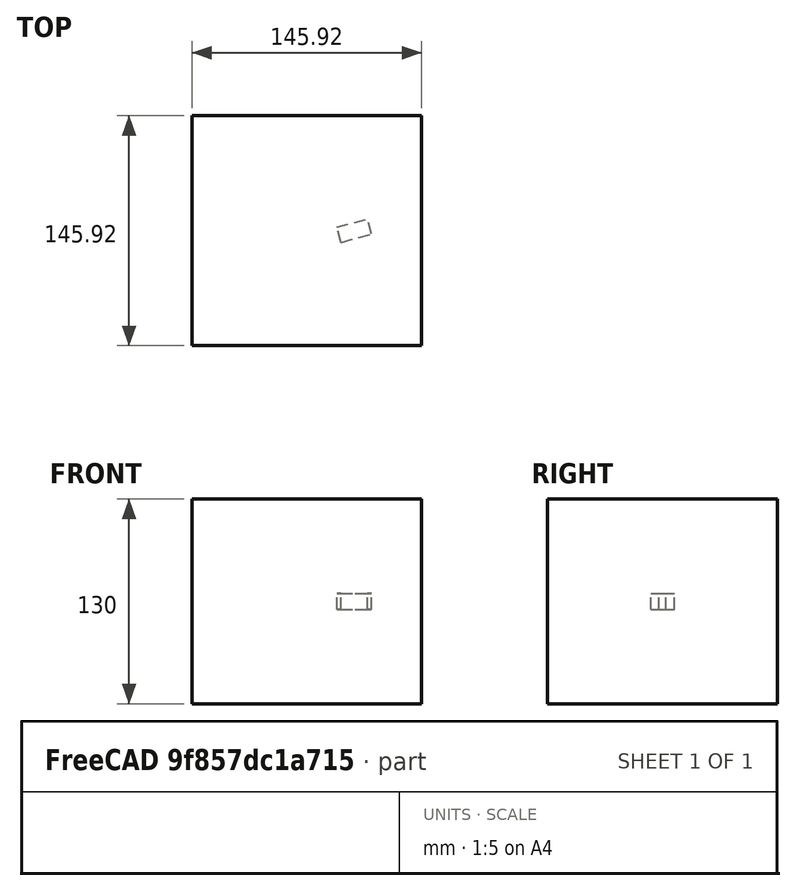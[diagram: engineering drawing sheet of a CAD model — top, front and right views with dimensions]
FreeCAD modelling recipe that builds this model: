
FCSTD DOCUMENT  (FreeCAD 0.20RUnknown)
Label: array-rotation-test-d
License: All rights reserved
objects: App::DocumentObjectGroupPython×1251, Part::FeaturePython×3, App::Part×2
note: 2 computed .brp shape members not serialized (recipe doc carries the construction recipe); baked Part::Feature solids carry a one-line shape summary decoded from their .brp

FEATURE [App::DocumentObjectGroupPython] HALFPI  # scripted group (container) (typed FeaturePython)
  name = HALFPI
  value = pi/2.
FEATURE [App::DocumentObjectGroupPython] PI  # scripted group (container) (typed FeaturePython)
  name = PI
  value = 1.*pi
FEATURE [App::DocumentObjectGroupPython] TWOPI  # scripted group (container) (typed FeaturePython)
  name = TWOPI
  value = 2.*pi
FEATURE [App::DocumentObjectGroupPython] Constants  # scripted group (container) (typed FeaturePython)
  Group = -> [HALFPI,PI,TWOPI]
FEATURE [App::DocumentObjectGroupPython] Variables  # scripted group (container) (typed FeaturePython)
FEATURE [App::DocumentObjectGroupPython] Quantities  # scripted group (container) (typed FeaturePython)
FEATURE [App::DocumentObjectGroupPython] Isotopes  # scripted group (container) (typed FeaturePython)
FEATURE [App::DocumentObjectGroupPython] Elements  # scripted group (container) (typed FeaturePython)
FEATURE [App::DocumentObjectGroupPython] Matrix  # scripted group (container) (typed FeaturePython)
FEATURE [App::DocumentObjectGroupPython] Surfaces  # scripted group (container) (typed FeaturePython)
FEATURE [App::DocumentObjectGroupPython] Opticals  # scripted group (container) (typed FeaturePython)
  Group = -> [Matrix,Surfaces]
FEATURE [App::DocumentObjectGroupPython] G4Isotopes  # scripted group (container) (typed FeaturePython)
FEATURE [App::DocumentObjectGroupPython] H_element  # scripted group (container) (typed FeaturePython)
  Z = 1
  atom_value = 1.008
  formula = H
  name = H_element
FEATURE [App::DocumentObjectGroupPython] He_element  # scripted group (container) (typed FeaturePython)
  Z = 2
  atom_value = 4.0026
  formula = He
  name = He_element
FEATURE [App::DocumentObjectGroupPython] Li_element  # scripted group (container) (typed FeaturePython)
  Z = 3
  atom_value = 6.94
  formula = Li
  name = Li_element
FEATURE [App::DocumentObjectGroupPython] Be_element  # scripted group (container) (typed FeaturePython)
  Z = 4
  atom_value = 9.01218
  formula = Be
  name = Be_element
FEATURE [App::DocumentObjectGroupPython] B_element  # scripted group (container) (typed FeaturePython)
  Z = 5
  atom_value = 10.81
  formula = B
  name = B_element
FEATURE [App::DocumentObjectGroupPython] C_element  # scripted group (container) (typed FeaturePython)
  Z = 6
  atom_value = 12.011
  formula = C
  name = C_element
FEATURE [App::DocumentObjectGroupPython] N_element  # scripted group (container) (typed FeaturePython)
  Z = 7
  atom_value = 14.007
  formula = N
  name = N_element
FEATURE [App::DocumentObjectGroupPython] O_element  # scripted group (container) (typed FeaturePython)
  Z = 8
  atom_value = 15.999
  formula = O
  name = O_element
FEATURE [App::DocumentObjectGroupPython] F_element  # scripted group (container) (typed FeaturePython)
  Z = 9
  atom_value = 18.9984
  formula = F
  name = F_element
FEATURE [App::DocumentObjectGroupPython] Ne_element  # scripted group (container) (typed FeaturePython)
  Z = 10
  atom_value = 20.1797
  formula = Ne
  name = Ne_element
FEATURE [App::DocumentObjectGroupPython] Na_element  # scripted group (container) (typed FeaturePython)
  Z = 11
  atom_value = 22.9898
  formula = Na
  name = Na_element
FEATURE [App::DocumentObjectGroupPython] Mg_element  # scripted group (container) (typed FeaturePython)
  Z = 12
  atom_value = 24.305
  formula = Mg
  name = Mg_element
FEATURE [App::DocumentObjectGroupPython] Al_element  # scripted group (container) (typed FeaturePython)
  Z = 13
  atom_value = 26.9815
  formula = Al
  name = Al_element
FEATURE [App::DocumentObjectGroupPython] Si_element  # scripted group (container) (typed FeaturePython)
  Z = 14
  atom_value = 28.085
  formula = Si
  name = Si_element
FEATURE [App::DocumentObjectGroupPython] P_element  # scripted group (container) (typed FeaturePython)
  Z = 15
  atom_value = 30.9738
  formula = P
  name = P_element
FEATURE [App::DocumentObjectGroupPython] S_element  # scripted group (container) (typed FeaturePython)
  Z = 16
  atom_value = 32.06
  formula = S
  name = S_element
FEATURE [App::DocumentObjectGroupPython] Cl_element  # scripted group (container) (typed FeaturePython)
  Z = 17
  atom_value = 35.45
  formula = Cl
  name = Cl_element
FEATURE [App::DocumentObjectGroupPython] Ar_element  # scripted group (container) (typed FeaturePython)
  Z = 18
  atom_value = 39.95
  formula = Ar
  name = Ar_element
FEATURE [App::DocumentObjectGroupPython] K_element  # scripted group (container) (typed FeaturePython)
  Z = 19
  atom_value = 39.0983
  formula = K
  name = K_element
FEATURE [App::DocumentObjectGroupPython] Ca_element  # scripted group (container) (typed FeaturePython)
  Z = 20
  atom_value = 40.078
  formula = Ca
  name = Ca_element
FEATURE [App::DocumentObjectGroupPython] Sc_element  # scripted group (container) (typed FeaturePython)
  Z = 21
  atom_value = 44.9559
  formula = Sc
  name = Sc_element
FEATURE [App::DocumentObjectGroupPython] Ti_element  # scripted group (container) (typed FeaturePython)
  Z = 22
  atom_value = 47.867
  formula = Ti
  name = Ti_element
FEATURE [App::DocumentObjectGroupPython] V_element  # scripted group (container) (typed FeaturePython)
  Z = 23
  atom_value = 50.9415
  formula = V
  name = V_element
FEATURE [App::DocumentObjectGroupPython] Cr_element  # scripted group (container) (typed FeaturePython)
  Z = 24
  atom_value = 51.9961
  formula = Cr
  name = Cr_element
FEATURE [App::DocumentObjectGroupPython] Mn_element  # scripted group (container) (typed FeaturePython)
  Z = 25
  atom_value = 54.938
  formula = Mn
  name = Mn_element
FEATURE [App::DocumentObjectGroupPython] Fe_element  # scripted group (container) (typed FeaturePython)
  Z = 26
  atom_value = 55.845
  formula = Fe
  name = Fe_element
FEATURE [App::DocumentObjectGroupPython] Co_element  # scripted group (container) (typed FeaturePython)
  Z = 27
  atom_value = 58.9332
  formula = Co
  name = Co_element
FEATURE [App::DocumentObjectGroupPython] Ni_element  # scripted group (container) (typed FeaturePython)
  Z = 28
  atom_value = 58.6934
  formula = Ni
  name = Ni_element
FEATURE [App::DocumentObjectGroupPython] Cu_element  # scripted group (container) (typed FeaturePython)
  Z = 29
  atom_value = 63.546
  formula = Cu
  name = Cu_element
FEATURE [App::DocumentObjectGroupPython] Zn_element  # scripted group (container) (typed FeaturePython)
  Z = 30
  atom_value = 65.38
  formula = Zn
  name = Zn_element
FEATURE [App::DocumentObjectGroupPython] Ga_element  # scripted group (container) (typed FeaturePython)
  Z = 31
  atom_value = 69.723
  formula = Ga
  name = Ga_element
FEATURE [App::DocumentObjectGroupPython] Ge_element  # scripted group (container) (typed FeaturePython)
  Z = 32
  atom_value = 72.63
  formula = Ge
  name = Ge_element
FEATURE [App::DocumentObjectGroupPython] As_element  # scripted group (container) (typed FeaturePython)
  Z = 33
  atom_value = 74.9216
  formula = As
  name = As_element
FEATURE [App::DocumentObjectGroupPython] Se_element  # scripted group (container) (typed FeaturePython)
  Z = 34
  atom_value = 78.971
  formula = Se
  name = Se_element
FEATURE [App::DocumentObjectGroupPython] Br_element  # scripted group (container) (typed FeaturePython)
  Z = 35
  atom_value = 79.904
  formula = Br
  name = Br_element
FEATURE [App::DocumentObjectGroupPython] Kr_element  # scripted group (container) (typed FeaturePython)
  Z = 36
  atom_value = 83.798
  formula = Kr
  name = Kr_element
FEATURE [App::DocumentObjectGroupPython] Rb_element  # scripted group (container) (typed FeaturePython)
  Z = 37
  atom_value = 85.4678
  formula = Rb
  name = Rb_element
FEATURE [App::DocumentObjectGroupPython] Sr_element  # scripted group (container) (typed FeaturePython)
  Z = 38
  atom_value = 87.62
  formula = Sr
  name = Sr_element
FEATURE [App::DocumentObjectGroupPython] Y_element  # scripted group (container) (typed FeaturePython)
  Z = 39
  atom_value = 88.9058
  formula = Y
  name = Y_element
FEATURE [App::DocumentObjectGroupPython] Zr_element  # scripted group (container) (typed FeaturePython)
  Z = 40
  atom_value = 91.224
  formula = Zr
  name = Zr_element
FEATURE [App::DocumentObjectGroupPython] Nb_element  # scripted group (container) (typed FeaturePython)
  Z = 41
  atom_value = 92.9064
  formula = Nb
  name = Nb_element
FEATURE [App::DocumentObjectGroupPython] Mo_element  # scripted group (container) (typed FeaturePython)
  Z = 42
  atom_value = 95.95
  formula = Mo
  name = Mo_element
FEATURE [App::DocumentObjectGroupPython] Tc_element  # scripted group (container) (typed FeaturePython)
  Z = 43
  atom_value = 97
  formula = Tc
  name = Tc_element
FEATURE [App::DocumentObjectGroupPython] Ru_element  # scripted group (container) (typed FeaturePython)
  Z = 44
  atom_value = 101.07
  formula = Ru
  name = Ru_element
FEATURE [App::DocumentObjectGroupPython] Rh_element  # scripted group (container) (typed FeaturePython)
  Z = 45
  atom_value = 102.905
  formula = Rh
  name = Rh_element
FEATURE [App::DocumentObjectGroupPython] Pd_element  # scripted group (container) (typed FeaturePython)
  Z = 46
  atom_value = 106.42
  formula = Pd
  name = Pd_element
FEATURE [App::DocumentObjectGroupPython] Ag_element  # scripted group (container) (typed FeaturePython)
  Z = 47
  atom_value = 107.868
  formula = Ag
  name = Ag_element
FEATURE [App::DocumentObjectGroupPython] Cd_element  # scripted group (container) (typed FeaturePython)
  Z = 48
  atom_value = 112.414
  formula = Cd
  name = Cd_element
FEATURE [App::DocumentObjectGroupPython] In_element  # scripted group (container) (typed FeaturePython)
  Z = 49
  atom_value = 114.818
  formula = In
  name = In_element
FEATURE [App::DocumentObjectGroupPython] Sn_element  # scripted group (container) (typed FeaturePython)
  Z = 50
  atom_value = 118.71
  formula = Sn
  name = Sn_element
FEATURE [App::DocumentObjectGroupPython] Sb_element  # scripted group (container) (typed FeaturePython)
  Z = 51
  atom_value = 121.76
  formula = Sb
  name = Sb_element
FEATURE [App::DocumentObjectGroupPython] Te_element  # scripted group (container) (typed FeaturePython)
  Z = 52
  atom_value = 127.6
  formula = Te
  name = Te_element
FEATURE [App::DocumentObjectGroupPython] I_element  # scripted group (container) (typed FeaturePython)
  Z = 53
  atom_value = 126.904
  formula = I
  name = I_element
FEATURE [App::DocumentObjectGroupPython] Xe_element  # scripted group (container) (typed FeaturePython)
  Z = 54
  atom_value = 131.293
  formula = Xe
  name = Xe_element
FEATURE [App::DocumentObjectGroupPython] Cs_element  # scripted group (container) (typed FeaturePython)
  Z = 55
  atom_value = 132.905
  formula = Cs
  name = Cs_element
FEATURE [App::DocumentObjectGroupPython] Ba_element  # scripted group (container) (typed FeaturePython)
  Z = 56
  atom_value = 137.327
  formula = Ba
  name = Ba_element
FEATURE [App::DocumentObjectGroupPython] La_element  # scripted group (container) (typed FeaturePython)
  Z = 57
  atom_value = 138.905
  formula = La
  name = La_element
FEATURE [App::DocumentObjectGroupPython] Ce_element  # scripted group (container) (typed FeaturePython)
  Z = 58
  atom_value = 140.116
  formula = Ce
  name = Ce_element
FEATURE [App::DocumentObjectGroupPython] Pr_element  # scripted group (container) (typed FeaturePython)
  Z = 59
  atom_value = 140.908
  formula = Pr
  name = Pr_element
FEATURE [App::DocumentObjectGroupPython] Nd_element  # scripted group (container) (typed FeaturePython)
  Z = 60
  atom_value = 144.242
  formula = Nd
  name = Nd_element
FEATURE [App::DocumentObjectGroupPython] Pm_element  # scripted group (container) (typed FeaturePython)
  Z = 61
  atom_value = 145
  formula = Pm
  name = Pm_element
FEATURE [App::DocumentObjectGroupPython] Sm_element  # scripted group (container) (typed FeaturePython)
  Z = 62
  atom_value = 150.36
  formula = Sm
  name = Sm_element
FEATURE [App::DocumentObjectGroupPython] Eu_element  # scripted group (container) (typed FeaturePython)
  Z = 63
  atom_value = 151.964
  formula = Eu
  name = Eu_element
FEATURE [App::DocumentObjectGroupPython] Gd_element  # scripted group (container) (typed FeaturePython)
  Z = 64
  atom_value = 157.25
  formula = Gd
  name = Gd_element
FEATURE [App::DocumentObjectGroupPython] Tb_element  # scripted group (container) (typed FeaturePython)
  Z = 65
  atom_value = 158.925
  formula = Tb
  name = Tb_element
FEATURE [App::DocumentObjectGroupPython] Dy_element  # scripted group (container) (typed FeaturePython)
  Z = 66
  atom_value = 162.5
  formula = Dy
  name = Dy_element
FEATURE [App::DocumentObjectGroupPython] Ho_element  # scripted group (container) (typed FeaturePython)
  Z = 67
  atom_value = 164.93
  formula = Ho
  name = Ho_element
FEATURE [App::DocumentObjectGroupPython] Er_element  # scripted group (container) (typed FeaturePython)
  Z = 68
  atom_value = 167.259
  formula = Er
  name = Er_element
FEATURE [App::DocumentObjectGroupPython] Tm_element  # scripted group (container) (typed FeaturePython)
  Z = 69
  atom_value = 168.934
  formula = Tm
  name = Tm_element
FEATURE [App::DocumentObjectGroupPython] Yb_element  # scripted group (container) (typed FeaturePython)
  Z = 70
  atom_value = 173.045
  formula = Yb
  name = Yb_element
FEATURE [App::DocumentObjectGroupPython] Lu_element  # scripted group (container) (typed FeaturePython)
  Z = 71
  atom_value = 174.967
  formula = Lu
  name = Lu_element
FEATURE [App::DocumentObjectGroupPython] Hf_element  # scripted group (container) (typed FeaturePython)
  Z = 72
  atom_value = 178.49
  formula = Hf
  name = Hf_element
FEATURE [App::DocumentObjectGroupPython] Ta_element  # scripted group (container) (typed FeaturePython)
  Z = 73
  atom_value = 180.948
  formula = Ta
  name = Ta_element
FEATURE [App::DocumentObjectGroupPython] W_element  # scripted group (container) (typed FeaturePython)
  Z = 74
  atom_value = 183.84
  formula = W
  name = W_element
FEATURE [App::DocumentObjectGroupPython] Re_element  # scripted group (container) (typed FeaturePython)
  Z = 75
  atom_value = 186.207
  formula = Re
  name = Re_element
FEATURE [App::DocumentObjectGroupPython] Os_element  # scripted group (container) (typed FeaturePython)
  Z = 76
  atom_value = 190.23
  formula = Os
  name = Os_element
FEATURE [App::DocumentObjectGroupPython] Ir_element  # scripted group (container) (typed FeaturePython)
  Z = 77
  atom_value = 192.217
  formula = Ir
  name = Ir_element
FEATURE [App::DocumentObjectGroupPython] Pt_element  # scripted group (container) (typed FeaturePython)
  Z = 78
  atom_value = 195.084
  formula = Pt
  name = Pt_element
FEATURE [App::DocumentObjectGroupPython] Au_element  # scripted group (container) (typed FeaturePython)
  Z = 79
  atom_value = 196.967
  formula = Au
  name = Au_element
FEATURE [App::DocumentObjectGroupPython] Hg_element  # scripted group (container) (typed FeaturePython)
  Z = 80
  atom_value = 200.592
  formula = Hg
  name = Hg_element
FEATURE [App::DocumentObjectGroupPython] Tl_element  # scripted group (container) (typed FeaturePython)
  Z = 81
  atom_value = 204.38
  formula = Tl
  name = Tl_element
FEATURE [App::DocumentObjectGroupPython] Pb_element  # scripted group (container) (typed FeaturePython)
  Z = 82
  atom_value = 207.2
  formula = Pb
  name = Pb_element
FEATURE [App::DocumentObjectGroupPython] Bi_element  # scripted group (container) (typed FeaturePython)
  Z = 83
  atom_value = 208.98
  formula = Bi
  name = Bi_element
FEATURE [App::DocumentObjectGroupPython] Po_element  # scripted group (container) (typed FeaturePython)
  Z = 84
  atom_value = 209
  formula = Po
  name = Po_element
FEATURE [App::DocumentObjectGroupPython] At_element  # scripted group (container) (typed FeaturePython)
  Z = 85
  atom_value = 210
  formula = At
  name = At_element
FEATURE [App::DocumentObjectGroupPython] Rn_element  # scripted group (container) (typed FeaturePython)
  Z = 86
  atom_value = 222
  formula = Rn
  name = Rn_element
FEATURE [App::DocumentObjectGroupPython] Fr_element  # scripted group (container) (typed FeaturePython)
  Z = 87
  atom_value = 223
  formula = Fr
  name = Fr_element
FEATURE [App::DocumentObjectGroupPython] Ra_element  # scripted group (container) (typed FeaturePython)
  Z = 88
  atom_value = 226
  formula = Ra
  name = Ra_element
FEATURE [App::DocumentObjectGroupPython] Ac_element  # scripted group (container) (typed FeaturePython)
  Z = 89
  atom_value = 227
  formula = Ac
  name = Ac_element
FEATURE [App::DocumentObjectGroupPython] Th_element  # scripted group (container) (typed FeaturePython)
  Z = 90
  atom_value = 232.038
  formula = Th
  name = Th_element
FEATURE [App::DocumentObjectGroupPython] Pa_element  # scripted group (container) (typed FeaturePython)
  Z = 91
  atom_value = 231.036
  formula = Pa
  name = Pa_element
FEATURE [App::DocumentObjectGroupPython] U_element  # scripted group (container) (typed FeaturePython)
  Z = 92
  atom_value = 238.029
  formula = U
  name = U_element
FEATURE [App::DocumentObjectGroupPython] Np_element  # scripted group (container) (typed FeaturePython)
  Z = 93
  atom_value = 237
  formula = Np
  name = Np_element
FEATURE [App::DocumentObjectGroupPython] Pu_element  # scripted group (container) (typed FeaturePython)
  Z = 94
  atom_value = 244
  formula = Pu
  name = Pu_element
FEATURE [App::DocumentObjectGroupPython] Am_element  # scripted group (container) (typed FeaturePython)
  Z = 95
  atom_value = 243
  formula = Am
  name = Am_element
FEATURE [App::DocumentObjectGroupPython] Cm_element  # scripted group (container) (typed FeaturePython)
  Z = 96
  atom_value = 247
  formula = Cm
  name = Cm_element
FEATURE [App::DocumentObjectGroupPython] Bk_element  # scripted group (container) (typed FeaturePython)
  Z = 97
  atom_value = 247
  formula = Bk
  name = Bk_element
FEATURE [App::DocumentObjectGroupPython] Cf_element  # scripted group (container) (typed FeaturePython)
  Z = 98
  atom_value = 251
  formula = Cf
  name = Cf_element
FEATURE [App::DocumentObjectGroupPython] G4Elements  # scripted group (container) (typed FeaturePython)
  Group = -> [H_element,He_element,Li_element,Be_element,B_element,C_element,N_element,O_element,F_element,Ne_element,Na_element,Mg_element,Al_element,Si_element,P_element,S_element,Cl_element,Ar_element,K_element,Ca_element,Sc_element,Ti_element,V_element,Cr_element,Mn_element,Fe_element,Co_element,Ni_element,Cu_element,Zn_element,Ga_element,Ge_element,As_element,Se_element,Br_element,Kr_element,Rb_element,+61 more]
FEATURE [App::DocumentObjectGroupPython] H_element001  label="H_element : 0.101"  # scripted group (container) (typed FeaturePython)
  n = 0.101327
FEATURE [App::DocumentObjectGroupPython] C_element001  label="C_element : 0.775"  # scripted group (container) (typed FeaturePython)
  n = 0.7755
FEATURE [App::DocumentObjectGroupPython] N_element001  label="N_element : 0.035"  # scripted group (container) (typed FeaturePython)
  n = 0.035057
FEATURE [App::DocumentObjectGroupPython] O_element001  label="O_element : 0.052"  # scripted group (container) (typed FeaturePython)
  n = 0.0523159
FEATURE [App::DocumentObjectGroupPython] F_element001  label="F_element : 0.017"  # scripted group (container) (typed FeaturePython)
  n = 0.017422
FEATURE [App::DocumentObjectGroupPython] Ca_element001  label="Ca_element : 0.018"  # scripted group (container) (typed FeaturePython)
  n = 0.018378
FEATURE [App::DocumentObjectGroupPython] G4_A_150_TISSUE  label="G4_A-150_TISSUE"  # scripted group (container) (typed FeaturePython)
  Dunit = g/cm3
  Dvalue = 1.127
  Group = -> [H_element001,C_element001,N_element001,O_element001,F_element001,Ca_element001]
  conduct = 2
  density = 1
  expand = 3
  formula = G4_A-150_TISSUE
  name = G4_A-150_TISSUE
  specific = 4
FEATURE [App::DocumentObjectGroupPython] C_element002  label="C_element : 3"  # scripted group (container) (typed FeaturePython)
  n = 3
  ref = C_element
FEATURE [App::DocumentObjectGroupPython] H_element002  label="H_element : 6"  # scripted group (container) (typed FeaturePython)
  n = 6
  ref = H_element
FEATURE [App::DocumentObjectGroupPython] O_element002  label="O_element : 1"  # scripted group (container) (typed FeaturePython)
  n = 1
  ref = O_element
FEATURE [App::DocumentObjectGroupPython] G4_ACETONE  # scripted group (container) (typed FeaturePython)
  Dunit = g/cm3
  Dvalue = 0.7899
  Group = -> [C_element002,H_element002,O_element002]
  conduct = 2
  density = 1
  expand = 3
  formula = G4_ACETONE
  name = G4_ACETONE
  specific = 4
FEATURE [App::DocumentObjectGroupPython] C_element003  label="C_element : 2"  # scripted group (container) (typed FeaturePython)
  n = 2
  ref = C_element
FEATURE [App::DocumentObjectGroupPython] H_element003  label="H_element : 2"  # scripted group (container) (typed FeaturePython)
  n = 2
  ref = H_element
FEATURE [App::DocumentObjectGroupPython] G4_ACETYLENE  # scripted group (container) (typed FeaturePython)
  Dunit = g/cm3
  Dvalue = 0.0010967
  Group = -> [C_element003,H_element003]
  conduct = 2
  density = 1
  expand = 3
  formula = G4_ACETYLENE
  name = G4_ACETYLENE
  specific = 4
FEATURE [App::DocumentObjectGroupPython] C_element004  label="C_element : 5"  # scripted group (container) (typed FeaturePython)
  n = 5
  ref = C_element
FEATURE [App::DocumentObjectGroupPython] H_element004  label="H_element : 5"  # scripted group (container) (typed FeaturePython)
  n = 5
  ref = H_element
FEATURE [App::DocumentObjectGroupPython] N_element002  label="N_element : 5"  # scripted group (container) (typed FeaturePython)
  n = 5
  ref = N_element
FEATURE [App::DocumentObjectGroupPython] G4_ADENINE  # scripted group (container) (typed FeaturePython)
  Dunit = g/cm3
  Dvalue = 1.6
  Group = -> [C_element004,H_element004,N_element002]
  conduct = 2
  density = 1
  expand = 3
  formula = G4_ADENINE
  name = G4_ADENINE
  specific = 4
FEATURE [App::DocumentObjectGroupPython] H_element005  label="H_element : 0.114"  # scripted group (container) (typed FeaturePython)
  n = 0.114
FEATURE [App::DocumentObjectGroupPython] C_element005  label="C_element : 0.598"  # scripted group (container) (typed FeaturePython)
  n = 0.598
FEATURE [App::DocumentObjectGroupPython] N_element003  label="N_element : 0.007"  # scripted group (container) (typed FeaturePython)
  n = 0.007
FEATURE [App::DocumentObjectGroupPython] O_element003  label="O_element : 0.278"  # scripted group (container) (typed FeaturePython)
  n = 0.278
FEATURE [App::DocumentObjectGroupPython] Na_element001  label="Na_element : 0.001"  # scripted group (container) (typed FeaturePython)
  n = 0.001
FEATURE [App::DocumentObjectGroupPython] S_element001  label="S_element : 0.001"  # scripted group (container) (typed FeaturePython)
  n = 0.001
FEATURE [App::DocumentObjectGroupPython] Cl_element001  label="Cl_element : 0.001"  # scripted group (container) (typed FeaturePython)
  n = 0.001
FEATURE [App::DocumentObjectGroupPython] G4_ADIPOSE_TISSUE_ICRP  # scripted group (container) (typed FeaturePython)
  Dunit = g/cm3
  Dvalue = 0.95
  Group = -> [H_element005,C_element005,N_element003,O_element003,Na_element001,S_element001,Cl_element001]
  conduct = 2
  density = 1
  expand = 3
  formula = G4_ADIPOSE_TISSUE_ICRP
  name = G4_ADIPOSE_TISSUE_ICRP
  specific = 4
FEATURE [App::DocumentObjectGroupPython] C_element006  label="C_element : 0.000"  # scripted group (container) (typed FeaturePython)
  n = 0.000124
FEATURE [App::DocumentObjectGroupPython] N_element004  label="N_element : 0.755"  # scripted group (container) (typed FeaturePython)
  n = 0.755268
FEATURE [App::DocumentObjectGroupPython] O_element004  label="O_element : 0.232"  # scripted group (container) (typed FeaturePython)
  n = 0.231781
FEATURE [App::DocumentObjectGroupPython] Ar_element001  label="Ar_element : 0.013"  # scripted group (container) (typed FeaturePython)
  n = 0.012827
FEATURE [App::DocumentObjectGroupPython] G4_AIR  # scripted group (container) (typed FeaturePython)
  Dunit = g/cm3
  Dvalue = 0.00120479
  Group = -> [C_element006,N_element004,O_element004,Ar_element001]
  conduct = 2
  density = 1
  expand = 3
  formula = G4_AIR
  name = G4_AIR
  specific = 4
FEATURE [App::DocumentObjectGroupPython] C_element007  label="C_element : 006"  # scripted group (container) (typed FeaturePython)
  n = 3
  ref = C_element
FEATURE [App::DocumentObjectGroupPython] H_element006  label="H_element : 7"  # scripted group (container) (typed FeaturePython)
  n = 7
  ref = H_element
FEATURE [App::DocumentObjectGroupPython] N_element005  label="N_element : 1"  # scripted group (container) (typed FeaturePython)
  n = 1
  ref = N_element
FEATURE [App::DocumentObjectGroupPython] O_element005  label="O_element : 2"  # scripted group (container) (typed FeaturePython)
  n = 2
  ref = O_element
FEATURE [App::DocumentObjectGroupPython] G4_ALANINE  # scripted group (container) (typed FeaturePython)
  Dunit = g/cm3
  Dvalue = 1.42
  Group = -> [C_element007,H_element006,N_element005,O_element005]
  conduct = 2
  density = 1
  expand = 3
  formula = G4_ALANINE
  name = G4_ALANINE
  specific = 4
FEATURE [App::DocumentObjectGroupPython] Al_element001  label="Al_element : 2"  # scripted group (container) (typed FeaturePython)
  n = 2
  ref = Al_element
FEATURE [App::DocumentObjectGroupPython] O_element006  label="O_element : 3"  # scripted group (container) (typed FeaturePython)
  n = 3
  ref = O_element
FEATURE [App::DocumentObjectGroupPython] G4_ALUMINUM_OXIDE  # scripted group (container) (typed FeaturePython)
  Dunit = g/cm3
  Dvalue = 3.97
  Group = -> [Al_element001,O_element006]
  conduct = 2
  density = 1
  expand = 3
  formula = G4_ALUMINUM_OXIDE
  name = G4_ALUMINUM_OXIDE
  specific = 4
FEATURE [App::DocumentObjectGroupPython] H_element007  label="H_element : 0.106"  # scripted group (container) (typed FeaturePython)
  n = 0.10593
FEATURE [App::DocumentObjectGroupPython] C_element008  label="C_element : 0.789"  # scripted group (container) (typed FeaturePython)
  n = 0.788974
FEATURE [App::DocumentObjectGroupPython] O_element007  label="O_element : 0.105"  # scripted group (container) (typed FeaturePython)
  n = 0.105096
FEATURE [App::DocumentObjectGroupPython] G4_AMBER  # scripted group (container) (typed FeaturePython)
  Dunit = g/cm3
  Dvalue = 1.1
  Group = -> [H_element007,C_element008,O_element007]
  conduct = 2
  density = 1
  expand = 3
  formula = G4_AMBER
  name = G4_AMBER
  specific = 4
FEATURE [App::DocumentObjectGroupPython] N_element006  label="N_element : 006"  # scripted group (container) (typed FeaturePython)
  n = 1
  ref = N_element
FEATURE [App::DocumentObjectGroupPython] H_element008  label="H_element : 3"  # scripted group (container) (typed FeaturePython)
  n = 3
  ref = H_element
FEATURE [App::DocumentObjectGroupPython] G4_AMMONIA  # scripted group (container) (typed FeaturePython)
  Dunit = g/cm3
  Dvalue = 0.000826019
  Group = -> [N_element006,H_element008]
  conduct = 2
  density = 1
  expand = 3
  formula = G4_AMMONIA
  name = G4_AMMONIA
  specific = 4
FEATURE [App::DocumentObjectGroupPython] C_element009  label="C_element : 6"  # scripted group (container) (typed FeaturePython)
  n = 6
  ref = C_element
FEATURE [App::DocumentObjectGroupPython] H_element009  label="H_element : 008"  # scripted group (container) (typed FeaturePython)
  n = 7
  ref = H_element
FEATURE [App::DocumentObjectGroupPython] N_element007  label="N_element : 007"  # scripted group (container) (typed FeaturePython)
  n = 1
  ref = N_element
FEATURE [App::DocumentObjectGroupPython] G4_ANILINE  # scripted group (container) (typed FeaturePython)
  Dunit = g/cm3
  Dvalue = 1.0235
  Group = -> [C_element009,H_element009,N_element007]
  conduct = 2
  density = 1
  expand = 3
  formula = G4_ANILINE
  name = G4_ANILINE
  specific = 4
FEATURE [App::DocumentObjectGroupPython] C_element010  label="C_element : 14"  # scripted group (container) (typed FeaturePython)
  n = 14
  ref = C_element
FEATURE [App::DocumentObjectGroupPython] H_element010  label="H_element : 10"  # scripted group (container) (typed FeaturePython)
  n = 10
  ref = H_element
FEATURE [App::DocumentObjectGroupPython] G4_ANTHRACENE  # scripted group (container) (typed FeaturePython)
  Dunit = g/cm3
  Dvalue = 1.283
  Group = -> [C_element010,H_element010]
  conduct = 2
  density = 1
  expand = 3
  formula = G4_ANTHRACENE
  name = G4_ANTHRACENE
  specific = 4
FEATURE [App::DocumentObjectGroupPython] H_element011  label="H_element : 0.065"  # scripted group (container) (typed FeaturePython)
  n = 0.0654709
FEATURE [App::DocumentObjectGroupPython] C_element011  label="C_element : 0.537"  # scripted group (container) (typed FeaturePython)
  n = 0.536944
FEATURE [App::DocumentObjectGroupPython] N_element008  label="N_element : 0.021"  # scripted group (container) (typed FeaturePython)
  n = 0.0215
FEATURE [App::DocumentObjectGroupPython] O_element008  label="O_element : 0.032"  # scripted group (container) (typed FeaturePython)
  n = 0.032085
FEATURE [App::DocumentObjectGroupPython] F_element002  label="F_element : 0.167"  # scripted group (container) (typed FeaturePython)
  n = 0.167411
FEATURE [App::DocumentObjectGroupPython] Ca_element002  label="Ca_element : 0.177"  # scripted group (container) (typed FeaturePython)
  n = 0.176589
FEATURE [App::DocumentObjectGroupPython] G4_B_100_BONE  label="G4_B-100_BONE"  # scripted group (container) (typed FeaturePython)
  Dunit = g/cm3
  Dvalue = 1.45
  Group = -> [H_element011,C_element011,N_element008,O_element008,F_element002,Ca_element002]
  conduct = 2
  density = 1
  expand = 3
  formula = G4_B-100_BONE
  name = G4_B-100_BONE
  specific = 4
FEATURE [App::DocumentObjectGroupPython] H_element012  label="H_element : 0.057"  # scripted group (container) (typed FeaturePython)
  n = 0.057441
FEATURE [App::DocumentObjectGroupPython] C_element012  label="C_element : 0.790"  # scripted group (container) (typed FeaturePython)
  n = 0.774591
FEATURE [App::DocumentObjectGroupPython] O_element009  label="O_element : 0.168"  # scripted group (container) (typed FeaturePython)
  n = 0.167968
FEATURE [App::DocumentObjectGroupPython] G4_BAKELITE  # scripted group (container) (typed FeaturePython)
  Dunit = g/cm3
  Dvalue = 1.25
  Group = -> [H_element012,C_element012,O_element009]
  conduct = 2
  density = 1
  expand = 3
  formula = G4_BAKELITE
  name = G4_BAKELITE
  specific = 4
FEATURE [App::DocumentObjectGroupPython] Ba_element001  label="Ba_element : 1"  # scripted group (container) (typed FeaturePython)
  n = 1
  ref = Ba_element
FEATURE [App::DocumentObjectGroupPython] F_element003  label="F_element : 2"  # scripted group (container) (typed FeaturePython)
  n = 2
  ref = F_element
FEATURE [App::DocumentObjectGroupPython] G4_BARIUM_FLUORIDE  # scripted group (container) (typed FeaturePython)
  Dunit = g/cm3
  Dvalue = 4.89
  Group = -> [Ba_element001,F_element003]
  conduct = 2
  density = 1
  expand = 3
  formula = G4_BARIUM_FLUORIDE
  name = G4_BARIUM_FLUORIDE
  specific = 4
FEATURE [App::DocumentObjectGroupPython] Ba_element002  label="Ba_element : 002"  # scripted group (container) (typed FeaturePython)
  n = 1
  ref = Ba_element
FEATURE [App::DocumentObjectGroupPython] S_element002  label="S_element : 1"  # scripted group (container) (typed FeaturePython)
  n = 1
  ref = S_element
FEATURE [App::DocumentObjectGroupPython] O_element010  label="O_element : 4"  # scripted group (container) (typed FeaturePython)
  n = 4
  ref = O_element
FEATURE [App::DocumentObjectGroupPython] G4_BARIUM_SULFATE  # scripted group (container) (typed FeaturePython)
  Dunit = g/cm3
  Dvalue = 4.5
  Group = -> [Ba_element002,S_element002,O_element010]
  conduct = 2
  density = 1
  expand = 3
  formula = G4_BARIUM_SULFATE
  name = G4_BARIUM_SULFATE
  specific = 4
FEATURE [App::DocumentObjectGroupPython] C_element013  label="C_element : 007"  # scripted group (container) (typed FeaturePython)
  n = 6
  ref = C_element
FEATURE [App::DocumentObjectGroupPython] H_element013  label="H_element : 009"  # scripted group (container) (typed FeaturePython)
  n = 6
  ref = H_element
FEATURE [App::DocumentObjectGroupPython] G4_BENZENE  # scripted group (container) (typed FeaturePython)
  Dunit = g/cm3
  Dvalue = 0.87865
  Group = -> [C_element013,H_element013]
  conduct = 2
  density = 1
  expand = 3
  formula = G4_BENZENE
  name = G4_BENZENE
  specific = 4
FEATURE [App::DocumentObjectGroupPython] Be_element001  label="Be_element : 1"  # scripted group (container) (typed FeaturePython)
  n = 1
  ref = Be_element
FEATURE [App::DocumentObjectGroupPython] O_element011  label="O_element : 005"  # scripted group (container) (typed FeaturePython)
  n = 1
  ref = O_element
FEATURE [App::DocumentObjectGroupPython] G4_BERYLLIUM_OXIDE  # scripted group (container) (typed FeaturePython)
  Dunit = g/cm3
  Dvalue = 3.01
  Group = -> [Be_element001,O_element011]
  conduct = 2
  density = 1
  expand = 3
  formula = G4_BERYLLIUM_OXIDE
  name = G4_BERYLLIUM_OXIDE
  specific = 4
FEATURE [App::DocumentObjectGroupPython] Bi_element001  label="Bi_element : 4"  # scripted group (container) (typed FeaturePython)
  n = 4
  ref = Bi_element
FEATURE [App::DocumentObjectGroupPython] Ge_element001  label="Ge_element : 3"  # scripted group (container) (typed FeaturePython)
  n = 3
  ref = Ge_element
FEATURE [App::DocumentObjectGroupPython] O_element012  label="O_element : 12"  # scripted group (container) (typed FeaturePython)
  n = 12
  ref = O_element
FEATURE [App::DocumentObjectGroupPython] G4_BGO  # scripted group (container) (typed FeaturePython)
  Dunit = g/cm3
  Dvalue = 7.13
  Group = -> [Bi_element001,Ge_element001,O_element012]
  conduct = 2
  density = 1
  expand = 3
  formula = G4_BGO
  name = G4_BGO
  specific = 4
FEATURE [App::DocumentObjectGroupPython] H_element014  label="H_element : 0.102"  # scripted group (container) (typed FeaturePython)
  n = 0.102
FEATURE [App::DocumentObjectGroupPython] C_element014  label="C_element : 0.110"  # scripted group (container) (typed FeaturePython)
  n = 0.11
FEATURE [App::DocumentObjectGroupPython] N_element009  label="N_element : 0.033"  # scripted group (container) (typed FeaturePython)
  n = 0.033
FEATURE [App::DocumentObjectGroupPython] O_element013  label="O_element : 0.745"  # scripted group (container) (typed FeaturePython)
  n = 0.745
FEATURE [App::DocumentObjectGroupPython] Na_element002  label="Na_element : 0.002"  # scripted group (container) (typed FeaturePython)
  n = 0.001
FEATURE [App::DocumentObjectGroupPython] P_element001  label="P_element : 0.001"  # scripted group (container) (typed FeaturePython)
  n = 0.001
FEATURE [App::DocumentObjectGroupPython] S_element003  label="S_element : 0.002"  # scripted group (container) (typed FeaturePython)
  n = 0.002
FEATURE [App::DocumentObjectGroupPython] Cl_element002  label="Cl_element : 0.003"  # scripted group (container) (typed FeaturePython)
  n = 0.003
FEATURE [App::DocumentObjectGroupPython] K_element001  label="K_element : 0.002"  # scripted group (container) (typed FeaturePython)
  n = 0.002
FEATURE [App::DocumentObjectGroupPython] Fe_element001  label="Fe_element : 0.001"  # scripted group (container) (typed FeaturePython)
  n = 0.001
FEATURE [App::DocumentObjectGroupPython] G4_BLOOD_ICRP  # scripted group (container) (typed FeaturePython)
  Dunit = g/cm3
  Dvalue = 1.06
  Group = -> [H_element014,C_element014,N_element009,O_element013,Na_element002,P_element001,S_element003,Cl_element002,K_element001,Fe_element001]
  conduct = 2
  density = 1
  expand = 3
  formula = G4_BLOOD_ICRP
  name = G4_BLOOD_ICRP
  specific = 4
FEATURE [App::DocumentObjectGroupPython] H_element015  label="H_element : 0.064"  # scripted group (container) (typed FeaturePython)
  n = 0.064
FEATURE [App::DocumentObjectGroupPython] C_element015  label="C_element : 0.278"  # scripted group (container) (typed FeaturePython)
  n = 0.278
FEATURE [App::DocumentObjectGroupPython] N_element010  label="N_element : 0.027"  # scripted group (container) (typed FeaturePython)
  n = 0.027
FEATURE [App::DocumentObjectGroupPython] O_element014  label="O_element : 0.410"  # scripted group (container) (typed FeaturePython)
  n = 0.41
FEATURE [App::DocumentObjectGroupPython] Mg_element001  label="Mg_element : 0.002"  # scripted group (container) (typed FeaturePython)
  n = 0.002
FEATURE [App::DocumentObjectGroupPython] P_element002  label="P_element : 0.070"  # scripted group (container) (typed FeaturePython)
  n = 0.07
FEATURE [App::DocumentObjectGroupPython] S_element004  label="S_element : 0.003"  # scripted group (container) (typed FeaturePython)
  n = 0.002
FEATURE [App::DocumentObjectGroupPython] Ca_element003  label="Ca_element : 0.147"  # scripted group (container) (typed FeaturePython)
  n = 0.147
FEATURE [App::DocumentObjectGroupPython] G4_BONE_COMPACT_ICRU  # scripted group (container) (typed FeaturePython)
  Dunit = g/cm3
  Dvalue = 1.85
  Group = -> [H_element015,C_element015,N_element010,O_element014,Mg_element001,P_element002,S_element004,Ca_element003]
  conduct = 2
  density = 1
  expand = 3
  formula = G4_BONE_COMPACT_ICRU
  name = G4_BONE_COMPACT_ICRU
  specific = 4
FEATURE [App::DocumentObjectGroupPython] H_element016  label="H_element : 0.034"  # scripted group (container) (typed FeaturePython)
  n = 0.034
FEATURE [App::DocumentObjectGroupPython] C_element016  label="C_element : 0.155"  # scripted group (container) (typed FeaturePython)
  n = 0.155
FEATURE [App::DocumentObjectGroupPython] N_element011  label="N_element : 0.042"  # scripted group (container) (typed FeaturePython)
  n = 0.042
FEATURE [App::DocumentObjectGroupPython] O_element015  label="O_element : 0.435"  # scripted group (container) (typed FeaturePython)
  n = 0.435
FEATURE [App::DocumentObjectGroupPython] Na_element003  label="Na_element : 0.003"  # scripted group (container) (typed FeaturePython)
  n = 0.001
FEATURE [App::DocumentObjectGroupPython] Mg_element002  label="Mg_element : 0.003"  # scripted group (container) (typed FeaturePython)
  n = 0.002
FEATURE [App::DocumentObjectGroupPython] P_element003  label="P_element : 0.103"  # scripted group (container) (typed FeaturePython)
  n = 0.103
FEATURE [App::DocumentObjectGroupPython] S_element005  label="S_element : 0.004"  # scripted group (container) (typed FeaturePython)
  n = 0.003
FEATURE [App::DocumentObjectGroupPython] Ca_element004  label="Ca_element : 0.225"  # scripted group (container) (typed FeaturePython)
  n = 0.225
FEATURE [App::DocumentObjectGroupPython] G4_BONE_CORTICAL_ICRP  # scripted group (container) (typed FeaturePython)
  Dunit = g/cm3
  Dvalue = 1.92
  Group = -> [H_element016,C_element016,N_element011,O_element015,Na_element003,Mg_element002,P_element003,S_element005,Ca_element004]
  conduct = 2
  density = 1
  expand = 3
  formula = G4_BONE_CORTICAL_ICRP
  name = G4_BONE_CORTICAL_ICRP
  specific = 4
FEATURE [App::DocumentObjectGroupPython] B_element001  label="B_element : 4"  # scripted group (container) (typed FeaturePython)
  n = 4
  ref = B_element
FEATURE [App::DocumentObjectGroupPython] C_element017  label="C_element : 1"  # scripted group (container) (typed FeaturePython)
  n = 1
  ref = C_element
FEATURE [App::DocumentObjectGroupPython] G4_BORON_CARBIDE  # scripted group (container) (typed FeaturePython)
  Dunit = g/cm3
  Dvalue = 2.52
  Group = -> [B_element001,C_element017]
  conduct = 2
  density = 1
  expand = 3
  formula = G4_BORON_CARBIDE
  name = G4_BORON_CARBIDE
  specific = 4
FEATURE [App::DocumentObjectGroupPython] B_element002  label="B_element : 2"  # scripted group (container) (typed FeaturePython)
  n = 2
  ref = B_element
FEATURE [App::DocumentObjectGroupPython] O_element016  label="O_element : 006"  # scripted group (container) (typed FeaturePython)
  n = 3
  ref = O_element
FEATURE [App::DocumentObjectGroupPython] G4_BORON_OXIDE  # scripted group (container) (typed FeaturePython)
  Dunit = g/cm3
  Dvalue = 1.812
  Group = -> [B_element002,O_element016]
  conduct = 2
  density = 1
  expand = 3
  formula = G4_BORON_OXIDE
  name = G4_BORON_OXIDE
  specific = 4
FEATURE [App::DocumentObjectGroupPython] H_element017  label="H_element : 0.107"  # scripted group (container) (typed FeaturePython)
  n = 0.107
FEATURE [App::DocumentObjectGroupPython] C_element018  label="C_element : 0.145"  # scripted group (container) (typed FeaturePython)
  n = 0.145
FEATURE [App::DocumentObjectGroupPython] N_element012  label="N_element : 0.022"  # scripted group (container) (typed FeaturePython)
  n = 0.022
FEATURE [App::DocumentObjectGroupPython] O_element017  label="O_element : 0.712"  # scripted group (container) (typed FeaturePython)
  n = 0.712
FEATURE [App::DocumentObjectGroupPython] Na_element004  label="Na_element : 0.004"  # scripted group (container) (typed FeaturePython)
  n = 0.002
FEATURE [App::DocumentObjectGroupPython] P_element004  label="P_element : 0.004"  # scripted group (container) (typed FeaturePython)
  n = 0.004
FEATURE [App::DocumentObjectGroupPython] S_element006  label="S_element : 0.005"  # scripted group (container) (typed FeaturePython)
  n = 0.002
FEATURE [App::DocumentObjectGroupPython] Cl_element003  label="Cl_element : 0.004"  # scripted group (container) (typed FeaturePython)
  n = 0.003
FEATURE [App::DocumentObjectGroupPython] K_element002  label="K_element : 0.003"  # scripted group (container) (typed FeaturePython)
  n = 0.003
FEATURE [App::DocumentObjectGroupPython] G4_BRAIN_ICRP  # scripted group (container) (typed FeaturePython)
  Dunit = g/cm3
  Dvalue = 1.04
  Group = -> [H_element017,C_element018,N_element012,O_element017,Na_element004,P_element004,S_element006,Cl_element003,K_element002]
  conduct = 2
  density = 1
  expand = 3
  formula = G4_BRAIN_ICRP
  name = G4_BRAIN_ICRP
  specific = 4
FEATURE [App::DocumentObjectGroupPython] C_element019  label="C_element : 4"  # scripted group (container) (typed FeaturePython)
  n = 4
  ref = C_element
FEATURE [App::DocumentObjectGroupPython] H_element018  label="H_element : 010"  # scripted group (container) (typed FeaturePython)
  n = 10
  ref = H_element
FEATURE [App::DocumentObjectGroupPython] G4_BUTANE  # scripted group (container) (typed FeaturePython)
  Dunit = g/cm3
  Dvalue = 0.00249343
  Group = -> [C_element019,H_element018]
  conduct = 2
  density = 1
  expand = 3
  formula = G4_BUTANE
  name = G4_BUTANE
  specific = 4
FEATURE [App::DocumentObjectGroupPython] C_element020  label="C_element : 008"  # scripted group (container) (typed FeaturePython)
  n = 4
  ref = C_element
FEATURE [App::DocumentObjectGroupPython] H_element019  label="H_element : 011"  # scripted group (container) (typed FeaturePython)
  n = 10
  ref = H_element
FEATURE [App::DocumentObjectGroupPython] O_element018  label="O_element : 007"  # scripted group (container) (typed FeaturePython)
  n = 1
  ref = O_element
FEATURE [App::DocumentObjectGroupPython] G4_N_BUTYL_ALCOHOL  label="G4_N-BUTYL_ALCOHOL"  # scripted group (container) (typed FeaturePython)
  Dunit = g/cm3
  Dvalue = 0.8098
  Group = -> [C_element020,H_element019,O_element018]
  conduct = 2
  density = 1
  expand = 3
  formula = G4_N-BUTYL_ALCOHOL
  name = G4_N-BUTYL_ALCOHOL
  specific = 4
FEATURE [App::DocumentObjectGroupPython] H_element020  label="H_element : 0.025"  # scripted group (container) (typed FeaturePython)
  n = 0.02468
FEATURE [App::DocumentObjectGroupPython] C_element021  label="C_element : 0.502"  # scripted group (container) (typed FeaturePython)
  n = 0.501611
FEATURE [App::DocumentObjectGroupPython] O_element019  label="O_element : 0.005"  # scripted group (container) (typed FeaturePython)
  n = 0.004527
FEATURE [App::DocumentObjectGroupPython] F_element004  label="F_element : 0.465"  # scripted group (container) (typed FeaturePython)
  n = 0.465209
FEATURE [App::DocumentObjectGroupPython] Si_element001  label="Si_element : 0.004"  # scripted group (container) (typed FeaturePython)
  n = 0.003973
FEATURE [App::DocumentObjectGroupPython] G4_C_552  label="G4_C-552"  # scripted group (container) (typed FeaturePython)
  Dunit = g/cm3
  Dvalue = 1.76
  Group = -> [H_element020,C_element021,O_element019,F_element004,Si_element001]
  conduct = 2
  density = 1
  expand = 3
  formula = G4_C-552
  name = G4_C-552
  specific = 4
FEATURE [App::DocumentObjectGroupPython] Cd_element001  label="Cd_element : 1"  # scripted group (container) (typed FeaturePython)
  n = 1
  ref = Cd_element
FEATURE [App::DocumentObjectGroupPython] Te_element001  label="Te_element : 1"  # scripted group (container) (typed FeaturePython)
  n = 1
  ref = Te_element
FEATURE [App::DocumentObjectGroupPython] G4_CADMIUM_TELLURIDE  # scripted group (container) (typed FeaturePython)
  Dunit = g/cm3
  Dvalue = 6.2
  Group = -> [Cd_element001,Te_element001]
  conduct = 2
  density = 1
  expand = 3
  formula = G4_CADMIUM_TELLURIDE
  name = G4_CADMIUM_TELLURIDE
  specific = 4
FEATURE [App::DocumentObjectGroupPython] Cd_element002  label="Cd_element : 002"  # scripted group (container) (typed FeaturePython)
  n = 1
  ref = Cd_element
FEATURE [App::DocumentObjectGroupPython] W_element001  label="W_element : 1"  # scripted group (container) (typed FeaturePython)
  n = 1
  ref = W_element
FEATURE [App::DocumentObjectGroupPython] O_element020  label="O_element : 008"  # scripted group (container) (typed FeaturePython)
  n = 4
  ref = O_element
FEATURE [App::DocumentObjectGroupPython] G4_CADMIUM_TUNGSTATE  # scripted group (container) (typed FeaturePython)
  Dunit = g/cm3
  Dvalue = 7.9
  Group = -> [Cd_element002,W_element001,O_element020]
  conduct = 2
  density = 1
  expand = 3
  formula = G4_CADMIUM_TUNGSTATE
  name = G4_CADMIUM_TUNGSTATE
  specific = 4
FEATURE [App::DocumentObjectGroupPython] Ca_element005  label="Ca_element : 1"  # scripted group (container) (typed FeaturePython)
  n = 1
  ref = Ca_element
FEATURE [App::DocumentObjectGroupPython] C_element022  label="C_element : 009"  # scripted group (container) (typed FeaturePython)
  n = 1
  ref = C_element
FEATURE [App::DocumentObjectGroupPython] O_element021  label="O_element : 009"  # scripted group (container) (typed FeaturePython)
  n = 3
  ref = O_element
FEATURE [App::DocumentObjectGroupPython] G4_CALCIUM_CARBONATE  # scripted group (container) (typed FeaturePython)
  Dunit = g/cm3
  Dvalue = 2.8
  Group = -> [Ca_element005,C_element022,O_element021]
  conduct = 2
  density = 1
  expand = 3
  formula = G4_CALCIUM_CARBONATE
  name = G4_CALCIUM_CARBONATE
  specific = 4
FEATURE [App::DocumentObjectGroupPython] Ca_element006  label="Ca_element : 002"  # scripted group (container) (typed FeaturePython)
  n = 1
  ref = Ca_element
FEATURE [App::DocumentObjectGroupPython] F_element005  label="F_element : 003"  # scripted group (container) (typed FeaturePython)
  n = 2
  ref = F_element
FEATURE [App::DocumentObjectGroupPython] G4_CALCIUM_FLUORIDE  # scripted group (container) (typed FeaturePython)
  Dunit = g/cm3
  Dvalue = 3.18
  Group = -> [Ca_element006,F_element005]
  conduct = 2
  density = 1
  expand = 3
  formula = G4_CALCIUM_FLUORIDE
  name = G4_CALCIUM_FLUORIDE
  specific = 4
FEATURE [App::DocumentObjectGroupPython] Ca_element007  label="Ca_element : 003"  # scripted group (container) (typed FeaturePython)
  n = 1
  ref = Ca_element
FEATURE [App::DocumentObjectGroupPython] O_element022  label="O_element : 010"  # scripted group (container) (typed FeaturePython)
  n = 1
  ref = O_element
FEATURE [App::DocumentObjectGroupPython] G4_CALCIUM_OXIDE  # scripted group (container) (typed FeaturePython)
  Dunit = g/cm3
  Dvalue = 3.3
  Group = -> [Ca_element007,O_element022]
  conduct = 2
  density = 1
  expand = 3
  formula = G4_CALCIUM_OXIDE
  name = G4_CALCIUM_OXIDE
  specific = 4
FEATURE [App::DocumentObjectGroupPython] Ca_element008  label="Ca_element : 004"  # scripted group (container) (typed FeaturePython)
  n = 1
  ref = Ca_element
FEATURE [App::DocumentObjectGroupPython] S_element007  label="S_element : 002"  # scripted group (container) (typed FeaturePython)
  n = 1
  ref = S_element
FEATURE [App::DocumentObjectGroupPython] O_element023  label="O_element : 011"  # scripted group (container) (typed FeaturePython)
  n = 4
  ref = O_element
FEATURE [App::DocumentObjectGroupPython] G4_CALCIUM_SULFATE  # scripted group (container) (typed FeaturePython)
  Dunit = g/cm3
  Dvalue = 2.96
  Group = -> [Ca_element008,S_element007,O_element023]
  conduct = 2
  density = 1
  expand = 3
  formula = G4_CALCIUM_SULFATE
  name = G4_CALCIUM_SULFATE
  specific = 4
FEATURE [App::DocumentObjectGroupPython] Ca_element009  label="Ca_element : 005"  # scripted group (container) (typed FeaturePython)
  n = 1
  ref = Ca_element
FEATURE [App::DocumentObjectGroupPython] W_element002  label="W_element : 002"  # scripted group (container) (typed FeaturePython)
  n = 1
  ref = W_element
FEATURE [App::DocumentObjectGroupPython] O_element024  label="O_element : 012"  # scripted group (container) (typed FeaturePython)
  n = 4
  ref = O_element
FEATURE [App::DocumentObjectGroupPython] G4_CALCIUM_TUNGSTATE  # scripted group (container) (typed FeaturePython)
  Dunit = g/cm3
  Dvalue = 6.062
  Group = -> [Ca_element009,W_element002,O_element024]
  conduct = 2
  density = 1
  expand = 3
  formula = G4_CALCIUM_TUNGSTATE
  name = G4_CALCIUM_TUNGSTATE
  specific = 4
FEATURE [App::DocumentObjectGroupPython] C_element023  label="C_element : 010"  # scripted group (container) (typed FeaturePython)
  n = 1
  ref = C_element
FEATURE [App::DocumentObjectGroupPython] O_element025  label="O_element : 013"  # scripted group (container) (typed FeaturePython)
  n = 2
  ref = O_element
FEATURE [App::DocumentObjectGroupPython] G4_CARBON_DIOXIDE  # scripted group (container) (typed FeaturePython)
  Dunit = g/cm3
  Dvalue = 0.00184212
  Group = -> [C_element023,O_element025]
  conduct = 2
  density = 1
  expand = 3
  formula = G4_CARBON_DIOXIDE
  name = G4_CARBON_DIOXIDE
  specific = 4
FEATURE [App::DocumentObjectGroupPython] C_element024  label="C_element : 011"  # scripted group (container) (typed FeaturePython)
  n = 1
  ref = C_element
FEATURE [App::DocumentObjectGroupPython] Cl_element004  label="Cl_element : 4"  # scripted group (container) (typed FeaturePython)
  n = 4
  ref = Cl_element
FEATURE [App::DocumentObjectGroupPython] G4_CARBON_TETRACHLORIDE  # scripted group (container) (typed FeaturePython)
  Dunit = g/cm3
  Dvalue = 1.594
  Group = -> [C_element024,Cl_element004]
  conduct = 2
  density = 1
  expand = 3
  formula = G4_CARBON_TETRACHLORIDE
  name = G4_CARBON_TETRACHLORIDE
  specific = 4
FEATURE [App::DocumentObjectGroupPython] C_element025  label="C_element : 012"  # scripted group (container) (typed FeaturePython)
  n = 6
  ref = C_element
FEATURE [App::DocumentObjectGroupPython] H_element021  label="H_element : 012"  # scripted group (container) (typed FeaturePython)
  n = 10
  ref = H_element
FEATURE [App::DocumentObjectGroupPython] O_element026  label="O_element : 5"  # scripted group (container) (typed FeaturePython)
  n = 5
  ref = O_element
FEATURE [App::DocumentObjectGroupPython] G4_CELLULOSE_CELLOPHANE  # scripted group (container) (typed FeaturePython)
  Dunit = g/cm3
  Dvalue = 1.42
  Group = -> [C_element025,H_element021,O_element026]
  conduct = 2
  density = 1
  expand = 3
  formula = G4_CELLULOSE_CELLOPHANE
  name = G4_CELLULOSE_CELLOPHANE
  specific = 4
FEATURE [App::DocumentObjectGroupPython] H_element022  label="H_element : 0.067"  # scripted group (container) (typed FeaturePython)
  n = 0.067125
FEATURE [App::DocumentObjectGroupPython] C_element026  label="C_element : 0.545"  # scripted group (container) (typed FeaturePython)
  n = 0.545403
FEATURE [App::DocumentObjectGroupPython] O_element027  label="O_element : 0.387"  # scripted group (container) (typed FeaturePython)
  n = 0.387472
FEATURE [App::DocumentObjectGroupPython] G4_CELLULOSE_BUTYRATE  # scripted group (container) (typed FeaturePython)
  Dunit = g/cm3
  Dvalue = 1.2
  Group = -> [H_element022,C_element026,O_element027]
  conduct = 2
  density = 1
  expand = 3
  formula = G4_CELLULOSE_BUTYRATE
  name = G4_CELLULOSE_BUTYRATE
  specific = 4
FEATURE [App::DocumentObjectGroupPython] H_element023  label="H_element : 0.029"  # scripted group (container) (typed FeaturePython)
  n = 0.029216
FEATURE [App::DocumentObjectGroupPython] C_element027  label="C_element : 0.271"  # scripted group (container) (typed FeaturePython)
  n = 0.271296
FEATURE [App::DocumentObjectGroupPython] N_element013  label="N_element : 0.121"  # scripted group (container) (typed FeaturePython)
  n = 0.121276
FEATURE [App::DocumentObjectGroupPython] O_element028  label="O_element : 0.578"  # scripted group (container) (typed FeaturePython)
  n = 0.578212
FEATURE [App::DocumentObjectGroupPython] G4_CELLULOSE_NITRATE  # scripted group (container) (typed FeaturePython)
  Dunit = g/cm3
  Dvalue = 1.49
  Group = -> [H_element023,C_element027,N_element013,O_element028]
  conduct = 2
  density = 1
  expand = 3
  formula = G4_CELLULOSE_NITRATE
  name = G4_CELLULOSE_NITRATE
  specific = 4
FEATURE [App::DocumentObjectGroupPython] H_element024  label="H_element : 0.108"  # scripted group (container) (typed FeaturePython)
  n = 0.107596
FEATURE [App::DocumentObjectGroupPython] N_element014  label="N_element : 0.001"  # scripted group (container) (typed FeaturePython)
  n = 0.0008
FEATURE [App::DocumentObjectGroupPython] O_element029  label="O_element : 0.875"  # scripted group (container) (typed FeaturePython)
  n = 0.874976
FEATURE [App::DocumentObjectGroupPython] S_element008  label="S_element : 0.015"  # scripted group (container) (typed FeaturePython)
  n = 0.014627
FEATURE [App::DocumentObjectGroupPython] Ce_element001  label="Ce_element : 0.002"  # scripted group (container) (typed FeaturePython)
  n = 0.002001
FEATURE [App::DocumentObjectGroupPython] G4_CERIC_SULFATE  # scripted group (container) (typed FeaturePython)
  Dunit = g/cm3
  Dvalue = 1.03
  Group = -> [H_element024,N_element014,O_element029,S_element008,Ce_element001]
  conduct = 2
  density = 1
  expand = 3
  formula = G4_CERIC_SULFATE
  name = G4_CERIC_SULFATE
  specific = 4
FEATURE [App::DocumentObjectGroupPython] Cs_element001  label="Cs_element : 1"  # scripted group (container) (typed FeaturePython)
  n = 1
  ref = Cs_element
FEATURE [App::DocumentObjectGroupPython] F_element006  label="F_element : 1"  # scripted group (container) (typed FeaturePython)
  n = 1
  ref = F_element
FEATURE [App::DocumentObjectGroupPython] G4_CESIUM_FLUORIDE  # scripted group (container) (typed FeaturePython)
  Dunit = g/cm3
  Dvalue = 4.115
  Group = -> [Cs_element001,F_element006]
  conduct = 2
  density = 1
  expand = 3
  formula = G4_CESIUM_FLUORIDE
  name = G4_CESIUM_FLUORIDE
  specific = 4
FEATURE [App::DocumentObjectGroupPython] Cs_element002  label="Cs_element : 002"  # scripted group (container) (typed FeaturePython)
  n = 1
  ref = Cs_element
FEATURE [App::DocumentObjectGroupPython] I_element001  label="I_element : 1"  # scripted group (container) (typed FeaturePython)
  n = 1
  ref = I_element
FEATURE [App::DocumentObjectGroupPython] G4_CESIUM_IODIDE  # scripted group (container) (typed FeaturePython)
  Dunit = g/cm3
  Dvalue = 4.51
  Group = -> [Cs_element002,I_element001]
  conduct = 2
  density = 1
  expand = 3
  formula = G4_CESIUM_IODIDE
  name = G4_CESIUM_IODIDE
  specific = 4
FEATURE [App::DocumentObjectGroupPython] C_element028  label="C_element : 013"  # scripted group (container) (typed FeaturePython)
  n = 6
  ref = C_element
FEATURE [App::DocumentObjectGroupPython] H_element025  label="H_element : 013"  # scripted group (container) (typed FeaturePython)
  n = 5
  ref = H_element
FEATURE [App::DocumentObjectGroupPython] Cl_element005  label="Cl_element : 1"  # scripted group (container) (typed FeaturePython)
  n = 1
  ref = Cl_element
FEATURE [App::DocumentObjectGroupPython] G4_CHLOROBENZENE  # scripted group (container) (typed FeaturePython)
  Dunit = g/cm3
  Dvalue = 1.1058
  Group = -> [C_element028,H_element025,Cl_element005]
  conduct = 2
  density = 1
  expand = 3
  formula = G4_CHLOROBENZENE
  name = G4_CHLOROBENZENE
  specific = 4
FEATURE [App::DocumentObjectGroupPython] C_element029  label="C_element : 014"  # scripted group (container) (typed FeaturePython)
  n = 1
  ref = C_element
FEATURE [App::DocumentObjectGroupPython] H_element026  label="H_element : 1"  # scripted group (container) (typed FeaturePython)
  n = 1
  ref = H_element
FEATURE [App::DocumentObjectGroupPython] Cl_element006  label="Cl_element : 3"  # scripted group (container) (typed FeaturePython)
  n = 3
  ref = Cl_element
FEATURE [App::DocumentObjectGroupPython] G4_CHLOROFORM  # scripted group (container) (typed FeaturePython)
  Dunit = g/cm3
  Dvalue = 1.4832
  Group = -> [C_element029,H_element026,Cl_element006]
  conduct = 2
  density = 1
  expand = 3
  formula = G4_CHLOROFORM
  name = G4_CHLOROFORM
  specific = 4
FEATURE [App::DocumentObjectGroupPython] H_element027  label="H_element : 0.010"  # scripted group (container) (typed FeaturePython)
  n = 0.01
FEATURE [App::DocumentObjectGroupPython] C_element030  label="C_element : 0.001"  # scripted group (container) (typed FeaturePython)
  n = 0.001
FEATURE [App::DocumentObjectGroupPython] O_element030  label="O_element : 0.529"  # scripted group (container) (typed FeaturePython)
  n = 0.529107
FEATURE [App::DocumentObjectGroupPython] Na_element005  label="Na_element : 0.016"  # scripted group (container) (typed FeaturePython)
  n = 0.016
FEATURE [App::DocumentObjectGroupPython] Mg_element003  label="Mg_element : 0.004"  # scripted group (container) (typed FeaturePython)
  n = 0.002
FEATURE [App::DocumentObjectGroupPython] Al_element002  label="Al_element : 0.034"  # scripted group (container) (typed FeaturePython)
  n = 0.033872
FEATURE [App::DocumentObjectGroupPython] Si_element002  label="Si_element : 0.337"  # scripted group (container) (typed FeaturePython)
  n = 0.337021
FEATURE [App::DocumentObjectGroupPython] K_element003  label="K_element : 0.013"  # scripted group (container) (typed FeaturePython)
  n = 0.013
FEATURE [App::DocumentObjectGroupPython] Ca_element010  label="Ca_element : 0.044"  # scripted group (container) (typed FeaturePython)
  n = 0.044
FEATURE [App::DocumentObjectGroupPython] Fe_element002  label="Fe_element : 0.014"  # scripted group (container) (typed FeaturePython)
  n = 0.014
FEATURE [App::DocumentObjectGroupPython] G4_CONCRETE  # scripted group (container) (typed FeaturePython)
  Dunit = g/cm3
  Dvalue = 2.3
  Group = -> [H_element027,C_element030,O_element030,Na_element005,Mg_element003,Al_element002,Si_element002,K_element003,Ca_element010,Fe_element002]
  conduct = 2
  density = 1
  expand = 3
  formula = G4_CONCRETE
  name = G4_CONCRETE
  specific = 4
FEATURE [App::DocumentObjectGroupPython] C_element031  label="C_element : 015"  # scripted group (container) (typed FeaturePython)
  n = 6
  ref = C_element
FEATURE [App::DocumentObjectGroupPython] H_element028  label="H_element : 12"  # scripted group (container) (typed FeaturePython)
  n = 12
  ref = H_element
FEATURE [App::DocumentObjectGroupPython] G4_CYCLOHEXANE  # scripted group (container) (typed FeaturePython)
  Dunit = g/cm3
  Dvalue = 0.779
  Group = -> [C_element031,H_element028]
  conduct = 2
  density = 1
  expand = 3
  formula = G4_CYCLOHEXANE
  name = G4_CYCLOHEXANE
  specific = 4
FEATURE [App::DocumentObjectGroupPython] C_element032  label="C_element : 016"  # scripted group (container) (typed FeaturePython)
  n = 6
  ref = C_element
FEATURE [App::DocumentObjectGroupPython] H_element029  label="H_element : 4"  # scripted group (container) (typed FeaturePython)
  n = 4
  ref = H_element
FEATURE [App::DocumentObjectGroupPython] Cl_element007  label="Cl_element : 2"  # scripted group (container) (typed FeaturePython)
  n = 2
  ref = Cl_element
FEATURE [App::DocumentObjectGroupPython] G4_1_2_DICHLOROBENZENE  label="G4_1.2-DICHLOROBENZENE"  # scripted group (container) (typed FeaturePython)
  Dunit = g/cm3
  Dvalue = 1.3048
  Group = -> [C_element032,H_element029,Cl_element007]
  conduct = 2
  density = 1
  expand = 3
  formula = G4_1.2-DICHLOROBENZENE
  name = G4_1.2-DICHLOROBENZENE
  specific = 4
FEATURE [App::DocumentObjectGroupPython] C_element033  label="C_element : 017"  # scripted group (container) (typed FeaturePython)
  n = 4
  ref = C_element
FEATURE [App::DocumentObjectGroupPython] H_element030  label="H_element : 8"  # scripted group (container) (typed FeaturePython)
  n = 8
  ref = H_element
FEATURE [App::DocumentObjectGroupPython] O_element031  label="O_element : 014"  # scripted group (container) (typed FeaturePython)
  n = 1
  ref = O_element
FEATURE [App::DocumentObjectGroupPython] Cl_element008  label="Cl_element : 005"  # scripted group (container) (typed FeaturePython)
  n = 2
  ref = Cl_element
FEATURE [App::DocumentObjectGroupPython] G4_DICHLORODIETHYL_ETHER  # scripted group (container) (typed FeaturePython)
  Dunit = g/cm3
  Dvalue = 1.2199
  Group = -> [C_element033,H_element030,O_element031,Cl_element008]
  conduct = 2
  density = 1
  expand = 3
  formula = G4_DICHLORODIETHYL_ETHER
  name = G4_DICHLORODIETHYL_ETHER
  specific = 4
FEATURE [App::DocumentObjectGroupPython] C_element034  label="C_element : 018"  # scripted group (container) (typed FeaturePython)
  n = 2
  ref = C_element
FEATURE [App::DocumentObjectGroupPython] H_element031  label="H_element : 014"  # scripted group (container) (typed FeaturePython)
  n = 4
  ref = H_element
FEATURE [App::DocumentObjectGroupPython] Cl_element009  label="Cl_element : 006"  # scripted group (container) (typed FeaturePython)
  n = 2
  ref = Cl_element
FEATURE [App::DocumentObjectGroupPython] G4_1_2_DICHLOROETHANE  label="G4_1.2-DICHLOROETHANE"  # scripted group (container) (typed FeaturePython)
  Dunit = g/cm3
  Dvalue = 1.2351
  Group = -> [C_element034,H_element031,Cl_element009]
  conduct = 2
  density = 1
  expand = 3
  formula = G4_1.2-DICHLOROETHANE
  name = G4_1.2-DICHLOROETHANE
  specific = 4
FEATURE [App::DocumentObjectGroupPython] C_element035  label="C_element : 019"  # scripted group (container) (typed FeaturePython)
  n = 4
  ref = C_element
FEATURE [App::DocumentObjectGroupPython] H_element032  label="H_element : 015"  # scripted group (container) (typed FeaturePython)
  n = 10
  ref = H_element
FEATURE [App::DocumentObjectGroupPython] O_element032  label="O_element : 015"  # scripted group (container) (typed FeaturePython)
  n = 1
  ref = O_element
FEATURE [App::DocumentObjectGroupPython] G4_DIETHYL_ETHER  # scripted group (container) (typed FeaturePython)
  Dunit = g/cm3
  Dvalue = 0.71378
  Group = -> [C_element035,H_element032,O_element032]
  conduct = 2
  density = 1
  expand = 3
  formula = G4_DIETHYL_ETHER
  name = G4_DIETHYL_ETHER
  specific = 4
FEATURE [App::DocumentObjectGroupPython] C_element036  label="C_element : 020"  # scripted group (container) (typed FeaturePython)
  n = 3
  ref = C_element
FEATURE [App::DocumentObjectGroupPython] H_element033  label="H_element : 016"  # scripted group (container) (typed FeaturePython)
  n = 7
  ref = H_element
FEATURE [App::DocumentObjectGroupPython] N_element015  label="N_element : 008"  # scripted group (container) (typed FeaturePython)
  n = 1
  ref = N_element
FEATURE [App::DocumentObjectGroupPython] O_element033  label="O_element : 016"  # scripted group (container) (typed FeaturePython)
  n = 1
  ref = O_element
FEATURE [App::DocumentObjectGroupPython] G4_N_N_DIMETHYL_FORMAMIDE  label="G4_N.N-DIMETHYL_FORMAMIDE"  # scripted group (container) (typed FeaturePython)
  Dunit = g/cm3
  Dvalue = 0.9487
  Group = -> [C_element036,H_element033,N_element015,O_element033]
  conduct = 2
  density = 1
  expand = 3
  formula = G4_N.N-DIMETHYL_FORMAMIDE
  name = G4_N.N-DIMETHYL_FORMAMIDE
  specific = 4
FEATURE [App::DocumentObjectGroupPython] C_element037  label="C_element : 021"  # scripted group (container) (typed FeaturePython)
  n = 2
  ref = C_element
FEATURE [App::DocumentObjectGroupPython] H_element034  label="H_element : 017"  # scripted group (container) (typed FeaturePython)
  n = 6
  ref = H_element
FEATURE [App::DocumentObjectGroupPython] O_element034  label="O_element : 017"  # scripted group (container) (typed FeaturePython)
  n = 1
  ref = O_element
FEATURE [App::DocumentObjectGroupPython] S_element009  label="S_element : 003"  # scripted group (container) (typed FeaturePython)
  n = 1
  ref = S_element
FEATURE [App::DocumentObjectGroupPython] G4_DIMETHYL_SULFOXIDE  # scripted group (container) (typed FeaturePython)
  Dunit = g/cm3
  Dvalue = 1.1014
  Group = -> [C_element037,H_element034,O_element034,S_element009]
  conduct = 2
  density = 1
  expand = 3
  formula = G4_DIMETHYL_SULFOXIDE
  name = G4_DIMETHYL_SULFOXIDE
  specific = 4
FEATURE [App::DocumentObjectGroupPython] C_element038  label="C_element : 022"  # scripted group (container) (typed FeaturePython)
  n = 2
  ref = C_element
FEATURE [App::DocumentObjectGroupPython] H_element035  label="H_element : 018"  # scripted group (container) (typed FeaturePython)
  n = 6
  ref = H_element
FEATURE [App::DocumentObjectGroupPython] G4_ETHANE  # scripted group (container) (typed FeaturePython)
  Dunit = g/cm3
  Dvalue = 0.00125324
  Group = -> [C_element038,H_element035]
  conduct = 2
  density = 1
  expand = 3
  formula = G4_ETHANE
  name = G4_ETHANE
  specific = 4
FEATURE [App::DocumentObjectGroupPython] C_element039  label="C_element : 023"  # scripted group (container) (typed FeaturePython)
  n = 2
  ref = C_element
FEATURE [App::DocumentObjectGroupPython] H_element036  label="H_element : 019"  # scripted group (container) (typed FeaturePython)
  n = 6
  ref = H_element
FEATURE [App::DocumentObjectGroupPython] O_element035  label="O_element : 018"  # scripted group (container) (typed FeaturePython)
  n = 1
  ref = O_element
FEATURE [App::DocumentObjectGroupPython] G4_ETHYL_ALCOHOL  # scripted group (container) (typed FeaturePython)
  Dunit = g/cm3
  Dvalue = 0.7893
  Group = -> [C_element039,H_element036,O_element035]
  conduct = 2
  density = 1
  expand = 3
  formula = G4_ETHYL_ALCOHOL
  name = G4_ETHYL_ALCOHOL
  specific = 4
FEATURE [App::DocumentObjectGroupPython] H_element037  label="H_element : 0.090"  # scripted group (container) (typed FeaturePython)
  n = 0.090027
FEATURE [App::DocumentObjectGroupPython] C_element040  label="C_element : 0.585"  # scripted group (container) (typed FeaturePython)
  n = 0.585182
FEATURE [App::DocumentObjectGroupPython] O_element036  label="O_element : 0.325"  # scripted group (container) (typed FeaturePython)
  n = 0.324791
FEATURE [App::DocumentObjectGroupPython] G4_ETHYL_CELLULOSE  # scripted group (container) (typed FeaturePython)
  Dunit = g/cm3
  Dvalue = 1.13
  Group = -> [H_element037,C_element040,O_element036]
  conduct = 2
  density = 1
  expand = 3
  formula = G4_ETHYL_CELLULOSE
  name = G4_ETHYL_CELLULOSE
  specific = 4
FEATURE [App::DocumentObjectGroupPython] C_element041  label="C_element : 024"  # scripted group (container) (typed FeaturePython)
  n = 2
  ref = C_element
FEATURE [App::DocumentObjectGroupPython] H_element038  label="H_element : 020"  # scripted group (container) (typed FeaturePython)
  n = 4
  ref = H_element
FEATURE [App::DocumentObjectGroupPython] G4_ETHYLENE  # scripted group (container) (typed FeaturePython)
  Dunit = g/cm3
  Dvalue = 0.00117497
  Group = -> [C_element041,H_element038]
  conduct = 2
  density = 1
  expand = 3
  formula = G4_ETHYLENE
  name = G4_ETHYLENE
  specific = 4
FEATURE [App::DocumentObjectGroupPython] H_element039  label="H_element : 0.096"  # scripted group (container) (typed FeaturePython)
  n = 0.096
FEATURE [App::DocumentObjectGroupPython] C_element042  label="C_element : 0.195"  # scripted group (container) (typed FeaturePython)
  n = 0.195
FEATURE [App::DocumentObjectGroupPython] N_element016  label="N_element : 0.057"  # scripted group (container) (typed FeaturePython)
  n = 0.057
FEATURE [App::DocumentObjectGroupPython] O_element037  label="O_element : 0.646"  # scripted group (container) (typed FeaturePython)
  n = 0.646
FEATURE [App::DocumentObjectGroupPython] Na_element006  label="Na_element : 0.017"  # scripted group (container) (typed FeaturePython)
  n = 0.001
FEATURE [App::DocumentObjectGroupPython] P_element005  label="P_element : 0.104"  # scripted group (container) (typed FeaturePython)
  n = 0.001
FEATURE [App::DocumentObjectGroupPython] S_element010  label="S_element : 0.016"  # scripted group (container) (typed FeaturePython)
  n = 0.003
FEATURE [App::DocumentObjectGroupPython] Cl_element010  label="Cl_element : 0.005"  # scripted group (container) (typed FeaturePython)
  n = 0.001
FEATURE [App::DocumentObjectGroupPython] G4_EYE_LENS_ICRP  # scripted group (container) (typed FeaturePython)
  Dunit = g/cm3
  Dvalue = 1.07
  Group = -> [H_element039,C_element042,N_element016,O_element037,Na_element006,P_element005,S_element010,Cl_element010]
  conduct = 2
  density = 1
  expand = 3
  formula = G4_EYE_LENS_ICRP
  name = G4_EYE_LENS_ICRP
  specific = 4
FEATURE [App::DocumentObjectGroupPython] Fe_element003  label="Fe_element : 2"  # scripted group (container) (typed FeaturePython)
  n = 2
  ref = Fe_element
FEATURE [App::DocumentObjectGroupPython] O_element038  label="O_element : 019"  # scripted group (container) (typed FeaturePython)
  n = 3
  ref = O_element
FEATURE [App::DocumentObjectGroupPython] G4_FERRIC_OXIDE  # scripted group (container) (typed FeaturePython)
  Dunit = g/cm3
  Dvalue = 5.2
  Group = -> [Fe_element003,O_element038]
  conduct = 2
  density = 1
  expand = 3
  formula = G4_FERRIC_OXIDE
  name = G4_FERRIC_OXIDE
  specific = 4
FEATURE [App::DocumentObjectGroupPython] Fe_element004  label="Fe_element : 1"  # scripted group (container) (typed FeaturePython)
  n = 1
  ref = Fe_element
FEATURE [App::DocumentObjectGroupPython] B_element003  label="B_element : 1"  # scripted group (container) (typed FeaturePython)
  n = 1
  ref = B_element
FEATURE [App::DocumentObjectGroupPython] G4_FERROBORIDE  # scripted group (container) (typed FeaturePython)
  Dunit = g/cm3
  Dvalue = 7.15
  Group = -> [Fe_element004,B_element003]
  conduct = 2
  density = 1
  expand = 3
  formula = G4_FERROBORIDE
  name = G4_FERROBORIDE
  specific = 4
FEATURE [App::DocumentObjectGroupPython] Fe_element005  label="Fe_element : 003"  # scripted group (container) (typed FeaturePython)
  n = 1
  ref = Fe_element
FEATURE [App::DocumentObjectGroupPython] O_element039  label="O_element : 020"  # scripted group (container) (typed FeaturePython)
  n = 1
  ref = O_element
FEATURE [App::DocumentObjectGroupPython] G4_FERROUS_OXIDE  # scripted group (container) (typed FeaturePython)
  Dunit = g/cm3
  Dvalue = 5.7
  Group = -> [Fe_element005,O_element039]
  conduct = 2
  density = 1
  expand = 3
  formula = G4_FERROUS_OXIDE
  name = G4_FERROUS_OXIDE
  specific = 4
FEATURE [App::DocumentObjectGroupPython] H_element040  label="H_element : 0.115"  # scripted group (container) (typed FeaturePython)
  n = 0.108259
FEATURE [App::DocumentObjectGroupPython] N_element017  label="N_element : 0.000"  # scripted group (container) (typed FeaturePython)
  n = 2.7e-05
FEATURE [App::DocumentObjectGroupPython] O_element040  label="O_element : 0.879"  # scripted group (container) (typed FeaturePython)
  n = 0.878636
FEATURE [App::DocumentObjectGroupPython] Na_element007  label="Na_element : 0.000"  # scripted group (container) (typed FeaturePython)
  n = 2.2e-05
FEATURE [App::DocumentObjectGroupPython] S_element011  label="S_element : 0.013"  # scripted group (container) (typed FeaturePython)
  n = 0.012968
FEATURE [App::DocumentObjectGroupPython] Cl_element011  label="Cl_element : 0.000"  # scripted group (container) (typed FeaturePython)
  n = 3.4e-05
FEATURE [App::DocumentObjectGroupPython] Fe_element006  label="Fe_element : 0.000"  # scripted group (container) (typed FeaturePython)
  n = 5.4e-05
FEATURE [App::DocumentObjectGroupPython] G4_FERROUS_SULFATE  # scripted group (container) (typed FeaturePython)
  Dunit = g/cm3
  Dvalue = 1.024
  Group = -> [H_element040,N_element017,O_element040,Na_element007,S_element011,Cl_element011,Fe_element006]
  conduct = 2
  density = 1
  expand = 3
  formula = G4_FERROUS_SULFATE
  name = G4_FERROUS_SULFATE
  specific = 4
FEATURE [App::DocumentObjectGroupPython] C_element043  label="C_element : 0.099"  # scripted group (container) (typed FeaturePython)
  n = 0.099335
FEATURE [App::DocumentObjectGroupPython] F_element007  label="F_element : 0.314"  # scripted group (container) (typed FeaturePython)
  n = 0.314247
FEATURE [App::DocumentObjectGroupPython] Cl_element012  label="Cl_element : 0.586"  # scripted group (container) (typed FeaturePython)
  n = 0.586418
FEATURE [App::DocumentObjectGroupPython] G4_FREON_12  label="G4_FREON-12"  # scripted group (container) (typed FeaturePython)
  Dunit = g/cm3
  Dvalue = 1.12
  Group = -> [C_element043,F_element007,Cl_element012]
  conduct = 2
  density = 1
  expand = 3
  formula = G4_FREON-12
  name = G4_FREON-12
  specific = 4
FEATURE [App::DocumentObjectGroupPython] C_element044  label="C_element : 0.057"  # scripted group (container) (typed FeaturePython)
  n = 0.057245
FEATURE [App::DocumentObjectGroupPython] F_element008  label="F_element : 0.181"  # scripted group (container) (typed FeaturePython)
  n = 0.181096
FEATURE [App::DocumentObjectGroupPython] Br_element001  label="Br_element : 0.762"  # scripted group (container) (typed FeaturePython)
  n = 0.761659
FEATURE [App::DocumentObjectGroupPython] G4_FREON_12B2  label="G4_FREON-12B2"  # scripted group (container) (typed FeaturePython)
  Dunit = g/cm3
  Dvalue = 1.8
  Group = -> [C_element044,F_element008,Br_element001]
  conduct = 2
  density = 1
  expand = 3
  formula = G4_FREON-12B2
  name = G4_FREON-12B2
  specific = 4
FEATURE [App::DocumentObjectGroupPython] C_element045  label="C_element : 0.115"  # scripted group (container) (typed FeaturePython)
  n = 0.114983
FEATURE [App::DocumentObjectGroupPython] F_element009  label="F_element : 0.546"  # scripted group (container) (typed FeaturePython)
  n = 0.545621
FEATURE [App::DocumentObjectGroupPython] Cl_element013  label="Cl_element : 0.339"  # scripted group (container) (typed FeaturePython)
  n = 0.339396
FEATURE [App::DocumentObjectGroupPython] G4_FREON_13  label="G4_FREON-13"  # scripted group (container) (typed FeaturePython)
  Dunit = g/cm3
  Dvalue = 0.95
  Group = -> [C_element045,F_element009,Cl_element013]
  conduct = 2
  density = 1
  expand = 3
  formula = G4_FREON-13
  name = G4_FREON-13
  specific = 4
FEATURE [App::DocumentObjectGroupPython] C_element046  label="C_element : 025"  # scripted group (container) (typed FeaturePython)
  n = 1
  ref = C_element
FEATURE [App::DocumentObjectGroupPython] F_element010  label="F_element : 3"  # scripted group (container) (typed FeaturePython)
  n = 3
  ref = F_element
FEATURE [App::DocumentObjectGroupPython] Br_element002  label="Br_element : 1"  # scripted group (container) (typed FeaturePython)
  n = 1
  ref = Br_element
FEATURE [App::DocumentObjectGroupPython] G4_FREON_13B1  label="G4_FREON-13B1"  # scripted group (container) (typed FeaturePython)
  Dunit = g/cm3
  Dvalue = 1.5
  Group = -> [C_element046,F_element010,Br_element002]
  conduct = 2
  density = 1
  expand = 3
  formula = G4_FREON-13B1
  name = G4_FREON-13B1
  specific = 4
FEATURE [App::DocumentObjectGroupPython] C_element047  label="C_element : 0.061"  # scripted group (container) (typed FeaturePython)
  n = 0.061309
FEATURE [App::DocumentObjectGroupPython] F_element011  label="F_element : 0.291"  # scripted group (container) (typed FeaturePython)
  n = 0.290924
FEATURE [App::DocumentObjectGroupPython] I_element002  label="I_element : 0.648"  # scripted group (container) (typed FeaturePython)
  n = 0.647767
FEATURE [App::DocumentObjectGroupPython] G4_FREON_13I1  label="G4_FREON-13I1"  # scripted group (container) (typed FeaturePython)
  Dunit = g/cm3
  Dvalue = 1.8
  Group = -> [C_element047,F_element011,I_element002]
  conduct = 2
  density = 1
  expand = 3
  formula = G4_FREON-13I1
  name = G4_FREON-13I1
  specific = 4
FEATURE [App::DocumentObjectGroupPython] Gd_element001  label="Gd_element : 2"  # scripted group (container) (typed FeaturePython)
  n = 2
  ref = Gd_element
FEATURE [App::DocumentObjectGroupPython] O_element041  label="O_element : 021"  # scripted group (container) (typed FeaturePython)
  n = 2
  ref = O_element
FEATURE [App::DocumentObjectGroupPython] S_element012  label="S_element : 004"  # scripted group (container) (typed FeaturePython)
  n = 1
  ref = S_element
FEATURE [App::DocumentObjectGroupPython] G4_GADOLINIUM_OXYSULFIDE  # scripted group (container) (typed FeaturePython)
  Dunit = g/cm3
  Dvalue = 7.44
  Group = -> [Gd_element001,O_element041,S_element012]
  conduct = 2
  density = 1
  expand = 3
  formula = G4_GADOLINIUM_OXYSULFIDE
  name = G4_GADOLINIUM_OXYSULFIDE
  specific = 4
FEATURE [App::DocumentObjectGroupPython] Ga_element001  label="Ga_element : 1"  # scripted group (container) (typed FeaturePython)
  n = 1
  ref = Ga_element
FEATURE [App::DocumentObjectGroupPython] As_element001  label="As_element : 1"  # scripted group (container) (typed FeaturePython)
  n = 1
  ref = As_element
FEATURE [App::DocumentObjectGroupPython] G4_GALLIUM_ARSENIDE  # scripted group (container) (typed FeaturePython)
  Dunit = g/cm3
  Dvalue = 5.31
  Group = -> [Ga_element001,As_element001]
  conduct = 2
  density = 1
  expand = 3
  formula = G4_GALLIUM_ARSENIDE
  name = G4_GALLIUM_ARSENIDE
  specific = 4
FEATURE [App::DocumentObjectGroupPython] H_element041  label="H_element : 0.081"  # scripted group (container) (typed FeaturePython)
  n = 0.08118
FEATURE [App::DocumentObjectGroupPython] C_element048  label="C_element : 0.416"  # scripted group (container) (typed FeaturePython)
  n = 0.41606
FEATURE [App::DocumentObjectGroupPython] N_element018  label="N_element : 0.111"  # scripted group (container) (typed FeaturePython)
  n = 0.11124
FEATURE [App::DocumentObjectGroupPython] O_element042  label="O_element : 0.381"  # scripted group (container) (typed FeaturePython)
  n = 0.38064
FEATURE [App::DocumentObjectGroupPython] S_element013  label="S_element : 0.011"  # scripted group (container) (typed FeaturePython)
  n = 0.01088
FEATURE [App::DocumentObjectGroupPython] G4_GEL_PHOTO_EMULSION  # scripted group (container) (typed FeaturePython)
  Dunit = g/cm3
  Dvalue = 1.2914
  Group = -> [H_element041,C_element048,N_element018,O_element042,S_element013]
  conduct = 2
  density = 1
  expand = 3
  formula = G4_GEL_PHOTO_EMULSION
  name = G4_GEL_PHOTO_EMULSION
  specific = 4
FEATURE [App::DocumentObjectGroupPython] B_element004  label="B_element : 0.040"  # scripted group (container) (typed FeaturePython)
  n = 0.0400639
FEATURE [App::DocumentObjectGroupPython] O_element043  label="O_element : 0.540"  # scripted group (container) (typed FeaturePython)
  n = 0.539561
FEATURE [App::DocumentObjectGroupPython] Na_element008  label="Na_element : 0.028"  # scripted group (container) (typed FeaturePython)
  n = 0.0281909
FEATURE [App::DocumentObjectGroupPython] Al_element003  label="Al_element : 0.012"  # scripted group (container) (typed FeaturePython)
  n = 0.011644
FEATURE [App::DocumentObjectGroupPython] Si_element003  label="Si_element : 0.377"  # scripted group (container) (typed FeaturePython)
  n = 0.377219
FEATURE [App::DocumentObjectGroupPython] K_element004  label="K_element : 0.014"  # scripted group (container) (typed FeaturePython)
  n = 0.00332099
FEATURE [App::DocumentObjectGroupPython] G4_Pyrex_Glass  # scripted group (container) (typed FeaturePython)
  Dunit = g/cm3
  Dvalue = 2.23
  Group = -> [B_element004,O_element043,Na_element008,Al_element003,Si_element003,K_element004]
  conduct = 2
  density = 1
  expand = 3
  formula = G4_Pyrex_Glass
  name = G4_Pyrex_Glass
  specific = 4
FEATURE [App::DocumentObjectGroupPython] O_element044  label="O_element : 0.156"  # scripted group (container) (typed FeaturePython)
  n = 0.156453
FEATURE [App::DocumentObjectGroupPython] Si_element004  label="Si_element : 0.081"  # scripted group (container) (typed FeaturePython)
  n = 0.080866
FEATURE [App::DocumentObjectGroupPython] Ti_element001  label="Ti_element : 0.008"  # scripted group (container) (typed FeaturePython)
  n = 0.008092
FEATURE [App::DocumentObjectGroupPython] As_element002  label="As_element : 0.003"  # scripted group (container) (typed FeaturePython)
  n = 0.002651
FEATURE [App::DocumentObjectGroupPython] Pb_element001  label="Pb_element : 0.752"  # scripted group (container) (typed FeaturePython)
  n = 0.751938
FEATURE [App::DocumentObjectGroupPython] G4_GLASS_LEAD  # scripted group (container) (typed FeaturePython)
  Dunit = g/cm3
  Dvalue = 6.22
  Group = -> [O_element044,Si_element004,Ti_element001,As_element002,Pb_element001]
  conduct = 2
  density = 1
  expand = 3
  formula = G4_GLASS_LEAD
  name = G4_GLASS_LEAD
  specific = 4
FEATURE [App::DocumentObjectGroupPython] O_element045  label="O_element : 0.460"  # scripted group (container) (typed FeaturePython)
  n = 0.4598
FEATURE [App::DocumentObjectGroupPython] Na_element009  label="Na_element : 0.096"  # scripted group (container) (typed FeaturePython)
  n = 0.0964411
FEATURE [App::DocumentObjectGroupPython] Si_element005  label="Si_element : 0.378"  # scripted group (container) (typed FeaturePython)
  n = 0.336553
FEATURE [App::DocumentObjectGroupPython] Ca_element011  label="Ca_element : 0.107"  # scripted group (container) (typed FeaturePython)
  n = 0.107205
FEATURE [App::DocumentObjectGroupPython] G4_GLASS_PLATE  # scripted group (container) (typed FeaturePython)
  Dunit = g/cm3
  Dvalue = 2.4
  Group = -> [O_element045,Na_element009,Si_element005,Ca_element011]
  conduct = 2
  density = 1
  expand = 3
  formula = G4_GLASS_PLATE
  name = G4_GLASS_PLATE
  specific = 4
FEATURE [App::DocumentObjectGroupPython] C_element049  label="C_element : 026"  # scripted group (container) (typed FeaturePython)
  n = 5
  ref = C_element
FEATURE [App::DocumentObjectGroupPython] H_element042  label="H_element : 021"  # scripted group (container) (typed FeaturePython)
  n = 10
  ref = H_element
FEATURE [App::DocumentObjectGroupPython] N_element019  label="N_element : 2"  # scripted group (container) (typed FeaturePython)
  n = 2
  ref = N_element
FEATURE [App::DocumentObjectGroupPython] O_element046  label="O_element : 022"  # scripted group (container) (typed FeaturePython)
  n = 3
  ref = O_element
FEATURE [App::DocumentObjectGroupPython] G4_GLUTAMINE  # scripted group (container) (typed FeaturePython)
  Dunit = g/cm3
  Dvalue = 1.46
  Group = -> [C_element049,H_element042,N_element019,O_element046]
  conduct = 2
  density = 1
  expand = 3
  formula = G4_GLUTAMINE
  name = G4_GLUTAMINE
  specific = 4
FEATURE [App::DocumentObjectGroupPython] C_element050  label="C_element : 027"  # scripted group (container) (typed FeaturePython)
  n = 3
  ref = C_element
FEATURE [App::DocumentObjectGroupPython] H_element043  label="H_element : 022"  # scripted group (container) (typed FeaturePython)
  n = 8
  ref = H_element
FEATURE [App::DocumentObjectGroupPython] O_element047  label="O_element : 023"  # scripted group (container) (typed FeaturePython)
  n = 3
  ref = O_element
FEATURE [App::DocumentObjectGroupPython] G4_GLYCEROL  # scripted group (container) (typed FeaturePython)
  Dunit = g/cm3
  Dvalue = 1.2613
  Group = -> [C_element050,H_element043,O_element047]
  conduct = 2
  density = 1
  expand = 3
  formula = G4_GLYCEROL
  name = G4_GLYCEROL
  specific = 4
FEATURE [App::DocumentObjectGroupPython] C_element051  label="C_element : 028"  # scripted group (container) (typed FeaturePython)
  n = 5
  ref = C_element
FEATURE [App::DocumentObjectGroupPython] H_element044  label="H_element : 023"  # scripted group (container) (typed FeaturePython)
  n = 5
  ref = H_element
FEATURE [App::DocumentObjectGroupPython] N_element020  label="N_element : 009"  # scripted group (container) (typed FeaturePython)
  n = 5
  ref = N_element
FEATURE [App::DocumentObjectGroupPython] O_element048  label="O_element : 024"  # scripted group (container) (typed FeaturePython)
  n = 1
  ref = O_element
FEATURE [App::DocumentObjectGroupPython] G4_GUANINE  # scripted group (container) (typed FeaturePython)
  Dunit = g/cm3
  Dvalue = 2.2
  Group = -> [C_element051,H_element044,N_element020,O_element048]
  conduct = 2
  density = 1
  expand = 3
  formula = G4_GUANINE
  name = G4_GUANINE
  specific = 4
FEATURE [App::DocumentObjectGroupPython] Ca_element012  label="Ca_element : 006"  # scripted group (container) (typed FeaturePython)
  n = 1
  ref = Ca_element
FEATURE [App::DocumentObjectGroupPython] S_element014  label="S_element : 005"  # scripted group (container) (typed FeaturePython)
  n = 1
  ref = S_element
FEATURE [App::DocumentObjectGroupPython] O_element049  label="O_element : 6"  # scripted group (container) (typed FeaturePython)
  n = 6
  ref = O_element
FEATURE [App::DocumentObjectGroupPython] H_element045  label="H_element : 024"  # scripted group (container) (typed FeaturePython)
  n = 4
  ref = H_element
FEATURE [App::DocumentObjectGroupPython] G4_GYPSUM  # scripted group (container) (typed FeaturePython)
  Dunit = g/cm3
  Dvalue = 2.32
  Group = -> [Ca_element012,S_element014,O_element049,H_element045]
  conduct = 2
  density = 1
  expand = 3
  formula = G4_GYPSUM
  name = G4_GYPSUM
  specific = 4
FEATURE [App::DocumentObjectGroupPython] C_element052  label="C_element : 7"  # scripted group (container) (typed FeaturePython)
  n = 7
  ref = C_element
FEATURE [App::DocumentObjectGroupPython] H_element046  label="H_element : 16"  # scripted group (container) (typed FeaturePython)
  n = 16
  ref = H_element
FEATURE [App::DocumentObjectGroupPython] G4_N_HEPTANE  label="G4_N-HEPTANE"  # scripted group (container) (typed FeaturePython)
  Dunit = g/cm3
  Dvalue = 0.68376
  Group = -> [C_element052,H_element046]
  conduct = 2
  density = 1
  expand = 3
  formula = G4_N-HEPTANE
  name = G4_N-HEPTANE
  specific = 4
FEATURE [App::DocumentObjectGroupPython] C_element053  label="C_element : 029"  # scripted group (container) (typed FeaturePython)
  n = 6
  ref = C_element
FEATURE [App::DocumentObjectGroupPython] H_element047  label="H_element : 14"  # scripted group (container) (typed FeaturePython)
  n = 14
  ref = H_element
FEATURE [App::DocumentObjectGroupPython] G4_N_HEXANE  label="G4_N-HEXANE"  # scripted group (container) (typed FeaturePython)
  Dunit = g/cm3
  Dvalue = 0.6603
  Group = -> [C_element053,H_element047]
  conduct = 2
  density = 1
  expand = 3
  formula = G4_N-HEXANE
  name = G4_N-HEXANE
  specific = 4
FEATURE [App::DocumentObjectGroupPython] C_element054  label="C_element : 22"  # scripted group (container) (typed FeaturePython)
  n = 22
  ref = C_element
FEATURE [App::DocumentObjectGroupPython] H_element048  label="H_element : 025"  # scripted group (container) (typed FeaturePython)
  n = 10
  ref = H_element
FEATURE [App::DocumentObjectGroupPython] N_element021  label="N_element : 010"  # scripted group (container) (typed FeaturePython)
  n = 2
  ref = N_element
FEATURE [App::DocumentObjectGroupPython] O_element050  label="O_element : 025"  # scripted group (container) (typed FeaturePython)
  n = 5
  ref = O_element
FEATURE [App::DocumentObjectGroupPython] G4_KAPTON  # scripted group (container) (typed FeaturePython)
  Dunit = g/cm3
  Dvalue = 1.42
  Group = -> [C_element054,H_element048,N_element021,O_element050]
  conduct = 2
  density = 1
  expand = 3
  formula = G4_KAPTON
  name = G4_KAPTON
  specific = 4
FEATURE [App::DocumentObjectGroupPython] La_element001  label="La_element : 1"  # scripted group (container) (typed FeaturePython)
  n = 1
  ref = La_element
FEATURE [App::DocumentObjectGroupPython] Br_element003  label="Br_element : 002"  # scripted group (container) (typed FeaturePython)
  n = 1
  ref = Br_element
FEATURE [App::DocumentObjectGroupPython] O_element051  label="O_element : 026"  # scripted group (container) (typed FeaturePython)
  n = 1
  ref = O_element
FEATURE [App::DocumentObjectGroupPython] G4_LANTHANUM_OXYBROMIDE  # scripted group (container) (typed FeaturePython)
  Dunit = g/cm3
  Dvalue = 6.28
  Group = -> [La_element001,Br_element003,O_element051]
  conduct = 2
  density = 1
  expand = 3
  formula = G4_LANTHANUM_OXYBROMIDE
  name = G4_LANTHANUM_OXYBROMIDE
  specific = 4
FEATURE [App::DocumentObjectGroupPython] La_element002  label="La_element : 2"  # scripted group (container) (typed FeaturePython)
  n = 2
  ref = La_element
FEATURE [App::DocumentObjectGroupPython] O_element052  label="O_element : 027"  # scripted group (container) (typed FeaturePython)
  n = 2
  ref = O_element
FEATURE [App::DocumentObjectGroupPython] S_element015  label="S_element : 006"  # scripted group (container) (typed FeaturePython)
  n = 1
  ref = S_element
FEATURE [App::DocumentObjectGroupPython] G4_LANTHANUM_OXYSULFIDE  # scripted group (container) (typed FeaturePython)
  Dunit = g/cm3
  Dvalue = 5.86
  Group = -> [La_element002,O_element052,S_element015]
  conduct = 2
  density = 1
  expand = 3
  formula = G4_LANTHANUM_OXYSULFIDE
  name = G4_LANTHANUM_OXYSULFIDE
  specific = 4
FEATURE [App::DocumentObjectGroupPython] O_element053  label="O_element : 0.072"  # scripted group (container) (typed FeaturePython)
  n = 0.071682
FEATURE [App::DocumentObjectGroupPython] Pb_element002  label="Pb_element : 0.928"  # scripted group (container) (typed FeaturePython)
  n = 0.928318
FEATURE [App::DocumentObjectGroupPython] G4_LEAD_OXIDE  # scripted group (container) (typed FeaturePython)
  Dunit = g/cm3
  Dvalue = 9.53
  Group = -> [O_element053,Pb_element002]
  conduct = 2
  density = 1
  expand = 3
  formula = G4_LEAD_OXIDE
  name = G4_LEAD_OXIDE
  specific = 4
FEATURE [App::DocumentObjectGroupPython] Li_element001  label="Li_element : 1"  # scripted group (container) (typed FeaturePython)
  n = 1
  ref = Li_element
FEATURE [App::DocumentObjectGroupPython] N_element022  label="N_element : 011"  # scripted group (container) (typed FeaturePython)
  n = 1
  ref = N_element
FEATURE [App::DocumentObjectGroupPython] H_element049  label="H_element : 026"  # scripted group (container) (typed FeaturePython)
  n = 2
  ref = H_element
FEATURE [App::DocumentObjectGroupPython] G4_LITHIUM_AMIDE  # scripted group (container) (typed FeaturePython)
  Dunit = g/cm3
  Dvalue = 1.178
  Group = -> [Li_element001,N_element022,H_element049]
  conduct = 2
  density = 1
  expand = 3
  formula = G4_LITHIUM_AMIDE
  name = G4_LITHIUM_AMIDE
  specific = 4
FEATURE [App::DocumentObjectGroupPython] Li_element002  label="Li_element : 2"  # scripted group (container) (typed FeaturePython)
  n = 2
  ref = Li_element
FEATURE [App::DocumentObjectGroupPython] C_element055  label="C_element : 030"  # scripted group (container) (typed FeaturePython)
  n = 1
  ref = C_element
FEATURE [App::DocumentObjectGroupPython] O_element054  label="O_element : 028"  # scripted group (container) (typed FeaturePython)
  n = 3
  ref = O_element
FEATURE [App::DocumentObjectGroupPython] G4_LITHIUM_CARBONATE  # scripted group (container) (typed FeaturePython)
  Dunit = g/cm3
  Dvalue = 2.11
  Group = -> [Li_element002,C_element055,O_element054]
  conduct = 2
  density = 1
  expand = 3
  formula = G4_LITHIUM_CARBONATE
  name = G4_LITHIUM_CARBONATE
  specific = 4
FEATURE [App::DocumentObjectGroupPython] Li_element003  label="Li_element : 003"  # scripted group (container) (typed FeaturePython)
  n = 1
  ref = Li_element
FEATURE [App::DocumentObjectGroupPython] F_element012  label="F_element : 004"  # scripted group (container) (typed FeaturePython)
  n = 1
  ref = F_element
FEATURE [App::DocumentObjectGroupPython] G4_LITHIUM_FLUORIDE  # scripted group (container) (typed FeaturePython)
  Dunit = g/cm3
  Dvalue = 2.635
  Group = -> [Li_element003,F_element012]
  conduct = 2
  density = 1
  expand = 3
  formula = G4_LITHIUM_FLUORIDE
  name = G4_LITHIUM_FLUORIDE
  specific = 4
FEATURE [App::DocumentObjectGroupPython] Li_element004  label="Li_element : 004"  # scripted group (container) (typed FeaturePython)
  n = 1
  ref = Li_element
FEATURE [App::DocumentObjectGroupPython] H_element050  label="H_element : 027"  # scripted group (container) (typed FeaturePython)
  n = 1
  ref = H_element
FEATURE [App::DocumentObjectGroupPython] G4_LITHIUM_HYDRIDE  # scripted group (container) (typed FeaturePython)
  Dunit = g/cm3
  Dvalue = 0.82
  Group = -> [Li_element004,H_element050]
  conduct = 2
  density = 1
  expand = 3
  formula = G4_LITHIUM_HYDRIDE
  name = G4_LITHIUM_HYDRIDE
  specific = 4
FEATURE [App::DocumentObjectGroupPython] Li_element005  label="Li_element : 005"  # scripted group (container) (typed FeaturePython)
  n = 1
  ref = Li_element
FEATURE [App::DocumentObjectGroupPython] I_element003  label="I_element : 002"  # scripted group (container) (typed FeaturePython)
  n = 1
  ref = I_element
FEATURE [App::DocumentObjectGroupPython] G4_LITHIUM_IODIDE  # scripted group (container) (typed FeaturePython)
  Dunit = g/cm3
  Dvalue = 3.494
  Group = -> [Li_element005,I_element003]
  conduct = 2
  density = 1
  expand = 3
  formula = G4_LITHIUM_IODIDE
  name = G4_LITHIUM_IODIDE
  specific = 4
FEATURE [App::DocumentObjectGroupPython] Li_element006  label="Li_element : 006"  # scripted group (container) (typed FeaturePython)
  n = 2
  ref = Li_element
FEATURE [App::DocumentObjectGroupPython] O_element055  label="O_element : 029"  # scripted group (container) (typed FeaturePython)
  n = 1
  ref = O_element
FEATURE [App::DocumentObjectGroupPython] G4_LITHIUM_OXIDE  # scripted group (container) (typed FeaturePython)
  Dunit = g/cm3
  Dvalue = 2.013
  Group = -> [Li_element006,O_element055]
  conduct = 2
  density = 1
  expand = 3
  formula = G4_LITHIUM_OXIDE
  name = G4_LITHIUM_OXIDE
  specific = 4
FEATURE [App::DocumentObjectGroupPython] Li_element007  label="Li_element : 007"  # scripted group (container) (typed FeaturePython)
  n = 2
  ref = Li_element
FEATURE [App::DocumentObjectGroupPython] B_element005  label="B_element : 005"  # scripted group (container) (typed FeaturePython)
  n = 4
  ref = B_element
FEATURE [App::DocumentObjectGroupPython] O_element056  label="O_element : 7"  # scripted group (container) (typed FeaturePython)
  n = 7
  ref = O_element
FEATURE [App::DocumentObjectGroupPython] G4_LITHIUM_TETRABORATE  # scripted group (container) (typed FeaturePython)
  Dunit = g/cm3
  Dvalue = 2.44
  Group = -> [Li_element007,B_element005,O_element056]
  conduct = 2
  density = 1
  expand = 3
  formula = G4_LITHIUM_TETRABORATE
  name = G4_LITHIUM_TETRABORATE
  specific = 4
FEATURE [App::DocumentObjectGroupPython] H_element051  label="H_element : 0.105"  # scripted group (container) (typed FeaturePython)
  n = 0.105
FEATURE [App::DocumentObjectGroupPython] C_element056  label="C_element : 0.083"  # scripted group (container) (typed FeaturePython)
  n = 0.083
FEATURE [App::DocumentObjectGroupPython] N_element023  label="N_element : 0.023"  # scripted group (container) (typed FeaturePython)
  n = 0.023
FEATURE [App::DocumentObjectGroupPython] O_element057  label="O_element : 0.779"  # scripted group (container) (typed FeaturePython)
  n = 0.779
FEATURE [App::DocumentObjectGroupPython] Na_element010  label="Na_element : 0.097"  # scripted group (container) (typed FeaturePython)
  n = 0.002
FEATURE [App::DocumentObjectGroupPython] P_element006  label="P_element : 0.105"  # scripted group (container) (typed FeaturePython)
  n = 0.001
FEATURE [App::DocumentObjectGroupPython] S_element016  label="S_element : 0.017"  # scripted group (container) (typed FeaturePython)
  n = 0.002
FEATURE [App::DocumentObjectGroupPython] Cl_element014  label="Cl_element : 0.587"  # scripted group (container) (typed FeaturePython)
  n = 0.003
FEATURE [App::DocumentObjectGroupPython] K_element005  label="K_element : 0.015"  # scripted group (container) (typed FeaturePython)
  n = 0.002
FEATURE [App::DocumentObjectGroupPython] G4_LUNG_ICRP  # scripted group (container) (typed FeaturePython)
  Dunit = g/cm3
  Dvalue = 1.04
  Group = -> [H_element051,C_element056,N_element023,O_element057,Na_element010,P_element006,S_element016,Cl_element014,K_element005]
  conduct = 2
  density = 1
  expand = 3
  formula = G4_LUNG_ICRP
  name = G4_LUNG_ICRP
  specific = 4
FEATURE [App::DocumentObjectGroupPython] H_element052  label="H_element : 0.116"  # scripted group (container) (typed FeaturePython)
  n = 0.114318
FEATURE [App::DocumentObjectGroupPython] C_element057  label="C_element : 0.656"  # scripted group (container) (typed FeaturePython)
  n = 0.655824
FEATURE [App::DocumentObjectGroupPython] O_element058  label="O_element : 0.092"  # scripted group (container) (typed FeaturePython)
  n = 0.0921831
FEATURE [App::DocumentObjectGroupPython] Mg_element004  label="Mg_element : 0.135"  # scripted group (container) (typed FeaturePython)
  n = 0.134792
FEATURE [App::DocumentObjectGroupPython] Ca_element013  label="Ca_element : 0.003"  # scripted group (container) (typed FeaturePython)
  n = 0.002883
FEATURE [App::DocumentObjectGroupPython] G4_M3_WAX  # scripted group (container) (typed FeaturePython)
  Dunit = g/cm3
  Dvalue = 1.05
  Group = -> [H_element052,C_element057,O_element058,Mg_element004,Ca_element013]
  conduct = 2
  density = 1
  expand = 3
  formula = G4_M3_WAX
  name = G4_M3_WAX
  specific = 4
FEATURE [App::DocumentObjectGroupPython] Mg_element005  label="Mg_element : 1"  # scripted group (container) (typed FeaturePython)
  n = 1
  ref = Mg_element
FEATURE [App::DocumentObjectGroupPython] C_element058  label="C_element : 031"  # scripted group (container) (typed FeaturePython)
  n = 1
  ref = C_element
FEATURE [App::DocumentObjectGroupPython] O_element059  label="O_element : 030"  # scripted group (container) (typed FeaturePython)
  n = 3
  ref = O_element
FEATURE [App::DocumentObjectGroupPython] G4_MAGNESIUM_CARBONATE  # scripted group (container) (typed FeaturePython)
  Dunit = g/cm3
  Dvalue = 2.958
  Group = -> [Mg_element005,C_element058,O_element059]
  conduct = 2
  density = 1
  expand = 3
  formula = G4_MAGNESIUM_CARBONATE
  name = G4_MAGNESIUM_CARBONATE
  specific = 4
FEATURE [App::DocumentObjectGroupPython] Mg_element006  label="Mg_element : 002"  # scripted group (container) (typed FeaturePython)
  n = 1
  ref = Mg_element
FEATURE [App::DocumentObjectGroupPython] F_element013  label="F_element : 005"  # scripted group (container) (typed FeaturePython)
  n = 2
  ref = F_element
FEATURE [App::DocumentObjectGroupPython] G4_MAGNESIUM_FLUORIDE  # scripted group (container) (typed FeaturePython)
  Dunit = g/cm3
  Dvalue = 3
  Group = -> [Mg_element006,F_element013]
  conduct = 2
  density = 1
  expand = 3
  formula = G4_MAGNESIUM_FLUORIDE
  name = G4_MAGNESIUM_FLUORIDE
  specific = 4
FEATURE [App::DocumentObjectGroupPython] Mg_element007  label="Mg_element : 003"  # scripted group (container) (typed FeaturePython)
  n = 1
  ref = Mg_element
FEATURE [App::DocumentObjectGroupPython] O_element060  label="O_element : 031"  # scripted group (container) (typed FeaturePython)
  n = 1
  ref = O_element
FEATURE [App::DocumentObjectGroupPython] G4_MAGNESIUM_OXIDE  # scripted group (container) (typed FeaturePython)
  Dunit = g/cm3
  Dvalue = 3.58
  Group = -> [Mg_element007,O_element060]
  conduct = 2
  density = 1
  expand = 3
  formula = G4_MAGNESIUM_OXIDE
  name = G4_MAGNESIUM_OXIDE
  specific = 4
FEATURE [App::DocumentObjectGroupPython] Mg_element008  label="Mg_element : 004"  # scripted group (container) (typed FeaturePython)
  n = 1
  ref = Mg_element
FEATURE [App::DocumentObjectGroupPython] B_element006  label="B_element : 006"  # scripted group (container) (typed FeaturePython)
  n = 4
  ref = B_element
FEATURE [App::DocumentObjectGroupPython] O_element061  label="O_element : 032"  # scripted group (container) (typed FeaturePython)
  n = 7
  ref = O_element
FEATURE [App::DocumentObjectGroupPython] G4_MAGNESIUM_TETRABORATE  # scripted group (container) (typed FeaturePython)
  Dunit = g/cm3
  Dvalue = 2.53
  Group = -> [Mg_element008,B_element006,O_element061]
  conduct = 2
  density = 1
  expand = 3
  formula = G4_MAGNESIUM_TETRABORATE
  name = G4_MAGNESIUM_TETRABORATE
  specific = 4
FEATURE [App::DocumentObjectGroupPython] Hg_element001  label="Hg_element : 1"  # scripted group (container) (typed FeaturePython)
  n = 1
  ref = Hg_element
FEATURE [App::DocumentObjectGroupPython] I_element004  label="I_element : 2"  # scripted group (container) (typed FeaturePython)
  n = 2
  ref = I_element
FEATURE [App::DocumentObjectGroupPython] G4_MERCURIC_IODIDE  # scripted group (container) (typed FeaturePython)
  Dunit = g/cm3
  Dvalue = 6.36
  Group = -> [Hg_element001,I_element004]
  conduct = 2
  density = 1
  expand = 3
  formula = G4_MERCURIC_IODIDE
  name = G4_MERCURIC_IODIDE
  specific = 4
FEATURE [App::DocumentObjectGroupPython] C_element059  label="C_element : 032"  # scripted group (container) (typed FeaturePython)
  n = 1
  ref = C_element
FEATURE [App::DocumentObjectGroupPython] H_element053  label="H_element : 028"  # scripted group (container) (typed FeaturePython)
  n = 4
  ref = H_element
FEATURE [App::DocumentObjectGroupPython] G4_METHANE  # scripted group (container) (typed FeaturePython)
  Dunit = g/cm3
  Dvalue = 0.000667151
  Group = -> [C_element059,H_element053]
  conduct = 2
  density = 1
  expand = 3
  formula = G4_METHANE
  name = G4_METHANE
  specific = 4
FEATURE [App::DocumentObjectGroupPython] C_element060  label="C_element : 033"  # scripted group (container) (typed FeaturePython)
  n = 1
  ref = C_element
FEATURE [App::DocumentObjectGroupPython] H_element054  label="H_element : 029"  # scripted group (container) (typed FeaturePython)
  n = 4
  ref = H_element
FEATURE [App::DocumentObjectGroupPython] O_element062  label="O_element : 033"  # scripted group (container) (typed FeaturePython)
  n = 1
  ref = O_element
FEATURE [App::DocumentObjectGroupPython] G4_METHANOL  # scripted group (container) (typed FeaturePython)
  Dunit = g/cm3
  Dvalue = 0.7914
  Group = -> [C_element060,H_element054,O_element062]
  conduct = 2
  density = 1
  expand = 3
  formula = G4_METHANOL
  name = G4_METHANOL
  specific = 4
FEATURE [App::DocumentObjectGroupPython] H_element055  label="H_element : 0.134"  # scripted group (container) (typed FeaturePython)
  n = 0.13404
FEATURE [App::DocumentObjectGroupPython] C_element061  label="C_element : 0.778"  # scripted group (container) (typed FeaturePython)
  n = 0.77796
FEATURE [App::DocumentObjectGroupPython] O_element063  label="O_element : 0.035"  # scripted group (container) (typed FeaturePython)
  n = 0.03502
FEATURE [App::DocumentObjectGroupPython] Mg_element009  label="Mg_element : 0.039"  # scripted group (container) (typed FeaturePython)
  n = 0.038594
FEATURE [App::DocumentObjectGroupPython] Ti_element002  label="Ti_element : 0.014"  # scripted group (container) (typed FeaturePython)
  n = 0.014386
FEATURE [App::DocumentObjectGroupPython] G4_MIX_D_WAX  # scripted group (container) (typed FeaturePython)
  Dunit = g/cm3
  Dvalue = 0.99
  Group = -> [H_element055,C_element061,O_element063,Mg_element009,Ti_element002]
  conduct = 2
  density = 1
  expand = 3
  formula = G4_MIX_D_WAX
  name = G4_MIX_D_WAX
  specific = 4
FEATURE [App::DocumentObjectGroupPython] H_element056  label="H_element : 0.135"  # scripted group (container) (typed FeaturePython)
  n = 0.081192
FEATURE [App::DocumentObjectGroupPython] C_element062  label="C_element : 0.583"  # scripted group (container) (typed FeaturePython)
  n = 0.583442
FEATURE [App::DocumentObjectGroupPython] N_element024  label="N_element : 0.018"  # scripted group (container) (typed FeaturePython)
  n = 0.017798
FEATURE [App::DocumentObjectGroupPython] O_element064  label="O_element : 0.186"  # scripted group (container) (typed FeaturePython)
  n = 0.186381
FEATURE [App::DocumentObjectGroupPython] Mg_element010  label="Mg_element : 0.130"  # scripted group (container) (typed FeaturePython)
  n = 0.130287
FEATURE [App::DocumentObjectGroupPython] Cl_element015  label="Cl_element : 0.588"  # scripted group (container) (typed FeaturePython)
  n = 0.0009
FEATURE [App::DocumentObjectGroupPython] G4_MS20_TISSUE  # scripted group (container) (typed FeaturePython)
  Dunit = g/cm3
  Dvalue = 1
  Group = -> [H_element056,C_element062,N_element024,O_element064,Mg_element010,Cl_element015]
  conduct = 2
  density = 1
  expand = 3
  formula = G4_MS20_TISSUE
  name = G4_MS20_TISSUE
  specific = 4
FEATURE [App::DocumentObjectGroupPython] H_element057  label="H_element : 0.136"  # scripted group (container) (typed FeaturePython)
  n = 0.102
FEATURE [App::DocumentObjectGroupPython] C_element063  label="C_element : 0.143"  # scripted group (container) (typed FeaturePython)
  n = 0.143
FEATURE [App::DocumentObjectGroupPython] N_element025  label="N_element : 0.034"  # scripted group (container) (typed FeaturePython)
  n = 0.034
FEATURE [App::DocumentObjectGroupPython] O_element065  label="O_element : 0.710"  # scripted group (container) (typed FeaturePython)
  n = 0.71
FEATURE [App::DocumentObjectGroupPython] Na_element011  label="Na_element : 0.098"  # scripted group (container) (typed FeaturePython)
  n = 0.001
FEATURE [App::DocumentObjectGroupPython] P_element007  label="P_element : 0.002"  # scripted group (container) (typed FeaturePython)
  n = 0.002
FEATURE [App::DocumentObjectGroupPython] S_element017  label="S_element : 0.018"  # scripted group (container) (typed FeaturePython)
  n = 0.003
FEATURE [App::DocumentObjectGroupPython] Cl_element016  label="Cl_element : 0.589"  # scripted group (container) (typed FeaturePython)
  n = 0.001
FEATURE [App::DocumentObjectGroupPython] K_element006  label="K_element : 0.004"  # scripted group (container) (typed FeaturePython)
  n = 0.004
FEATURE [App::DocumentObjectGroupPython] G4_MUSCLE_SKELETAL_ICRP  # scripted group (container) (typed FeaturePython)
  Dunit = g/cm3
  Dvalue = 1.05
  Group = -> [H_element057,C_element063,N_element025,O_element065,Na_element011,P_element007,S_element017,Cl_element016,K_element006]
  conduct = 2
  density = 1
  expand = 3
  formula = G4_MUSCLE_SKELETAL_ICRP
  name = G4_MUSCLE_SKELETAL_ICRP
  specific = 4
FEATURE [App::DocumentObjectGroupPython] H_element058  label="H_element : 0.137"  # scripted group (container) (typed FeaturePython)
  n = 0.102102
FEATURE [App::DocumentObjectGroupPython] C_element064  label="C_element : 0.123"  # scripted group (container) (typed FeaturePython)
  n = 0.123123
FEATURE [App::DocumentObjectGroupPython] N_element026  label="N_element : 0.756"  # scripted group (container) (typed FeaturePython)
  n = 0.035035
FEATURE [App::DocumentObjectGroupPython] O_element066  label="O_element : 0.730"  # scripted group (container) (typed FeaturePython)
  n = 0.72973
FEATURE [App::DocumentObjectGroupPython] Na_element012  label="Na_element : 0.099"  # scripted group (container) (typed FeaturePython)
  n = 0.001001
FEATURE [App::DocumentObjectGroupPython] P_element008  label="P_element : 0.106"  # scripted group (container) (typed FeaturePython)
  n = 0.002002
FEATURE [App::DocumentObjectGroupPython] S_element018  label="S_element : 0.019"  # scripted group (container) (typed FeaturePython)
  n = 0.004004
FEATURE [App::DocumentObjectGroupPython] K_element007  label="K_element : 0.016"  # scripted group (container) (typed FeaturePython)
  n = 0.003003
FEATURE [App::DocumentObjectGroupPython] G4_MUSCLE_STRIATED_ICRU  # scripted group (container) (typed FeaturePython)
  Dunit = g/cm3
  Dvalue = 1.04
  Group = -> [H_element058,C_element064,N_element026,O_element066,Na_element012,P_element008,S_element018,K_element007]
  conduct = 2
  density = 1
  expand = 3
  formula = G4_MUSCLE_STRIATED_ICRU
  name = G4_MUSCLE_STRIATED_ICRU
  specific = 4
FEATURE [App::DocumentObjectGroupPython] H_element059  label="H_element : 0.098"  # scripted group (container) (typed FeaturePython)
  n = 0.0982341
FEATURE [App::DocumentObjectGroupPython] C_element065  label="C_element : 0.156"  # scripted group (container) (typed FeaturePython)
  n = 0.156214
FEATURE [App::DocumentObjectGroupPython] N_element027  label="N_element : 0.757"  # scripted group (container) (typed FeaturePython)
  n = 0.035451
FEATURE [App::DocumentObjectGroupPython] O_element067  label="O_element : 0.880"  # scripted group (container) (typed FeaturePython)
  n = 0.710101
FEATURE [App::DocumentObjectGroupPython] G4_MUSCLE_WITH_SUCROSE  # scripted group (container) (typed FeaturePython)
  Dunit = g/cm3
  Dvalue = 1.11
  Group = -> [H_element059,C_element065,N_element027,O_element067]
  conduct = 2
  density = 1
  expand = 3
  formula = G4_MUSCLE_WITH_SUCROSE
  name = G4_MUSCLE_WITH_SUCROSE
  specific = 4
FEATURE [App::DocumentObjectGroupPython] H_element060  label="H_element : 0.138"  # scripted group (container) (typed FeaturePython)
  n = 0.101969
FEATURE [App::DocumentObjectGroupPython] C_element066  label="C_element : 0.120"  # scripted group (container) (typed FeaturePython)
  n = 0.120058
FEATURE [App::DocumentObjectGroupPython] N_element028  label="N_element : 0.758"  # scripted group (container) (typed FeaturePython)
  n = 0.035451
FEATURE [App::DocumentObjectGroupPython] O_element068  label="O_element : 0.743"  # scripted group (container) (typed FeaturePython)
  n = 0.742522
FEATURE [App::DocumentObjectGroupPython] G4_MUSCLE_WITHOUT_SUCROSE  # scripted group (container) (typed FeaturePython)
  Dunit = g/cm3
  Dvalue = 1.07
  Group = -> [H_element060,C_element066,N_element028,O_element068]
  conduct = 2
  density = 1
  expand = 3
  formula = G4_MUSCLE_WITHOUT_SUCROSE
  name = G4_MUSCLE_WITHOUT_SUCROSE
  specific = 4
FEATURE [App::DocumentObjectGroupPython] C_element067  label="C_element : 10"  # scripted group (container) (typed FeaturePython)
  n = 10
  ref = C_element
FEATURE [App::DocumentObjectGroupPython] H_element061  label="H_element : 030"  # scripted group (container) (typed FeaturePython)
  n = 8
  ref = H_element
FEATURE [App::DocumentObjectGroupPython] G4_NAPHTHALENE  # scripted group (container) (typed FeaturePython)
  Dunit = g/cm3
  Dvalue = 1.145
  Group = -> [C_element067,H_element061]
  conduct = 2
  density = 1
  expand = 3
  formula = G4_NAPHTHALENE
  name = G4_NAPHTHALENE
  specific = 4
FEATURE [App::DocumentObjectGroupPython] C_element068  label="C_element : 034"  # scripted group (container) (typed FeaturePython)
  n = 6
  ref = C_element
FEATURE [App::DocumentObjectGroupPython] H_element062  label="H_element : 031"  # scripted group (container) (typed FeaturePython)
  n = 5
  ref = H_element
FEATURE [App::DocumentObjectGroupPython] N_element029  label="N_element : 012"  # scripted group (container) (typed FeaturePython)
  n = 1
  ref = N_element
FEATURE [App::DocumentObjectGroupPython] O_element069  label="O_element : 034"  # scripted group (container) (typed FeaturePython)
  n = 2
  ref = O_element
FEATURE [App::DocumentObjectGroupPython] G4_NITROBENZENE  # scripted group (container) (typed FeaturePython)
  Dunit = g/cm3
  Dvalue = 1.19867
  Group = -> [C_element068,H_element062,N_element029,O_element069]
  conduct = 2
  density = 1
  expand = 3
  formula = G4_NITROBENZENE
  name = G4_NITROBENZENE
  specific = 4
FEATURE [App::DocumentObjectGroupPython] N_element030  label="N_element : 013"  # scripted group (container) (typed FeaturePython)
  n = 2
  ref = N_element
FEATURE [App::DocumentObjectGroupPython] O_element070  label="O_element : 035"  # scripted group (container) (typed FeaturePython)
  n = 1
  ref = O_element
FEATURE [App::DocumentObjectGroupPython] G4_NITROUS_OXIDE  # scripted group (container) (typed FeaturePython)
  Dunit = g/cm3
  Dvalue = 0.00183094
  Group = -> [N_element030,O_element070]
  conduct = 2
  density = 1
  expand = 3
  formula = G4_NITROUS_OXIDE
  name = G4_NITROUS_OXIDE
  specific = 4
FEATURE [App::DocumentObjectGroupPython] H_element063  label="H_element : 0.104"  # scripted group (container) (typed FeaturePython)
  n = 0.103509
FEATURE [App::DocumentObjectGroupPython] C_element069  label="C_element : 0.648"  # scripted group (container) (typed FeaturePython)
  n = 0.648416
FEATURE [App::DocumentObjectGroupPython] N_element031  label="N_element : 0.100"  # scripted group (container) (typed FeaturePython)
  n = 0.0995361
FEATURE [App::DocumentObjectGroupPython] O_element071  label="O_element : 0.149"  # scripted group (container) (typed FeaturePython)
  n = 0.148539
FEATURE [App::DocumentObjectGroupPython] G4_NYLON_8062  label="G4_NYLON-8062"  # scripted group (container) (typed FeaturePython)
  Dunit = g/cm3
  Dvalue = 1.08
  Group = -> [H_element063,C_element069,N_element031,O_element071]
  conduct = 2
  density = 1
  expand = 3
  formula = G4_NYLON-8062
  name = G4_NYLON-8062
  specific = 4
FEATURE [App::DocumentObjectGroupPython] C_element070  label="C_element : 035"  # scripted group (container) (typed FeaturePython)
  n = 6
  ref = C_element
FEATURE [App::DocumentObjectGroupPython] H_element064  label="H_element : 11"  # scripted group (container) (typed FeaturePython)
  n = 11
  ref = H_element
FEATURE [App::DocumentObjectGroupPython] N_element032  label="N_element : 014"  # scripted group (container) (typed FeaturePython)
  n = 1
  ref = N_element
FEATURE [App::DocumentObjectGroupPython] O_element072  label="O_element : 036"  # scripted group (container) (typed FeaturePython)
  n = 1
  ref = O_element
FEATURE [App::DocumentObjectGroupPython] G4_NYLON_6_6  label="G4_NYLON-6-6"  # scripted group (container) (typed FeaturePython)
  Dunit = g/cm3
  Dvalue = 1.14
  Group = -> [C_element070,H_element064,N_element032,O_element072]
  conduct = 2
  density = 1
  expand = 3
  formula = G4_NYLON-6-6
  name = G4_NYLON-6-6
  specific = 4
FEATURE [App::DocumentObjectGroupPython] H_element065  label="H_element : 0.139"  # scripted group (container) (typed FeaturePython)
  n = 0.107062
FEATURE [App::DocumentObjectGroupPython] C_element071  label="C_element : 0.680"  # scripted group (container) (typed FeaturePython)
  n = 0.680449
FEATURE [App::DocumentObjectGroupPython] N_element033  label="N_element : 0.099"  # scripted group (container) (typed FeaturePython)
  n = 0.099189
FEATURE [App::DocumentObjectGroupPython] O_element073  label="O_element : 0.113"  # scripted group (container) (typed FeaturePython)
  n = 0.1133
FEATURE [App::DocumentObjectGroupPython] G4_NYLON_6_10  label="G4_NYLON-6-10"  # scripted group (container) (typed FeaturePython)
  Dunit = g/cm3
  Dvalue = 1.14
  Group = -> [H_element065,C_element071,N_element033,O_element073]
  conduct = 2
  density = 1
  expand = 3
  formula = G4_NYLON-6-10
  name = G4_NYLON-6-10
  specific = 4
FEATURE [App::DocumentObjectGroupPython] H_element066  label="H_element : 0.140"  # scripted group (container) (typed FeaturePython)
  n = 0.115476
FEATURE [App::DocumentObjectGroupPython] C_element072  label="C_element : 0.721"  # scripted group (container) (typed FeaturePython)
  n = 0.720818
FEATURE [App::DocumentObjectGroupPython] N_element034  label="N_element : 0.076"  # scripted group (container) (typed FeaturePython)
  n = 0.0764169
FEATURE [App::DocumentObjectGroupPython] O_element074  label="O_element : 0.087"  # scripted group (container) (typed FeaturePython)
  n = 0.0872889
FEATURE [App::DocumentObjectGroupPython] G4_NYLON_11_RILSAN  label="G4_NYLON-11_RILSAN"  # scripted group (container) (typed FeaturePython)
  Dunit = g/cm3
  Dvalue = 1.425
  Group = -> [H_element066,C_element072,N_element034,O_element074]
  conduct = 2
  density = 1
  expand = 3
  formula = G4_NYLON-11_RILSAN
  name = G4_NYLON-11_RILSAN
  specific = 4
FEATURE [App::DocumentObjectGroupPython] C_element073  label="C_element : 8"  # scripted group (container) (typed FeaturePython)
  n = 8
  ref = C_element
FEATURE [App::DocumentObjectGroupPython] H_element067  label="H_element : 18"  # scripted group (container) (typed FeaturePython)
  n = 18
  ref = H_element
FEATURE [App::DocumentObjectGroupPython] G4_OCTANE  # scripted group (container) (typed FeaturePython)
  Dunit = g/cm3
  Dvalue = 0.7026
  Group = -> [C_element073,H_element067]
  conduct = 2
  density = 1
  expand = 3
  formula = G4_OCTANE
  name = G4_OCTANE
  specific = 4
FEATURE [App::DocumentObjectGroupPython] C_element074  label="C_element : 25"  # scripted group (container) (typed FeaturePython)
  n = 25
  ref = C_element
FEATURE [App::DocumentObjectGroupPython] H_element068  label="H_element : 52"  # scripted group (container) (typed FeaturePython)
  n = 52
  ref = H_element
FEATURE [App::DocumentObjectGroupPython] G4_PARAFFIN  # scripted group (container) (typed FeaturePython)
  Dunit = g/cm3
  Dvalue = 0.93
  Group = -> [C_element074,H_element068]
  conduct = 2
  density = 1
  expand = 3
  formula = G4_PARAFFIN
  name = G4_PARAFFIN
  specific = 4
FEATURE [App::DocumentObjectGroupPython] C_element075  label="C_element : 036"  # scripted group (container) (typed FeaturePython)
  n = 5
  ref = C_element
FEATURE [App::DocumentObjectGroupPython] H_element069  label="H_element : 032"  # scripted group (container) (typed FeaturePython)
  n = 12
  ref = H_element
FEATURE [App::DocumentObjectGroupPython] G4_N_PENTANE  label="G4_N-PENTANE"  # scripted group (container) (typed FeaturePython)
  Dunit = g/cm3
  Dvalue = 0.6262
  Group = -> [C_element075,H_element069]
  conduct = 2
  density = 1
  expand = 3
  formula = G4_N-PENTANE
  name = G4_N-PENTANE
  specific = 4
FEATURE [App::DocumentObjectGroupPython] H_element070  label="H_element : 0.014"  # scripted group (container) (typed FeaturePython)
  n = 0.0141
FEATURE [App::DocumentObjectGroupPython] C_element076  label="C_element : 0.072"  # scripted group (container) (typed FeaturePython)
  n = 0.072261
FEATURE [App::DocumentObjectGroupPython] N_element035  label="N_element : 0.019"  # scripted group (container) (typed FeaturePython)
  n = 0.01932
FEATURE [App::DocumentObjectGroupPython] O_element075  label="O_element : 0.066"  # scripted group (container) (typed FeaturePython)
  n = 0.066101
FEATURE [App::DocumentObjectGroupPython] S_element019  label="S_element : 0.020"  # scripted group (container) (typed FeaturePython)
  n = 0.00189
FEATURE [App::DocumentObjectGroupPython] Br_element004  label="Br_element : 0.349"  # scripted group (container) (typed FeaturePython)
  n = 0.349103
FEATURE [App::DocumentObjectGroupPython] Ag_element001  label="Ag_element : 0.474"  # scripted group (container) (typed FeaturePython)
  n = 0.474105
FEATURE [App::DocumentObjectGroupPython] I_element005  label="I_element : 0.003"  # scripted group (container) (typed FeaturePython)
  n = 0.00312
FEATURE [App::DocumentObjectGroupPython] G4_PHOTO_EMULSION  # scripted group (container) (typed FeaturePython)
  Dunit = g/cm3
  Dvalue = 3.815
  Group = -> [H_element070,C_element076,N_element035,O_element075,S_element019,Br_element004,Ag_element001,I_element005]
  conduct = 2
  density = 1
  expand = 3
  formula = G4_PHOTO_EMULSION
  name = G4_PHOTO_EMULSION
  specific = 4
FEATURE [App::DocumentObjectGroupPython] C_element077  label="C_element : 9"  # scripted group (container) (typed FeaturePython)
  n = 9
  ref = C_element
FEATURE [App::DocumentObjectGroupPython] H_element071  label="H_element : 033"  # scripted group (container) (typed FeaturePython)
  n = 10
  ref = H_element
FEATURE [App::DocumentObjectGroupPython] G4_PLASTIC_SC_VINYLTOLUENE  # scripted group (container) (typed FeaturePython)
  Dunit = g/cm3
  Dvalue = 1.032
  Group = -> [C_element077,H_element071]
  conduct = 2
  density = 1
  expand = 3
  formula = G4_PLASTIC_SC_VINYLTOLUENE
  name = G4_PLASTIC_SC_VINYLTOLUENE
  specific = 4
FEATURE [App::DocumentObjectGroupPython] Pu_element001  label="Pu_element : 1"  # scripted group (container) (typed FeaturePython)
  n = 1
  ref = Pu_element
FEATURE [App::DocumentObjectGroupPython] O_element076  label="O_element : 037"  # scripted group (container) (typed FeaturePython)
  n = 2
  ref = O_element
FEATURE [App::DocumentObjectGroupPython] G4_PLUTONIUM_DIOXIDE  # scripted group (container) (typed FeaturePython)
  Dunit = g/cm3
  Dvalue = 11.46
  Group = -> [Pu_element001,O_element076]
  conduct = 2
  density = 1
  expand = 3
  formula = G4_PLUTONIUM_DIOXIDE
  name = G4_PLUTONIUM_DIOXIDE
  specific = 4
FEATURE [App::DocumentObjectGroupPython] C_element078  label="C_element : 037"  # scripted group (container) (typed FeaturePython)
  n = 3
  ref = C_element
FEATURE [App::DocumentObjectGroupPython] H_element072  label="H_element : 034"  # scripted group (container) (typed FeaturePython)
  n = 3
  ref = H_element
FEATURE [App::DocumentObjectGroupPython] N_element036  label="N_element : 015"  # scripted group (container) (typed FeaturePython)
  n = 1
  ref = N_element
FEATURE [App::DocumentObjectGroupPython] G4_POLYACRYLONITRILE  # scripted group (container) (typed FeaturePython)
  Dunit = g/cm3
  Dvalue = 1.17
  Group = -> [C_element078,H_element072,N_element036]
  conduct = 2
  density = 1
  expand = 3
  formula = G4_POLYACRYLONITRILE
  name = G4_POLYACRYLONITRILE
  specific = 4
FEATURE [App::DocumentObjectGroupPython] C_element079  label="C_element : 16"  # scripted group (container) (typed FeaturePython)
  n = 16
  ref = C_element
FEATURE [App::DocumentObjectGroupPython] H_element073  label="H_element : 035"  # scripted group (container) (typed FeaturePython)
  n = 14
  ref = H_element
FEATURE [App::DocumentObjectGroupPython] O_element077  label="O_element : 038"  # scripted group (container) (typed FeaturePython)
  n = 3
  ref = O_element
FEATURE [App::DocumentObjectGroupPython] G4_POLYCARBONATE  # scripted group (container) (typed FeaturePython)
  Dunit = g/cm3
  Dvalue = 1.2
  Group = -> [C_element079,H_element073,O_element077]
  conduct = 2
  density = 1
  expand = 3
  formula = G4_POLYCARBONATE
  name = G4_POLYCARBONATE
  specific = 4
FEATURE [App::DocumentObjectGroupPython] C_element080  label="C_element : 038"  # scripted group (container) (typed FeaturePython)
  n = 8
  ref = C_element
FEATURE [App::DocumentObjectGroupPython] H_element074  label="H_element : 036"  # scripted group (container) (typed FeaturePython)
  n = 7
  ref = H_element
FEATURE [App::DocumentObjectGroupPython] Cl_element017  label="Cl_element : 007"  # scripted group (container) (typed FeaturePython)
  n = 1
  ref = Cl_element
FEATURE [App::DocumentObjectGroupPython] G4_POLYCHLOROSTYRENE  # scripted group (container) (typed FeaturePython)
  Dunit = g/cm3
  Dvalue = 1.3
  Group = -> [C_element080,H_element074,Cl_element017]
  conduct = 2
  density = 1
  expand = 3
  formula = G4_POLYCHLOROSTYRENE
  name = G4_POLYCHLOROSTYRENE
  specific = 4
FEATURE [App::DocumentObjectGroupPython] C_element081  label="C_element : 039"  # scripted group (container) (typed FeaturePython)
  n = 1
  ref = C_element
FEATURE [App::DocumentObjectGroupPython] H_element075  label="H_element : 037"  # scripted group (container) (typed FeaturePython)
  n = 2
  ref = H_element
FEATURE [App::DocumentObjectGroupPython] G4_POLYETHYLENE  # scripted group (container) (typed FeaturePython)
  Dunit = g/cm3
  Dvalue = 0.94
  Group = -> [C_element081,H_element075]
  conduct = 2
  density = 1
  expand = 3
  formula = G4_POLYETHYLENE
  name = G4_POLYETHYLENE
  specific = 4
FEATURE [App::DocumentObjectGroupPython] C_element082  label="C_element : 040"  # scripted group (container) (typed FeaturePython)
  n = 10
  ref = C_element
FEATURE [App::DocumentObjectGroupPython] H_element076  label="H_element : 038"  # scripted group (container) (typed FeaturePython)
  n = 8
  ref = H_element
FEATURE [App::DocumentObjectGroupPython] O_element078  label="O_element : 039"  # scripted group (container) (typed FeaturePython)
  n = 4
  ref = O_element
FEATURE [App::DocumentObjectGroupPython] G4_MYLAR  # scripted group (container) (typed FeaturePython)
  Dunit = g/cm3
  Dvalue = 1.4
  Group = -> [C_element082,H_element076,O_element078]
  conduct = 2
  density = 1
  expand = 3
  formula = G4_MYLAR
  name = G4_MYLAR
  specific = 4
FEATURE [App::DocumentObjectGroupPython] C_element083  label="C_element : 041"  # scripted group (container) (typed FeaturePython)
  n = 5
  ref = C_element
FEATURE [App::DocumentObjectGroupPython] H_element077  label="H_element : 039"  # scripted group (container) (typed FeaturePython)
  n = 8
  ref = H_element
FEATURE [App::DocumentObjectGroupPython] O_element079  label="O_element : 040"  # scripted group (container) (typed FeaturePython)
  n = 2
  ref = O_element
FEATURE [App::DocumentObjectGroupPython] G4_PLEXIGLASS  # scripted group (container) (typed FeaturePython)
  Dunit = g/cm3
  Dvalue = 1.19
  Group = -> [C_element083,H_element077,O_element079]
  conduct = 2
  density = 1
  expand = 3
  formula = G4_PLEXIGLASS
  name = G4_PLEXIGLASS
  specific = 4
FEATURE [App::DocumentObjectGroupPython] C_element084  label="C_element : 042"  # scripted group (container) (typed FeaturePython)
  n = 1
  ref = C_element
FEATURE [App::DocumentObjectGroupPython] H_element078  label="H_element : 040"  # scripted group (container) (typed FeaturePython)
  n = 2
  ref = H_element
FEATURE [App::DocumentObjectGroupPython] O_element080  label="O_element : 041"  # scripted group (container) (typed FeaturePython)
  n = 1
  ref = O_element
FEATURE [App::DocumentObjectGroupPython] G4_POLYOXYMETHYLENE  # scripted group (container) (typed FeaturePython)
  Dunit = g/cm3
  Dvalue = 1.425
  Group = -> [C_element084,H_element078,O_element080]
  conduct = 2
  density = 1
  expand = 3
  formula = G4_POLYOXYMETHYLENE
  name = G4_POLYOXYMETHYLENE
  specific = 4
FEATURE [App::DocumentObjectGroupPython] C_element085  label="C_element : 043"  # scripted group (container) (typed FeaturePython)
  n = 2
  ref = C_element
FEATURE [App::DocumentObjectGroupPython] H_element079  label="H_element : 041"  # scripted group (container) (typed FeaturePython)
  n = 4
  ref = H_element
FEATURE [App::DocumentObjectGroupPython] G4_POLYPROPYLENE  # scripted group (container) (typed FeaturePython)
  Dunit = g/cm3
  Dvalue = 0.9
  Group = -> [C_element085,H_element079]
  conduct = 2
  density = 1
  expand = 3
  formula = G4_POLYPROPYLENE
  name = G4_POLYPROPYLENE
  specific = 4
FEATURE [App::DocumentObjectGroupPython] C_element086  label="C_element : 044"  # scripted group (container) (typed FeaturePython)
  n = 8
  ref = C_element
FEATURE [App::DocumentObjectGroupPython] H_element080  label="H_element : 042"  # scripted group (container) (typed FeaturePython)
  n = 8
  ref = H_element
FEATURE [App::DocumentObjectGroupPython] G4_POLYSTYRENE  # scripted group (container) (typed FeaturePython)
  Dunit = g/cm3
  Dvalue = 1.06
  Group = -> [C_element086,H_element080]
  conduct = 2
  density = 1
  expand = 3
  formula = G4_POLYSTYRENE
  name = G4_POLYSTYRENE
  specific = 4
FEATURE [App::DocumentObjectGroupPython] C_element087  label="C_element : 045"  # scripted group (container) (typed FeaturePython)
  n = 2
  ref = C_element
FEATURE [App::DocumentObjectGroupPython] F_element014  label="F_element : 4"  # scripted group (container) (typed FeaturePython)
  n = 4
  ref = F_element
FEATURE [App::DocumentObjectGroupPython] G4_TEFLON  # scripted group (container) (typed FeaturePython)
  Dunit = g/cm3
  Dvalue = 2.2
  Group = -> [C_element087,F_element014]
  conduct = 2
  density = 1
  expand = 3
  formula = G4_TEFLON
  name = G4_TEFLON
  specific = 4
FEATURE [App::DocumentObjectGroupPython] C_element088  label="C_element : 046"  # scripted group (container) (typed FeaturePython)
  n = 2
  ref = C_element
FEATURE [App::DocumentObjectGroupPython] F_element015  label="F_element : 006"  # scripted group (container) (typed FeaturePython)
  n = 3
  ref = F_element
FEATURE [App::DocumentObjectGroupPython] Cl_element018  label="Cl_element : 008"  # scripted group (container) (typed FeaturePython)
  n = 1
  ref = Cl_element
FEATURE [App::DocumentObjectGroupPython] G4_POLYTRIFLUOROCHLOROETHYLENE  # scripted group (container) (typed FeaturePython)
  Dunit = g/cm3
  Dvalue = 2.1
  Group = -> [C_element088,F_element015,Cl_element018]
  conduct = 2
  density = 1
  expand = 3
  formula = G4_POLYTRIFLUOROCHLOROETHYLENE
  name = G4_POLYTRIFLUOROCHLOROETHYLENE
  specific = 4
FEATURE [App::DocumentObjectGroupPython] C_element089  label="C_element : 047"  # scripted group (container) (typed FeaturePython)
  n = 4
  ref = C_element
FEATURE [App::DocumentObjectGroupPython] H_element081  label="H_element : 043"  # scripted group (container) (typed FeaturePython)
  n = 6
  ref = H_element
FEATURE [App::DocumentObjectGroupPython] O_element081  label="O_element : 042"  # scripted group (container) (typed FeaturePython)
  n = 2
  ref = O_element
FEATURE [App::DocumentObjectGroupPython] G4_POLYVINYL_ACETATE  # scripted group (container) (typed FeaturePython)
  Dunit = g/cm3
  Dvalue = 1.19
  Group = -> [C_element089,H_element081,O_element081]
  conduct = 2
  density = 1
  expand = 3
  formula = G4_POLYVINYL_ACETATE
  name = G4_POLYVINYL_ACETATE
  specific = 4
FEATURE [App::DocumentObjectGroupPython] C_element090  label="C_element : 048"  # scripted group (container) (typed FeaturePython)
  n = 2
  ref = C_element
FEATURE [App::DocumentObjectGroupPython] H_element082  label="H_element : 044"  # scripted group (container) (typed FeaturePython)
  n = 4
  ref = H_element
FEATURE [App::DocumentObjectGroupPython] O_element082  label="O_element : 043"  # scripted group (container) (typed FeaturePython)
  n = 1
  ref = O_element
FEATURE [App::DocumentObjectGroupPython] G4_POLYVINYL_ALCOHOL  # scripted group (container) (typed FeaturePython)
  Dunit = g/cm3
  Dvalue = 1.3
  Group = -> [C_element090,H_element082,O_element082]
  conduct = 2
  density = 1
  expand = 3
  formula = G4_POLYVINYL_ALCOHOL
  name = G4_POLYVINYL_ALCOHOL
  specific = 4
FEATURE [App::DocumentObjectGroupPython] C_element091  label="C_element : 049"  # scripted group (container) (typed FeaturePython)
  n = 8
  ref = C_element
FEATURE [App::DocumentObjectGroupPython] H_element083  label="H_element : 045"  # scripted group (container) (typed FeaturePython)
  n = 14
  ref = H_element
FEATURE [App::DocumentObjectGroupPython] O_element083  label="O_element : 044"  # scripted group (container) (typed FeaturePython)
  n = 2
  ref = O_element
FEATURE [App::DocumentObjectGroupPython] G4_POLYVINYL_BUTYRAL  # scripted group (container) (typed FeaturePython)
  Dunit = g/cm3
  Dvalue = 1.12
  Group = -> [C_element091,H_element083,O_element083]
  conduct = 2
  density = 1
  expand = 3
  formula = G4_POLYVINYL_BUTYRAL
  name = G4_POLYVINYL_BUTYRAL
  specific = 4
FEATURE [App::DocumentObjectGroupPython] C_element092  label="C_element : 050"  # scripted group (container) (typed FeaturePython)
  n = 2
  ref = C_element
FEATURE [App::DocumentObjectGroupPython] H_element084  label="H_element : 046"  # scripted group (container) (typed FeaturePython)
  n = 3
  ref = H_element
FEATURE [App::DocumentObjectGroupPython] Cl_element019  label="Cl_element : 009"  # scripted group (container) (typed FeaturePython)
  n = 1
  ref = Cl_element
FEATURE [App::DocumentObjectGroupPython] G4_POLYVINYL_CHLORIDE  # scripted group (container) (typed FeaturePython)
  Dunit = g/cm3
  Dvalue = 1.3
  Group = -> [C_element092,H_element084,Cl_element019]
  conduct = 2
  density = 1
  expand = 3
  formula = G4_POLYVINYL_CHLORIDE
  name = G4_POLYVINYL_CHLORIDE
  specific = 4
FEATURE [App::DocumentObjectGroupPython] C_element093  label="C_element : 051"  # scripted group (container) (typed FeaturePython)
  n = 2
  ref = C_element
FEATURE [App::DocumentObjectGroupPython] H_element085  label="H_element : 047"  # scripted group (container) (typed FeaturePython)
  n = 2
  ref = H_element
FEATURE [App::DocumentObjectGroupPython] Cl_element020  label="Cl_element : 010"  # scripted group (container) (typed FeaturePython)
  n = 2
  ref = Cl_element
FEATURE [App::DocumentObjectGroupPython] G4_POLYVINYLIDENE_CHLORIDE  # scripted group (container) (typed FeaturePython)
  Dunit = g/cm3
  Dvalue = 1.7
  Group = -> [C_element093,H_element085,Cl_element020]
  conduct = 2
  density = 1
  expand = 3
  formula = G4_POLYVINYLIDENE_CHLORIDE
  name = G4_POLYVINYLIDENE_CHLORIDE
  specific = 4
FEATURE [App::DocumentObjectGroupPython] C_element094  label="C_element : 052"  # scripted group (container) (typed FeaturePython)
  n = 2
  ref = C_element
FEATURE [App::DocumentObjectGroupPython] H_element086  label="H_element : 048"  # scripted group (container) (typed FeaturePython)
  n = 2
  ref = H_element
FEATURE [App::DocumentObjectGroupPython] F_element016  label="F_element : 007"  # scripted group (container) (typed FeaturePython)
  n = 2
  ref = F_element
FEATURE [App::DocumentObjectGroupPython] G4_POLYVINYLIDENE_FLUORIDE  # scripted group (container) (typed FeaturePython)
  Dunit = g/cm3
  Dvalue = 1.76
  Group = -> [C_element094,H_element086,F_element016]
  conduct = 2
  density = 1
  expand = 3
  formula = G4_POLYVINYLIDENE_FLUORIDE
  name = G4_POLYVINYLIDENE_FLUORIDE
  specific = 4
FEATURE [App::DocumentObjectGroupPython] C_element095  label="C_element : 053"  # scripted group (container) (typed FeaturePython)
  n = 6
  ref = C_element
FEATURE [App::DocumentObjectGroupPython] H_element087  label="H_element : 9"  # scripted group (container) (typed FeaturePython)
  n = 9
  ref = H_element
FEATURE [App::DocumentObjectGroupPython] N_element037  label="N_element : 016"  # scripted group (container) (typed FeaturePython)
  n = 1
  ref = N_element
FEATURE [App::DocumentObjectGroupPython] O_element084  label="O_element : 045"  # scripted group (container) (typed FeaturePython)
  n = 1
  ref = O_element
FEATURE [App::DocumentObjectGroupPython] G4_POLYVINYL_PYRROLIDONE  # scripted group (container) (typed FeaturePython)
  Dunit = g/cm3
  Dvalue = 1.25
  Group = -> [C_element095,H_element087,N_element037,O_element084]
  conduct = 2
  density = 1
  expand = 3
  formula = G4_POLYVINYL_PYRROLIDONE
  name = G4_POLYVINYL_PYRROLIDONE
  specific = 4
FEATURE [App::DocumentObjectGroupPython] K_element008  label="K_element : 1"  # scripted group (container) (typed FeaturePython)
  n = 1
  ref = K_element
FEATURE [App::DocumentObjectGroupPython] I_element006  label="I_element : 003"  # scripted group (container) (typed FeaturePython)
  n = 1
  ref = I_element
FEATURE [App::DocumentObjectGroupPython] G4_POTASSIUM_IODIDE  # scripted group (container) (typed FeaturePython)
  Dunit = g/cm3
  Dvalue = 3.13
  Group = -> [K_element008,I_element006]
  conduct = 2
  density = 1
  expand = 3
  formula = G4_POTASSIUM_IODIDE
  name = G4_POTASSIUM_IODIDE
  specific = 4
FEATURE [App::DocumentObjectGroupPython] K_element009  label="K_element : 2"  # scripted group (container) (typed FeaturePython)
  n = 2
  ref = K_element
FEATURE [App::DocumentObjectGroupPython] O_element085  label="O_element : 046"  # scripted group (container) (typed FeaturePython)
  n = 1
  ref = O_element
FEATURE [App::DocumentObjectGroupPython] G4_POTASSIUM_OXIDE  # scripted group (container) (typed FeaturePython)
  Dunit = g/cm3
  Dvalue = 2.32
  Group = -> [K_element009,O_element085]
  conduct = 2
  density = 1
  expand = 3
  formula = G4_POTASSIUM_OXIDE
  name = G4_POTASSIUM_OXIDE
  specific = 4
FEATURE [App::DocumentObjectGroupPython] C_element096  label="C_element : 054"  # scripted group (container) (typed FeaturePython)
  n = 3
  ref = C_element
FEATURE [App::DocumentObjectGroupPython] H_element088  label="H_element : 049"  # scripted group (container) (typed FeaturePython)
  n = 8
  ref = H_element
FEATURE [App::DocumentObjectGroupPython] G4_PROPANE  # scripted group (container) (typed FeaturePython)
  Dunit = g/cm3
  Dvalue = 0.00187939
  Group = -> [C_element096,H_element088]
  conduct = 2
  density = 1
  expand = 3
  formula = G4_PROPANE
  name = G4_PROPANE
  specific = 4
FEATURE [App::DocumentObjectGroupPython] C_element097  label="C_element : 055"  # scripted group (container) (typed FeaturePython)
  n = 3
  ref = C_element
FEATURE [App::DocumentObjectGroupPython] H_element089  label="H_element : 050"  # scripted group (container) (typed FeaturePython)
  n = 8
  ref = H_element
FEATURE [App::DocumentObjectGroupPython] G4_lPROPANE  # scripted group (container) (typed FeaturePython)
  Dunit = g/cm3
  Dvalue = 0.43
  Group = -> [C_element097,H_element089]
  conduct = 2
  density = 1
  expand = 3
  formula = G4_lPROPANE
  name = G4_lPROPANE
  specific = 4
FEATURE [App::DocumentObjectGroupPython] C_element098  label="C_element : 056"  # scripted group (container) (typed FeaturePython)
  n = 3
  ref = C_element
FEATURE [App::DocumentObjectGroupPython] H_element090  label="H_element : 051"  # scripted group (container) (typed FeaturePython)
  n = 8
  ref = H_element
FEATURE [App::DocumentObjectGroupPython] O_element086  label="O_element : 047"  # scripted group (container) (typed FeaturePython)
  n = 1
  ref = O_element
FEATURE [App::DocumentObjectGroupPython] G4_N_PROPYL_ALCOHOL  label="G4_N-PROPYL_ALCOHOL"  # scripted group (container) (typed FeaturePython)
  Dunit = g/cm3
  Dvalue = 0.8035
  Group = -> [C_element098,H_element090,O_element086]
  conduct = 2
  density = 1
  expand = 3
  formula = G4_N-PROPYL_ALCOHOL
  name = G4_N-PROPYL_ALCOHOL
  specific = 4
FEATURE [App::DocumentObjectGroupPython] C_element099  label="C_element : 057"  # scripted group (container) (typed FeaturePython)
  n = 5
  ref = C_element
FEATURE [App::DocumentObjectGroupPython] H_element091  label="H_element : 052"  # scripted group (container) (typed FeaturePython)
  n = 5
  ref = H_element
FEATURE [App::DocumentObjectGroupPython] N_element038  label="N_element : 017"  # scripted group (container) (typed FeaturePython)
  n = 1
  ref = N_element
FEATURE [App::DocumentObjectGroupPython] G4_PYRIDINE  # scripted group (container) (typed FeaturePython)
  Dunit = g/cm3
  Dvalue = 0.9819
  Group = -> [C_element099,H_element091,N_element038]
  conduct = 2
  density = 1
  expand = 3
  formula = G4_PYRIDINE
  name = G4_PYRIDINE
  specific = 4
FEATURE [App::DocumentObjectGroupPython] H_element092  label="H_element : 0.144"  # scripted group (container) (typed FeaturePython)
  n = 0.143711
FEATURE [App::DocumentObjectGroupPython] C_element100  label="C_element : 0.856"  # scripted group (container) (typed FeaturePython)
  n = 0.856289
FEATURE [App::DocumentObjectGroupPython] G4_RUBBER_BUTYL  # scripted group (container) (typed FeaturePython)
  Dunit = g/cm3
  Dvalue = 0.92
  Group = -> [H_element092,C_element100]
  conduct = 2
  density = 1
  expand = 3
  formula = G4_RUBBER_BUTYL
  name = G4_RUBBER_BUTYL
  specific = 4
FEATURE [App::DocumentObjectGroupPython] H_element093  label="H_element : 0.118"  # scripted group (container) (typed FeaturePython)
  n = 0.118371
FEATURE [App::DocumentObjectGroupPython] C_element101  label="C_element : 0.882"  # scripted group (container) (typed FeaturePython)
  n = 0.881629
FEATURE [App::DocumentObjectGroupPython] G4_RUBBER_NATURAL  # scripted group (container) (typed FeaturePython)
  Dunit = g/cm3
  Dvalue = 0.92
  Group = -> [H_element093,C_element101]
  conduct = 2
  density = 1
  expand = 3
  formula = G4_RUBBER_NATURAL
  name = G4_RUBBER_NATURAL
  specific = 4
FEATURE [App::DocumentObjectGroupPython] H_element094  label="H_element : 0.145"  # scripted group (container) (typed FeaturePython)
  n = 0.05692
FEATURE [App::DocumentObjectGroupPython] C_element102  label="C_element : 0.543"  # scripted group (container) (typed FeaturePython)
  n = 0.542646
FEATURE [App::DocumentObjectGroupPython] Cl_element021  label="Cl_element : 0.400"  # scripted group (container) (typed FeaturePython)
  n = 0.400434
FEATURE [App::DocumentObjectGroupPython] G4_RUBBER_NEOPRENE  # scripted group (container) (typed FeaturePython)
  Dunit = g/cm3
  Dvalue = 1.23
  Group = -> [H_element094,C_element102,Cl_element021]
  conduct = 2
  density = 1
  expand = 3
  formula = G4_RUBBER_NEOPRENE
  name = G4_RUBBER_NEOPRENE
  specific = 4
FEATURE [App::DocumentObjectGroupPython] Si_element006  label="Si_element : 1"  # scripted group (container) (typed FeaturePython)
  n = 1
  ref = Si_element
FEATURE [App::DocumentObjectGroupPython] O_element087  label="O_element : 048"  # scripted group (container) (typed FeaturePython)
  n = 2
  ref = O_element
FEATURE [App::DocumentObjectGroupPython] G4_SILICON_DIOXIDE  # scripted group (container) (typed FeaturePython)
  Dunit = g/cm3
  Dvalue = 2.32
  Group = -> [Si_element006,O_element087]
  conduct = 2
  density = 1
  expand = 3
  formula = G4_SILICON_DIOXIDE
  name = G4_SILICON_DIOXIDE
  specific = 4
FEATURE [App::DocumentObjectGroupPython] Ag_element002  label="Ag_element : 1"  # scripted group (container) (typed FeaturePython)
  n = 1
  ref = Ag_element
FEATURE [App::DocumentObjectGroupPython] Br_element005  label="Br_element : 003"  # scripted group (container) (typed FeaturePython)
  n = 1
  ref = Br_element
FEATURE [App::DocumentObjectGroupPython] G4_SILVER_BROMIDE  # scripted group (container) (typed FeaturePython)
  Dunit = g/cm3
  Dvalue = 6.473
  Group = -> [Ag_element002,Br_element005]
  conduct = 2
  density = 1
  expand = 3
  formula = G4_SILVER_BROMIDE
  name = G4_SILVER_BROMIDE
  specific = 4
FEATURE [App::DocumentObjectGroupPython] Ag_element003  label="Ag_element : 002"  # scripted group (container) (typed FeaturePython)
  n = 1
  ref = Ag_element
FEATURE [App::DocumentObjectGroupPython] Cl_element022  label="Cl_element : 011"  # scripted group (container) (typed FeaturePython)
  n = 1
  ref = Cl_element
FEATURE [App::DocumentObjectGroupPython] G4_SILVER_CHLORIDE  # scripted group (container) (typed FeaturePython)
  Dunit = g/cm3
  Dvalue = 5.56
  Group = -> [Ag_element003,Cl_element022]
  conduct = 2
  density = 1
  expand = 3
  formula = G4_SILVER_CHLORIDE
  name = G4_SILVER_CHLORIDE
  specific = 4
FEATURE [App::DocumentObjectGroupPython] Br_element006  label="Br_element : 0.423"  # scripted group (container) (typed FeaturePython)
  n = 0.422895
FEATURE [App::DocumentObjectGroupPython] Ag_element004  label="Ag_element : 0.574"  # scripted group (container) (typed FeaturePython)
  n = 0.573748
FEATURE [App::DocumentObjectGroupPython] I_element007  label="I_element : 0.649"  # scripted group (container) (typed FeaturePython)
  n = 0.003357
FEATURE [App::DocumentObjectGroupPython] G4_SILVER_HALIDES  # scripted group (container) (typed FeaturePython)
  Dunit = g/cm3
  Dvalue = 6.47
  Group = -> [Br_element006,Ag_element004,I_element007]
  conduct = 2
  density = 1
  expand = 3
  formula = G4_SILVER_HALIDES
  name = G4_SILVER_HALIDES
  specific = 4
FEATURE [App::DocumentObjectGroupPython] Ag_element005  label="Ag_element : 003"  # scripted group (container) (typed FeaturePython)
  n = 1
  ref = Ag_element
FEATURE [App::DocumentObjectGroupPython] I_element008  label="I_element : 004"  # scripted group (container) (typed FeaturePython)
  n = 1
  ref = I_element
FEATURE [App::DocumentObjectGroupPython] G4_SILVER_IODIDE  # scripted group (container) (typed FeaturePython)
  Dunit = g/cm3
  Dvalue = 6.01
  Group = -> [Ag_element005,I_element008]
  conduct = 2
  density = 1
  expand = 3
  formula = G4_SILVER_IODIDE
  name = G4_SILVER_IODIDE
  specific = 4
FEATURE [App::DocumentObjectGroupPython] H_element095  label="H_element : 0.100"  # scripted group (container) (typed FeaturePython)
  n = 0.1
FEATURE [App::DocumentObjectGroupPython] C_element103  label="C_element : 0.204"  # scripted group (container) (typed FeaturePython)
  n = 0.204
FEATURE [App::DocumentObjectGroupPython] N_element039  label="N_element : 0.759"  # scripted group (container) (typed FeaturePython)
  n = 0.042
FEATURE [App::DocumentObjectGroupPython] O_element088  label="O_element : 0.645"  # scripted group (container) (typed FeaturePython)
  n = 0.645
FEATURE [App::DocumentObjectGroupPython] Na_element013  label="Na_element : 0.100"  # scripted group (container) (typed FeaturePython)
  n = 0.002
FEATURE [App::DocumentObjectGroupPython] P_element009  label="P_element : 0.107"  # scripted group (container) (typed FeaturePython)
  n = 0.001
FEATURE [App::DocumentObjectGroupPython] S_element020  label="S_element : 0.021"  # scripted group (container) (typed FeaturePython)
  n = 0.002
FEATURE [App::DocumentObjectGroupPython] Cl_element023  label="Cl_element : 0.590"  # scripted group (container) (typed FeaturePython)
  n = 0.003
FEATURE [App::DocumentObjectGroupPython] K_element010  label="K_element : 0.001"  # scripted group (container) (typed FeaturePython)
  n = 0.001
FEATURE [App::DocumentObjectGroupPython] G4_SKIN_ICRP  # scripted group (container) (typed FeaturePython)
  Dunit = g/cm3
  Dvalue = 1.09
  Group = -> [H_element095,C_element103,N_element039,O_element088,Na_element013,P_element009,S_element020,Cl_element023,K_element010]
  conduct = 2
  density = 1
  expand = 3
  formula = G4_SKIN_ICRP
  name = G4_SKIN_ICRP
  specific = 4
FEATURE [App::DocumentObjectGroupPython] Na_element014  label="Na_element : 2"  # scripted group (container) (typed FeaturePython)
  n = 2
  ref = Na_element
FEATURE [App::DocumentObjectGroupPython] C_element104  label="C_element : 058"  # scripted group (container) (typed FeaturePython)
  n = 1
  ref = C_element
FEATURE [App::DocumentObjectGroupPython] O_element089  label="O_element : 049"  # scripted group (container) (typed FeaturePython)
  n = 3
  ref = O_element
FEATURE [App::DocumentObjectGroupPython] G4_SODIUM_CARBONATE  # scripted group (container) (typed FeaturePython)
  Dunit = g/cm3
  Dvalue = 2.532
  Group = -> [Na_element014,C_element104,O_element089]
  conduct = 2
  density = 1
  expand = 3
  formula = G4_SODIUM_CARBONATE
  name = G4_SODIUM_CARBONATE
  specific = 4
FEATURE [App::DocumentObjectGroupPython] Na_element015  label="Na_element : 1"  # scripted group (container) (typed FeaturePython)
  n = 1
  ref = Na_element
FEATURE [App::DocumentObjectGroupPython] I_element009  label="I_element : 005"  # scripted group (container) (typed FeaturePython)
  n = 1
  ref = I_element
FEATURE [App::DocumentObjectGroupPython] G4_SODIUM_IODIDE  # scripted group (container) (typed FeaturePython)
  Dunit = g/cm3
  Dvalue = 3.667
  Group = -> [Na_element015,I_element009]
  conduct = 2
  density = 1
  expand = 3
  formula = G4_SODIUM_IODIDE
  name = G4_SODIUM_IODIDE
  specific = 4
FEATURE [App::DocumentObjectGroupPython] Na_element016  label="Na_element : 003"  # scripted group (container) (typed FeaturePython)
  n = 2
  ref = Na_element
FEATURE [App::DocumentObjectGroupPython] O_element090  label="O_element : 050"  # scripted group (container) (typed FeaturePython)
  n = 1
  ref = O_element
FEATURE [App::DocumentObjectGroupPython] G4_SODIUM_MONOXIDE  # scripted group (container) (typed FeaturePython)
  Dunit = g/cm3
  Dvalue = 2.27
  Group = -> [Na_element016,O_element090]
  conduct = 2
  density = 1
  expand = 3
  formula = G4_SODIUM_MONOXIDE
  name = G4_SODIUM_MONOXIDE
  specific = 4
FEATURE [App::DocumentObjectGroupPython] Na_element017  label="Na_element : 004"  # scripted group (container) (typed FeaturePython)
  n = 1
  ref = Na_element
FEATURE [App::DocumentObjectGroupPython] N_element040  label="N_element : 018"  # scripted group (container) (typed FeaturePython)
  n = 1
  ref = N_element
FEATURE [App::DocumentObjectGroupPython] O_element091  label="O_element : 051"  # scripted group (container) (typed FeaturePython)
  n = 3
  ref = O_element
FEATURE [App::DocumentObjectGroupPython] G4_SODIUM_NITRATE  # scripted group (container) (typed FeaturePython)
  Dunit = g/cm3
  Dvalue = 2.261
  Group = -> [Na_element017,N_element040,O_element091]
  conduct = 2
  density = 1
  expand = 3
  formula = G4_SODIUM_NITRATE
  name = G4_SODIUM_NITRATE
  specific = 4
FEATURE [App::DocumentObjectGroupPython] C_element105  label="C_element : 059"  # scripted group (container) (typed FeaturePython)
  n = 14
  ref = C_element
FEATURE [App::DocumentObjectGroupPython] H_element096  label="H_element : 053"  # scripted group (container) (typed FeaturePython)
  n = 12
  ref = H_element
FEATURE [App::DocumentObjectGroupPython] G4_STILBENE  # scripted group (container) (typed FeaturePython)
  Dunit = g/cm3
  Dvalue = 0.9707
  Group = -> [C_element105,H_element096]
  conduct = 2
  density = 1
  expand = 3
  formula = G4_STILBENE
  name = G4_STILBENE
  specific = 4
FEATURE [App::DocumentObjectGroupPython] C_element106  label="C_element : 12"  # scripted group (container) (typed FeaturePython)
  n = 12
  ref = C_element
FEATURE [App::DocumentObjectGroupPython] H_element097  label="H_element : 22"  # scripted group (container) (typed FeaturePython)
  n = 22
  ref = H_element
FEATURE [App::DocumentObjectGroupPython] O_element092  label="O_element : 11"  # scripted group (container) (typed FeaturePython)
  n = 11
  ref = O_element
FEATURE [App::DocumentObjectGroupPython] G4_SUCROSE  # scripted group (container) (typed FeaturePython)
  Dunit = g/cm3
  Dvalue = 1.5805
  Group = -> [C_element106,H_element097,O_element092]
  conduct = 2
  density = 1
  expand = 3
  formula = G4_SUCROSE
  name = G4_SUCROSE
  specific = 4
FEATURE [App::DocumentObjectGroupPython] C_element107  label="C_element : 18"  # scripted group (container) (typed FeaturePython)
  n = 18
  ref = C_element
FEATURE [App::DocumentObjectGroupPython] H_element098  label="H_element : 054"  # scripted group (container) (typed FeaturePython)
  n = 14
  ref = H_element
FEATURE [App::DocumentObjectGroupPython] G4_TERPHENYL  # scripted group (container) (typed FeaturePython)
  Dunit = g/cm3
  Dvalue = 1.24
  Group = -> [C_element107,H_element098]
  conduct = 2
  density = 1
  expand = 3
  formula = G4_TERPHENYL
  name = G4_TERPHENYL
  specific = 4
FEATURE [App::DocumentObjectGroupPython] H_element099  label="H_element : 0.146"  # scripted group (container) (typed FeaturePython)
  n = 0.106
FEATURE [App::DocumentObjectGroupPython] C_element108  label="C_element : 0.883"  # scripted group (container) (typed FeaturePython)
  n = 0.099
FEATURE [App::DocumentObjectGroupPython] N_element041  label="N_element : 0.020"  # scripted group (container) (typed FeaturePython)
  n = 0.02
FEATURE [App::DocumentObjectGroupPython] O_element093  label="O_element : 0.766"  # scripted group (container) (typed FeaturePython)
  n = 0.766
FEATURE [App::DocumentObjectGroupPython] Na_element018  label="Na_element : 0.101"  # scripted group (container) (typed FeaturePython)
  n = 0.002
FEATURE [App::DocumentObjectGroupPython] P_element010  label="P_element : 0.108"  # scripted group (container) (typed FeaturePython)
  n = 0.001
FEATURE [App::DocumentObjectGroupPython] S_element021  label="S_element : 0.022"  # scripted group (container) (typed FeaturePython)
  n = 0.002
FEATURE [App::DocumentObjectGroupPython] Cl_element024  label="Cl_element : 0.002"  # scripted group (container) (typed FeaturePython)
  n = 0.002
FEATURE [App::DocumentObjectGroupPython] K_element011  label="K_element : 0.017"  # scripted group (container) (typed FeaturePython)
  n = 0.002
FEATURE [App::DocumentObjectGroupPython] G4_TESTIS_ICRP  # scripted group (container) (typed FeaturePython)
  Dunit = g/cm3
  Dvalue = 1.04
  Group = -> [H_element099,C_element108,N_element041,O_element093,Na_element018,P_element010,S_element021,Cl_element024,K_element011]
  conduct = 2
  density = 1
  expand = 3
  formula = G4_TESTIS_ICRP
  name = G4_TESTIS_ICRP
  specific = 4
FEATURE [App::DocumentObjectGroupPython] C_element109  label="C_element : 060"  # scripted group (container) (typed FeaturePython)
  n = 2
  ref = C_element
FEATURE [App::DocumentObjectGroupPython] Cl_element025  label="Cl_element : 012"  # scripted group (container) (typed FeaturePython)
  n = 4
  ref = Cl_element
FEATURE [App::DocumentObjectGroupPython] G4_TETRACHLOROETHYLENE  # scripted group (container) (typed FeaturePython)
  Dunit = g/cm3
  Dvalue = 1.625
  Group = -> [C_element109,Cl_element025]
  conduct = 2
  density = 1
  expand = 3
  formula = G4_TETRACHLOROETHYLENE
  name = G4_TETRACHLOROETHYLENE
  specific = 4
FEATURE [App::DocumentObjectGroupPython] Tl_element001  label="Tl_element : 1"  # scripted group (container) (typed FeaturePython)
  n = 1
  ref = Tl_element
FEATURE [App::DocumentObjectGroupPython] Cl_element026  label="Cl_element : 013"  # scripted group (container) (typed FeaturePython)
  n = 1
  ref = Cl_element
FEATURE [App::DocumentObjectGroupPython] G4_THALLIUM_CHLORIDE  # scripted group (container) (typed FeaturePython)
  Dunit = g/cm3
  Dvalue = 7.004
  Group = -> [Tl_element001,Cl_element026]
  conduct = 2
  density = 1
  expand = 3
  formula = G4_THALLIUM_CHLORIDE
  name = G4_THALLIUM_CHLORIDE
  specific = 4
FEATURE [App::DocumentObjectGroupPython] H_element100  label="H_element : 0.147"  # scripted group (container) (typed FeaturePython)
  n = 0.105
FEATURE [App::DocumentObjectGroupPython] C_element110  label="C_element : 0.256"  # scripted group (container) (typed FeaturePython)
  n = 0.256
FEATURE [App::DocumentObjectGroupPython] N_element042  label="N_element : 0.760"  # scripted group (container) (typed FeaturePython)
  n = 0.027
FEATURE [App::DocumentObjectGroupPython] O_element094  label="O_element : 0.602"  # scripted group (container) (typed FeaturePython)
  n = 0.602
FEATURE [App::DocumentObjectGroupPython] Na_element019  label="Na_element : 0.102"  # scripted group (container) (typed FeaturePython)
  n = 0.001
FEATURE [App::DocumentObjectGroupPython] P_element011  label="P_element : 0.109"  # scripted group (container) (typed FeaturePython)
  n = 0.002
FEATURE [App::DocumentObjectGroupPython] S_element022  label="S_element : 0.023"  # scripted group (container) (typed FeaturePython)
  n = 0.003
FEATURE [App::DocumentObjectGroupPython] Cl_element027  label="Cl_element : 0.591"  # scripted group (container) (typed FeaturePython)
  n = 0.002
FEATURE [App::DocumentObjectGroupPython] K_element012  label="K_element : 0.018"  # scripted group (container) (typed FeaturePython)
  n = 0.002
FEATURE [App::DocumentObjectGroupPython] G4_TISSUE_SOFT_ICRP  # scripted group (container) (typed FeaturePython)
  Dunit = g/cm3
  Dvalue = 1.03
  Group = -> [H_element100,C_element110,N_element042,O_element094,Na_element019,P_element011,S_element022,Cl_element027,K_element012]
  conduct = 2
  density = 1
  expand = 3
  formula = G4_TISSUE_SOFT_ICRP
  name = G4_TISSUE_SOFT_ICRP
  specific = 4
FEATURE [App::DocumentObjectGroupPython] H_element101  label="H_element : 0.148"  # scripted group (container) (typed FeaturePython)
  n = 0.101
FEATURE [App::DocumentObjectGroupPython] C_element111  label="C_element : 0.111"  # scripted group (container) (typed FeaturePython)
  n = 0.111
FEATURE [App::DocumentObjectGroupPython] N_element043  label="N_element : 0.026"  # scripted group (container) (typed FeaturePython)
  n = 0.026
FEATURE [App::DocumentObjectGroupPython] O_element095  label="O_element : 0.762"  # scripted group (container) (typed FeaturePython)
  n = 0.762
FEATURE [App::DocumentObjectGroupPython] G4_TISSUE_SOFT_ICRU_4  label="G4_TISSUE_SOFT_ICRU-4"  # scripted group (container) (typed FeaturePython)
  Dunit = g/cm3
  Dvalue = 1
  Group = -> [H_element101,C_element111,N_element043,O_element095]
  conduct = 2
  density = 1
  expand = 3
  formula = G4_TISSUE_SOFT_ICRU-4
  name = G4_TISSUE_SOFT_ICRU-4
  specific = 4
FEATURE [App::DocumentObjectGroupPython] H_element102  label="H_element : 0.149"  # scripted group (container) (typed FeaturePython)
  n = 0.101869
FEATURE [App::DocumentObjectGroupPython] C_element112  label="C_element : 0.456"  # scripted group (container) (typed FeaturePython)
  n = 0.456179
FEATURE [App::DocumentObjectGroupPython] N_element044  label="N_element : 0.761"  # scripted group (container) (typed FeaturePython)
  n = 0.035172
FEATURE [App::DocumentObjectGroupPython] O_element096  label="O_element : 0.407"  # scripted group (container) (typed FeaturePython)
  n = 0.40678
FEATURE [App::DocumentObjectGroupPython] G4_TISSUE_METHANE  label="G4_TISSUE-METHANE"  # scripted group (container) (typed FeaturePython)
  Dunit = g/cm3
  Dvalue = 0.00106409
  Group = -> [H_element102,C_element112,N_element044,O_element096]
  conduct = 2
  density = 1
  expand = 3
  formula = G4_TISSUE-METHANE
  name = G4_TISSUE-METHANE
  specific = 4
FEATURE [App::DocumentObjectGroupPython] H_element103  label="H_element : 0.103"  # scripted group (container) (typed FeaturePython)
  n = 0.102672
FEATURE [App::DocumentObjectGroupPython] C_element113  label="C_element : 0.569"  # scripted group (container) (typed FeaturePython)
  n = 0.56894
FEATURE [App::DocumentObjectGroupPython] N_element045  label="N_element : 0.762"  # scripted group (container) (typed FeaturePython)
  n = 0.035022
FEATURE [App::DocumentObjectGroupPython] O_element097  label="O_element : 0.293"  # scripted group (container) (typed FeaturePython)
  n = 0.293366
FEATURE [App::DocumentObjectGroupPython] G4_TISSUE_PROPANE  label="G4_TISSUE-PROPANE"  # scripted group (container) (typed FeaturePython)
  Dunit = g/cm3
  Dvalue = 0.00182628
  Group = -> [H_element103,C_element113,N_element045,O_element097]
  conduct = 2
  density = 1
  expand = 3
  formula = G4_TISSUE-PROPANE
  name = G4_TISSUE-PROPANE
  specific = 4
FEATURE [App::DocumentObjectGroupPython] Ti_element003  label="Ti_element : 1"  # scripted group (container) (typed FeaturePython)
  n = 1
  ref = Ti_element
FEATURE [App::DocumentObjectGroupPython] O_element098  label="O_element : 052"  # scripted group (container) (typed FeaturePython)
  n = 2
  ref = O_element
FEATURE [App::DocumentObjectGroupPython] G4_TITANIUM_DIOXIDE  # scripted group (container) (typed FeaturePython)
  Dunit = g/cm3
  Dvalue = 4.26
  Group = -> [Ti_element003,O_element098]
  conduct = 2
  density = 1
  expand = 3
  formula = G4_TITANIUM_DIOXIDE
  name = G4_TITANIUM_DIOXIDE
  specific = 4
FEATURE [App::DocumentObjectGroupPython] C_element114  label="C_element : 061"  # scripted group (container) (typed FeaturePython)
  n = 7
  ref = C_element
FEATURE [App::DocumentObjectGroupPython] H_element104  label="H_element : 055"  # scripted group (container) (typed FeaturePython)
  n = 8
  ref = H_element
FEATURE [App::DocumentObjectGroupPython] G4_TOLUENE  # scripted group (container) (typed FeaturePython)
  Dunit = g/cm3
  Dvalue = 0.8669
  Group = -> [C_element114,H_element104]
  conduct = 2
  density = 1
  expand = 3
  formula = G4_TOLUENE
  name = G4_TOLUENE
  specific = 4
FEATURE [App::DocumentObjectGroupPython] C_element115  label="C_element : 062"  # scripted group (container) (typed FeaturePython)
  n = 2
  ref = C_element
FEATURE [App::DocumentObjectGroupPython] H_element105  label="H_element : 056"  # scripted group (container) (typed FeaturePython)
  n = 1
  ref = H_element
FEATURE [App::DocumentObjectGroupPython] Cl_element028  label="Cl_element : 014"  # scripted group (container) (typed FeaturePython)
  n = 3
  ref = Cl_element
FEATURE [App::DocumentObjectGroupPython] G4_TRICHLOROETHYLENE  # scripted group (container) (typed FeaturePython)
  Dunit = g/cm3
  Dvalue = 1.46
  Group = -> [C_element115,H_element105,Cl_element028]
  conduct = 2
  density = 1
  expand = 3
  formula = G4_TRICHLOROETHYLENE
  name = G4_TRICHLOROETHYLENE
  specific = 4
FEATURE [App::DocumentObjectGroupPython] C_element116  label="C_element : 063"  # scripted group (container) (typed FeaturePython)
  n = 6
  ref = C_element
FEATURE [App::DocumentObjectGroupPython] H_element106  label="H_element : 15"  # scripted group (container) (typed FeaturePython)
  n = 15
  ref = H_element
FEATURE [App::DocumentObjectGroupPython] O_element099  label="O_element : 053"  # scripted group (container) (typed FeaturePython)
  n = 4
  ref = O_element
FEATURE [App::DocumentObjectGroupPython] P_element012  label="P_element : 1"  # scripted group (container) (typed FeaturePython)
  n = 1
  ref = P_element
FEATURE [App::DocumentObjectGroupPython] G4_TRIETHYL_PHOSPHATE  # scripted group (container) (typed FeaturePython)
  Dunit = g/cm3
  Dvalue = 1.07
  Group = -> [C_element116,H_element106,O_element099,P_element012]
  conduct = 2
  density = 1
  expand = 3
  formula = G4_TRIETHYL_PHOSPHATE
  name = G4_TRIETHYL_PHOSPHATE
  specific = 4
FEATURE [App::DocumentObjectGroupPython] W_element003  label="W_element : 003"  # scripted group (container) (typed FeaturePython)
  n = 1
  ref = W_element
FEATURE [App::DocumentObjectGroupPython] F_element017  label="F_element : 6"  # scripted group (container) (typed FeaturePython)
  n = 6
  ref = F_element
FEATURE [App::DocumentObjectGroupPython] G4_TUNGSTEN_HEXAFLUORIDE  # scripted group (container) (typed FeaturePython)
  Dunit = g/cm3
  Dvalue = 2.4
  Group = -> [W_element003,F_element017]
  conduct = 2
  density = 1
  expand = 3
  formula = G4_TUNGSTEN_HEXAFLUORIDE
  name = G4_TUNGSTEN_HEXAFLUORIDE
  specific = 4
FEATURE [App::DocumentObjectGroupPython] U_element001  label="U_element : 1"  # scripted group (container) (typed FeaturePython)
  n = 1
  ref = U_element
FEATURE [App::DocumentObjectGroupPython] C_element117  label="C_element : 064"  # scripted group (container) (typed FeaturePython)
  n = 2
  ref = C_element
FEATURE [App::DocumentObjectGroupPython] G4_URANIUM_DICARBIDE  # scripted group (container) (typed FeaturePython)
  Dunit = g/cm3
  Dvalue = 11.28
  Group = -> [U_element001,C_element117]
  conduct = 2
  density = 1
  expand = 3
  formula = G4_URANIUM_DICARBIDE
  name = G4_URANIUM_DICARBIDE
  specific = 4
FEATURE [App::DocumentObjectGroupPython] U_element002  label="U_element : 002"  # scripted group (container) (typed FeaturePython)
  n = 1
  ref = U_element
FEATURE [App::DocumentObjectGroupPython] C_element118  label="C_element : 065"  # scripted group (container) (typed FeaturePython)
  n = 1
  ref = C_element
FEATURE [App::DocumentObjectGroupPython] G4_URANIUM_MONOCARBIDE  # scripted group (container) (typed FeaturePython)
  Dunit = g/cm3
  Dvalue = 13.63
  Group = -> [U_element002,C_element118]
  conduct = 2
  density = 1
  expand = 3
  formula = G4_URANIUM_MONOCARBIDE
  name = G4_URANIUM_MONOCARBIDE
  specific = 4
FEATURE [App::DocumentObjectGroupPython] U_element003  label="U_element : 003"  # scripted group (container) (typed FeaturePython)
  n = 1
  ref = U_element
FEATURE [App::DocumentObjectGroupPython] O_element100  label="O_element : 054"  # scripted group (container) (typed FeaturePython)
  n = 2
  ref = O_element
FEATURE [App::DocumentObjectGroupPython] G4_URANIUM_OXIDE  # scripted group (container) (typed FeaturePython)
  Dunit = g/cm3
  Dvalue = 10.96
  Group = -> [U_element003,O_element100]
  conduct = 2
  density = 1
  expand = 3
  formula = G4_URANIUM_OXIDE
  name = G4_URANIUM_OXIDE
  specific = 4
FEATURE [App::DocumentObjectGroupPython] C_element119  label="C_element : 066"  # scripted group (container) (typed FeaturePython)
  n = 1
  ref = C_element
FEATURE [App::DocumentObjectGroupPython] H_element107  label="H_element : 057"  # scripted group (container) (typed FeaturePython)
  n = 4
  ref = H_element
FEATURE [App::DocumentObjectGroupPython] N_element046  label="N_element : 019"  # scripted group (container) (typed FeaturePython)
  n = 2
  ref = N_element
FEATURE [App::DocumentObjectGroupPython] O_element101  label="O_element : 055"  # scripted group (container) (typed FeaturePython)
  n = 1
  ref = O_element
FEATURE [App::DocumentObjectGroupPython] G4_UREA  # scripted group (container) (typed FeaturePython)
  Dunit = g/cm3
  Dvalue = 1.323
  Group = -> [C_element119,H_element107,N_element046,O_element101]
  conduct = 2
  density = 1
  expand = 3
  formula = G4_UREA
  name = G4_UREA
  specific = 4
FEATURE [App::DocumentObjectGroupPython] C_element120  label="C_element : 067"  # scripted group (container) (typed FeaturePython)
  n = 5
  ref = C_element
FEATURE [App::DocumentObjectGroupPython] H_element108  label="H_element : 058"  # scripted group (container) (typed FeaturePython)
  n = 11
  ref = H_element
FEATURE [App::DocumentObjectGroupPython] N_element047  label="N_element : 020"  # scripted group (container) (typed FeaturePython)
  n = 1
  ref = N_element
FEATURE [App::DocumentObjectGroupPython] O_element102  label="O_element : 056"  # scripted group (container) (typed FeaturePython)
  n = 2
  ref = O_element
FEATURE [App::DocumentObjectGroupPython] G4_VALINE  # scripted group (container) (typed FeaturePython)
  Dunit = g/cm3
  Dvalue = 1.23
  Group = -> [C_element120,H_element108,N_element047,O_element102]
  conduct = 2
  density = 1
  expand = 3
  formula = G4_VALINE
  name = G4_VALINE
  specific = 4
FEATURE [App::DocumentObjectGroupPython] H_element109  label="H_element : 0.009"  # scripted group (container) (typed FeaturePython)
  n = 0.009417
FEATURE [App::DocumentObjectGroupPython] C_element121  label="C_element : 0.281"  # scripted group (container) (typed FeaturePython)
  n = 0.280555
FEATURE [App::DocumentObjectGroupPython] F_element018  label="F_element : 0.710"  # scripted group (container) (typed FeaturePython)
  n = 0.710028
FEATURE [App::DocumentObjectGroupPython] G4_VITON  # scripted group (container) (typed FeaturePython)
  Dunit = g/cm3
  Dvalue = 1.8
  Group = -> [H_element109,C_element121,F_element018]
  conduct = 2
  density = 1
  expand = 3
  formula = G4_VITON
  name = G4_VITON
  specific = 4
FEATURE [App::DocumentObjectGroupPython] H_element110  label="H_element : 059"  # scripted group (container) (typed FeaturePython)
  n = 2
  ref = H_element
FEATURE [App::DocumentObjectGroupPython] O_element103  label="O_element : 057"  # scripted group (container) (typed FeaturePython)
  n = 1
  ref = O_element
FEATURE [App::DocumentObjectGroupPython] G4_WATER  # scripted group (container) (typed FeaturePython)
  Dunit = g/cm3
  Dvalue = 1
  Group = -> [H_element110,O_element103]
  conduct = 2
  density = 1
  expand = 3
  formula = G4_WATER
  name = G4_WATER
  specific = 4
FEATURE [App::DocumentObjectGroupPython] H_element111  label="H_element : 060"  # scripted group (container) (typed FeaturePython)
  n = 2
  ref = H_element
FEATURE [App::DocumentObjectGroupPython] O_element104  label="O_element : 058"  # scripted group (container) (typed FeaturePython)
  n = 1
  ref = O_element
FEATURE [App::DocumentObjectGroupPython] G4_WATER_VAPOR  # scripted group (container) (typed FeaturePython)
  Dunit = g/cm3
  Dvalue = 0.000756182
  Group = -> [H_element111,O_element104]
  conduct = 2
  density = 1
  expand = 3
  formula = G4_WATER_VAPOR
  name = G4_WATER_VAPOR
  specific = 4
FEATURE [App::DocumentObjectGroupPython] C_element122  label="C_element : 068"  # scripted group (container) (typed FeaturePython)
  n = 8
  ref = C_element
FEATURE [App::DocumentObjectGroupPython] H_element112  label="H_element : 061"  # scripted group (container) (typed FeaturePython)
  n = 10
  ref = H_element
FEATURE [App::DocumentObjectGroupPython] G4_XYLENE  # scripted group (container) (typed FeaturePython)
  Dunit = g/cm3
  Dvalue = 0.87
  Group = -> [C_element122,H_element112]
  conduct = 2
  density = 1
  expand = 3
  formula = G4_XYLENE
  name = G4_XYLENE
  specific = 4
FEATURE [App::DocumentObjectGroupPython] C_element123  label="C_element : 069"  # scripted group (container) (typed FeaturePython)
  n = 1
  ref = C_element
FEATURE [App::DocumentObjectGroupPython] G4_GRAPHITE  # scripted group (container) (typed FeaturePython)
  Dunit = g/cm3
  Dvalue = 2.21
  Group = -> [C_element123]
  conduct = 2
  density = 1
  expand = 3
  formula = G4_GRAPHITE
  name = G4_GRAPHITE
  specific = 4
FEATURE [App::DocumentObjectGroupPython] NIST  # scripted group (container) (typed FeaturePython)
  Group = -> [G4_A_150_TISSUE,G4_ACETONE,G4_ACETYLENE,G4_ADENINE,G4_ADIPOSE_TISSUE_ICRP,G4_AIR,G4_ALANINE,G4_ALUMINUM_OXIDE,G4_AMBER,G4_AMMONIA,G4_ANILINE,G4_ANTHRACENE,G4_B_100_BONE,G4_BAKELITE,G4_BARIUM_FLUORIDE,G4_BARIUM_SULFATE,G4_BENZENE,G4_BERYLLIUM_OXIDE,G4_BGO,G4_BLOOD_ICRP,G4_BONE_COMPACT_ICRU,G4_BONE_CORTICAL_ICRP,G4_BORON_CARBIDE,G4_BORON_OXIDE,G4_BRAIN_ICRP,G4_BUTANE,G4_N_BUTYL_ALCOHOL,G4_C_552,+152 more]
FEATURE [App::DocumentObjectGroupPython] H_element113  label="H_element : 062"  # scripted group (container) (typed FeaturePython)
  n = 1
  ref = H_element
FEATURE [App::DocumentObjectGroupPython] G4_H  # scripted group (container) (typed FeaturePython)
  Dunit = g/cm3
  Dvalue = 8.3748e-05
  Group = -> [H_element113]
  conduct = 2
  density = 1
  expand = 3
  formula = H
  name = G4_H
  specific = 4
FEATURE [App::DocumentObjectGroupPython] He_element001  label="He_element : 1"  # scripted group (container) (typed FeaturePython)
  n = 1
  ref = He_element
FEATURE [App::DocumentObjectGroupPython] G4_He  # scripted group (container) (typed FeaturePython)
  Dunit = g/cm3
  Dvalue = 0.000166322
  Group = -> [He_element001]
  conduct = 2
  density = 1
  expand = 3
  formula = He
  name = G4_He
  specific = 4
FEATURE [App::DocumentObjectGroupPython] Li_element008  label="Li_element : 008"  # scripted group (container) (typed FeaturePython)
  n = 1
  ref = Li_element
FEATURE [App::DocumentObjectGroupPython] G4_Li  # scripted group (container) (typed FeaturePython)
  Dunit = g/cm3
  Dvalue = 0.534
  Group = -> [Li_element008]
  conduct = 2
  density = 1
  expand = 3
  formula = Li
  name = G4_Li
  specific = 4
FEATURE [App::DocumentObjectGroupPython] Be_element002  label="Be_element : 002"  # scripted group (container) (typed FeaturePython)
  n = 1
  ref = Be_element
FEATURE [App::DocumentObjectGroupPython] G4_Be  # scripted group (container) (typed FeaturePython)
  Dunit = g/cm3
  Dvalue = 1.848
  Group = -> [Be_element002]
  conduct = 2
  density = 1
  expand = 3
  formula = Be
  name = G4_Be
  specific = 4
FEATURE [App::DocumentObjectGroupPython] B_element007  label="B_element : 007"  # scripted group (container) (typed FeaturePython)
  n = 1
  ref = B_element
FEATURE [App::DocumentObjectGroupPython] G4_B  # scripted group (container) (typed FeaturePython)
  Dunit = g/cm3
  Dvalue = 2.37
  Group = -> [B_element007]
  conduct = 2
  density = 1
  expand = 3
  formula = B
  name = G4_B
  specific = 4
FEATURE [App::DocumentObjectGroupPython] C_element124  label="C_element : 070"  # scripted group (container) (typed FeaturePython)
  n = 1
  ref = C_element
FEATURE [App::DocumentObjectGroupPython] G4_C  # scripted group (container) (typed FeaturePython)
  Dunit = g/cm3
  Dvalue = 2
  Group = -> [C_element124]
  conduct = 2
  density = 1
  expand = 3
  formula = C
  name = G4_C
  specific = 4
FEATURE [App::DocumentObjectGroupPython] N_element048  label="N_element : 021"  # scripted group (container) (typed FeaturePython)
  n = 1
  ref = N_element
FEATURE [App::DocumentObjectGroupPython] G4_N  # scripted group (container) (typed FeaturePython)
  Dunit = g/cm3
  Dvalue = 0.0011652
  Group = -> [N_element048]
  conduct = 2
  density = 1
  expand = 3
  formula = N
  name = G4_N
  specific = 4
FEATURE [App::DocumentObjectGroupPython] O_element105  label="O_element : 059"  # scripted group (container) (typed FeaturePython)
  n = 1
  ref = O_element
FEATURE [App::DocumentObjectGroupPython] G4_O  # scripted group (container) (typed FeaturePython)
  Dunit = g/cm3
  Dvalue = 0.00133151
  Group = -> [O_element105]
  conduct = 2
  density = 1
  expand = 3
  formula = O
  name = G4_O
  specific = 4
FEATURE [App::DocumentObjectGroupPython] F_element019  label="F_element : 008"  # scripted group (container) (typed FeaturePython)
  n = 1
  ref = F_element
FEATURE [App::DocumentObjectGroupPython] G4_F  # scripted group (container) (typed FeaturePython)
  Dunit = g/cm3
  Dvalue = 0.00158029
  Group = -> [F_element019]
  conduct = 2
  density = 1
  expand = 3
  formula = F
  name = G4_F
  specific = 4
FEATURE [App::DocumentObjectGroupPython] Ne_element001  label="Ne_element : 1"  # scripted group (container) (typed FeaturePython)
  n = 1
  ref = Ne_element
FEATURE [App::DocumentObjectGroupPython] G4_Ne  # scripted group (container) (typed FeaturePython)
  Dunit = g/cm3
  Dvalue = 0.000838505
  Group = -> [Ne_element001]
  conduct = 2
  density = 1
  expand = 3
  formula = Ne
  name = G4_Ne
  specific = 4
FEATURE [App::DocumentObjectGroupPython] Na_element020  label="Na_element : 005"  # scripted group (container) (typed FeaturePython)
  n = 1
  ref = Na_element
FEATURE [App::DocumentObjectGroupPython] G4_Na  # scripted group (container) (typed FeaturePython)
  Dunit = g/cm3
  Dvalue = 0.971
  Group = -> [Na_element020]
  conduct = 2
  density = 1
  expand = 3
  formula = Na
  name = G4_Na
  specific = 4
FEATURE [App::DocumentObjectGroupPython] Mg_element011  label="Mg_element : 005"  # scripted group (container) (typed FeaturePython)
  n = 1
  ref = Mg_element
FEATURE [App::DocumentObjectGroupPython] G4_Mg  # scripted group (container) (typed FeaturePython)
  Dunit = g/cm3
  Dvalue = 1.74
  Group = -> [Mg_element011]
  conduct = 2
  density = 1
  expand = 3
  formula = Mg
  name = G4_Mg
  specific = 4
FEATURE [App::DocumentObjectGroupPython] Al_element004  label="Al_element : 1"  # scripted group (container) (typed FeaturePython)
  n = 1
  ref = Al_element
FEATURE [App::DocumentObjectGroupPython] G4_Al  # scripted group (container) (typed FeaturePython)
  Dunit = g/cm3
  Dvalue = 2.699
  Group = -> [Al_element004]
  conduct = 2
  density = 1
  expand = 3
  formula = Al
  name = G4_Al
  specific = 4
FEATURE [App::DocumentObjectGroupPython] Si_element007  label="Si_element : 002"  # scripted group (container) (typed FeaturePython)
  n = 1
  ref = Si_element
FEATURE [App::DocumentObjectGroupPython] G4_Si  # scripted group (container) (typed FeaturePython)
  Dunit = g/cm3
  Dvalue = 2.33
  Group = -> [Si_element007]
  conduct = 2
  density = 1
  expand = 3
  formula = Si
  name = G4_Si
  specific = 4
FEATURE [App::DocumentObjectGroupPython] P_element013  label="P_element : 002"  # scripted group (container) (typed FeaturePython)
  n = 1
  ref = P_element
FEATURE [App::DocumentObjectGroupPython] G4_P  # scripted group (container) (typed FeaturePython)
  Dunit = g/cm3
  Dvalue = 2.2
  Group = -> [P_element013]
  conduct = 2
  density = 1
  expand = 3
  formula = P
  name = G4_P
  specific = 4
FEATURE [App::DocumentObjectGroupPython] S_element023  label="S_element : 007"  # scripted group (container) (typed FeaturePython)
  n = 1
  ref = S_element
FEATURE [App::DocumentObjectGroupPython] G4_S  # scripted group (container) (typed FeaturePython)
  Dunit = g/cm3
  Dvalue = 2
  Group = -> [S_element023]
  conduct = 2
  density = 1
  expand = 3
  formula = S
  name = G4_S
  specific = 4
FEATURE [App::DocumentObjectGroupPython] Cl_element029  label="Cl_element : 015"  # scripted group (container) (typed FeaturePython)
  n = 1
  ref = Cl_element
FEATURE [App::DocumentObjectGroupPython] G4_Cl  # scripted group (container) (typed FeaturePython)
  Dunit = g/cm3
  Dvalue = 0.00299473
  Group = -> [Cl_element029]
  conduct = 2
  density = 1
  expand = 3
  formula = Cl
  name = G4_Cl
  specific = 4
FEATURE [App::DocumentObjectGroupPython] Ar_element002  label="Ar_element : 1"  # scripted group (container) (typed FeaturePython)
  n = 1
  ref = Ar_element
FEATURE [App::DocumentObjectGroupPython] G4_Ar  # scripted group (container) (typed FeaturePython)
  Dunit = g/cm3
  Dvalue = 0.00166201
  Group = -> [Ar_element002]
  conduct = 2
  density = 1
  expand = 3
  formula = Ar
  name = G4_Ar
  specific = 4
FEATURE [App::DocumentObjectGroupPython] K_element013  label="K_element : 003"  # scripted group (container) (typed FeaturePython)
  n = 1
  ref = K_element
FEATURE [App::DocumentObjectGroupPython] G4_K  # scripted group (container) (typed FeaturePython)
  Dunit = g/cm3
  Dvalue = 0.862
  Group = -> [K_element013]
  conduct = 2
  density = 1
  expand = 3
  formula = K
  name = G4_K
  specific = 4
FEATURE [App::DocumentObjectGroupPython] Ca_element014  label="Ca_element : 007"  # scripted group (container) (typed FeaturePython)
  n = 1
  ref = Ca_element
FEATURE [App::DocumentObjectGroupPython] G4_Ca  # scripted group (container) (typed FeaturePython)
  Dunit = g/cm3
  Dvalue = 1.55
  Group = -> [Ca_element014]
  conduct = 2
  density = 1
  expand = 3
  formula = Ca
  name = G4_Ca
  specific = 4
FEATURE [App::DocumentObjectGroupPython] Sc_element001  label="Sc_element : 1"  # scripted group (container) (typed FeaturePython)
  n = 1
  ref = Sc_element
FEATURE [App::DocumentObjectGroupPython] G4_Sc  # scripted group (container) (typed FeaturePython)
  Dunit = g/cm3
  Dvalue = 2.989
  Group = -> [Sc_element001]
  conduct = 2
  density = 1
  expand = 3
  formula = Sc
  name = G4_Sc
  specific = 4
FEATURE [App::DocumentObjectGroupPython] Ti_element004  label="Ti_element : 002"  # scripted group (container) (typed FeaturePython)
  n = 1
  ref = Ti_element
FEATURE [App::DocumentObjectGroupPython] G4_Ti  # scripted group (container) (typed FeaturePython)
  Dunit = g/cm3
  Dvalue = 4.54
  Group = -> [Ti_element004]
  conduct = 2
  density = 1
  expand = 3
  formula = Ti
  name = G4_Ti
  specific = 4
FEATURE [App::DocumentObjectGroupPython] V_element001  label="V_element : 1"  # scripted group (container) (typed FeaturePython)
  n = 1
  ref = V_element
FEATURE [App::DocumentObjectGroupPython] G4_V  # scripted group (container) (typed FeaturePython)
  Dunit = g/cm3
  Dvalue = 6.11
  Group = -> [V_element001]
  conduct = 2
  density = 1
  expand = 3
  formula = V
  name = G4_V
  specific = 4
FEATURE [App::DocumentObjectGroupPython] Cr_element001  label="Cr_element : 1"  # scripted group (container) (typed FeaturePython)
  n = 1
  ref = Cr_element
FEATURE [App::DocumentObjectGroupPython] G4_Cr  # scripted group (container) (typed FeaturePython)
  Dunit = g/cm3
  Dvalue = 7.18
  Group = -> [Cr_element001]
  conduct = 2
  density = 1
  expand = 3
  formula = Cr
  name = G4_Cr
  specific = 4
FEATURE [App::DocumentObjectGroupPython] Mn_element001  label="Mn_element : 1"  # scripted group (container) (typed FeaturePython)
  n = 1
  ref = Mn_element
FEATURE [App::DocumentObjectGroupPython] G4_Mn  # scripted group (container) (typed FeaturePython)
  Dunit = g/cm3
  Dvalue = 7.44
  Group = -> [Mn_element001]
  conduct = 2
  density = 1
  expand = 3
  formula = Mn
  name = G4_Mn
  specific = 4
FEATURE [App::DocumentObjectGroupPython] Fe_element007  label="Fe_element : 004"  # scripted group (container) (typed FeaturePython)
  n = 1
  ref = Fe_element
FEATURE [App::DocumentObjectGroupPython] G4_Fe  # scripted group (container) (typed FeaturePython)
  Dunit = g/cm3
  Dvalue = 7.874
  Group = -> [Fe_element007]
  conduct = 2
  density = 1
  expand = 3
  formula = Fe
  name = G4_Fe
  specific = 4
FEATURE [App::DocumentObjectGroupPython] Co_element001  label="Co_element : 1"  # scripted group (container) (typed FeaturePython)
  n = 1
  ref = Co_element
FEATURE [App::DocumentObjectGroupPython] G4_Co  # scripted group (container) (typed FeaturePython)
  Dunit = g/cm3
  Dvalue = 8.9
  Group = -> [Co_element001]
  conduct = 2
  density = 1
  expand = 3
  formula = Co
  name = G4_Co
  specific = 4
FEATURE [App::DocumentObjectGroupPython] Ni_element001  label="Ni_element : 1"  # scripted group (container) (typed FeaturePython)
  n = 1
  ref = Ni_element
FEATURE [App::DocumentObjectGroupPython] G4_Ni  # scripted group (container) (typed FeaturePython)
  Dunit = g/cm3
  Dvalue = 8.902
  Group = -> [Ni_element001]
  conduct = 2
  density = 1
  expand = 3
  formula = Ni
  name = G4_Ni
  specific = 4
FEATURE [App::DocumentObjectGroupPython] Cu_element001  label="Cu_element : 1"  # scripted group (container) (typed FeaturePython)
  n = 1
  ref = Cu_element
FEATURE [App::DocumentObjectGroupPython] G4_Cu  # scripted group (container) (typed FeaturePython)
  Dunit = g/cm3
  Dvalue = 8.96
  Group = -> [Cu_element001]
  conduct = 2
  density = 1
  expand = 3
  formula = Cu
  name = G4_Cu
  specific = 4
FEATURE [App::DocumentObjectGroupPython] Zn_element001  label="Zn_element : 1"  # scripted group (container) (typed FeaturePython)
  n = 1
  ref = Zn_element
FEATURE [App::DocumentObjectGroupPython] G4_Zn  # scripted group (container) (typed FeaturePython)
  Dunit = g/cm3
  Dvalue = 7.133
  Group = -> [Zn_element001]
  conduct = 2
  density = 1
  expand = 3
  formula = Zn
  name = G4_Zn
  specific = 4
FEATURE [App::DocumentObjectGroupPython] Ga_element002  label="Ga_element : 002"  # scripted group (container) (typed FeaturePython)
  n = 1
  ref = Ga_element
FEATURE [App::DocumentObjectGroupPython] G4_Ga  # scripted group (container) (typed FeaturePython)
  Dunit = g/cm3
  Dvalue = 5.904
  Group = -> [Ga_element002]
  conduct = 2
  density = 1
  expand = 3
  formula = Ga
  name = G4_Ga
  specific = 4
FEATURE [App::DocumentObjectGroupPython] Ge_element002  label="Ge_element : 1"  # scripted group (container) (typed FeaturePython)
  n = 1
  ref = Ge_element
FEATURE [App::DocumentObjectGroupPython] G4_Ge  # scripted group (container) (typed FeaturePython)
  Dunit = g/cm3
  Dvalue = 5.323
  Group = -> [Ge_element002]
  conduct = 2
  density = 1
  expand = 3
  formula = Ge
  name = G4_Ge
  specific = 4
FEATURE [App::DocumentObjectGroupPython] As_element003  label="As_element : 002"  # scripted group (container) (typed FeaturePython)
  n = 1
  ref = As_element
FEATURE [App::DocumentObjectGroupPython] G4_As  # scripted group (container) (typed FeaturePython)
  Dunit = g/cm3
  Dvalue = 5.73
  Group = -> [As_element003]
  conduct = 2
  density = 1
  expand = 3
  formula = As
  name = G4_As
  specific = 4
FEATURE [App::DocumentObjectGroupPython] Se_element001  label="Se_element : 1"  # scripted group (container) (typed FeaturePython)
  n = 1
  ref = Se_element
FEATURE [App::DocumentObjectGroupPython] G4_Se  # scripted group (container) (typed FeaturePython)
  Dunit = g/cm3
  Dvalue = 4.5
  Group = -> [Se_element001]
  conduct = 2
  density = 1
  expand = 3
  formula = Se
  name = G4_Se
  specific = 4
FEATURE [App::DocumentObjectGroupPython] Br_element007  label="Br_element : 004"  # scripted group (container) (typed FeaturePython)
  n = 1
  ref = Br_element
FEATURE [App::DocumentObjectGroupPython] G4_Br  # scripted group (container) (typed FeaturePython)
  Dunit = g/cm3
  Dvalue = 0.0070721
  Group = -> [Br_element007]
  conduct = 2
  density = 1
  expand = 3
  formula = Br
  name = G4_Br
  specific = 4
FEATURE [App::DocumentObjectGroupPython] Kr_element001  label="Kr_element : 1"  # scripted group (container) (typed FeaturePython)
  n = 1
  ref = Kr_element
FEATURE [App::DocumentObjectGroupPython] G4_Kr  # scripted group (container) (typed FeaturePython)
  Dunit = g/cm3
  Dvalue = 0.00347832
  Group = -> [Kr_element001]
  conduct = 2
  density = 1
  expand = 3
  formula = Kr
  name = G4_Kr
  specific = 4
FEATURE [App::DocumentObjectGroupPython] Rb_element001  label="Rb_element : 1"  # scripted group (container) (typed FeaturePython)
  n = 1
  ref = Rb_element
FEATURE [App::DocumentObjectGroupPython] G4_Rb  # scripted group (container) (typed FeaturePython)
  Dunit = g/cm3
  Dvalue = 1.532
  Group = -> [Rb_element001]
  conduct = 2
  density = 1
  expand = 3
  formula = Rb
  name = G4_Rb
  specific = 4
FEATURE [App::DocumentObjectGroupPython] Sr_element001  label="Sr_element : 1"  # scripted group (container) (typed FeaturePython)
  n = 1
  ref = Sr_element
FEATURE [App::DocumentObjectGroupPython] G4_Sr  # scripted group (container) (typed FeaturePython)
  Dunit = g/cm3
  Dvalue = 2.54
  Group = -> [Sr_element001]
  conduct = 2
  density = 1
  expand = 3
  formula = Sr
  name = G4_Sr
  specific = 4
FEATURE [App::DocumentObjectGroupPython] Y_element001  label="Y_element : 1"  # scripted group (container) (typed FeaturePython)
  n = 1
  ref = Y_element
FEATURE [App::DocumentObjectGroupPython] G4_Y  # scripted group (container) (typed FeaturePython)
  Dunit = g/cm3
  Dvalue = 4.469
  Group = -> [Y_element001]
  conduct = 2
  density = 1
  expand = 3
  formula = Y
  name = G4_Y
  specific = 4
FEATURE [App::DocumentObjectGroupPython] Zr_element001  label="Zr_element : 1"  # scripted group (container) (typed FeaturePython)
  n = 1
  ref = Zr_element
FEATURE [App::DocumentObjectGroupPython] G4_Zr  # scripted group (container) (typed FeaturePython)
  Dunit = g/cm3
  Dvalue = 6.506
  Group = -> [Zr_element001]
  conduct = 2
  density = 1
  expand = 3
  formula = Zr
  name = G4_Zr
  specific = 4
FEATURE [App::DocumentObjectGroupPython] Nb_element001  label="Nb_element : 1"  # scripted group (container) (typed FeaturePython)
  n = 1
  ref = Nb_element
FEATURE [App::DocumentObjectGroupPython] G4_Nb  # scripted group (container) (typed FeaturePython)
  Dunit = g/cm3
  Dvalue = 8.57
  Group = -> [Nb_element001]
  conduct = 2
  density = 1
  expand = 3
  formula = Nb
  name = G4_Nb
  specific = 4
FEATURE [App::DocumentObjectGroupPython] Mo_element001  label="Mo_element : 1"  # scripted group (container) (typed FeaturePython)
  n = 1
  ref = Mo_element
FEATURE [App::DocumentObjectGroupPython] G4_Mo  # scripted group (container) (typed FeaturePython)
  Dunit = g/cm3
  Dvalue = 10.22
  Group = -> [Mo_element001]
  conduct = 2
  density = 1
  expand = 3
  formula = Mo
  name = G4_Mo
  specific = 4
FEATURE [App::DocumentObjectGroupPython] Tc_element001  label="Tc_element : 1"  # scripted group (container) (typed FeaturePython)
  n = 1
  ref = Tc_element
FEATURE [App::DocumentObjectGroupPython] G4_Tc  # scripted group (container) (typed FeaturePython)
  Dunit = g/cm3
  Dvalue = 11.5
  Group = -> [Tc_element001]
  conduct = 2
  density = 1
  expand = 3
  formula = Tc
  name = G4_Tc
  specific = 4
FEATURE [App::DocumentObjectGroupPython] Ru_element001  label="Ru_element : 1"  # scripted group (container) (typed FeaturePython)
  n = 1
  ref = Ru_element
FEATURE [App::DocumentObjectGroupPython] G4_Ru  # scripted group (container) (typed FeaturePython)
  Dunit = g/cm3
  Dvalue = 12.41
  Group = -> [Ru_element001]
  conduct = 2
  density = 1
  expand = 3
  formula = Ru
  name = G4_Ru
  specific = 4
FEATURE [App::DocumentObjectGroupPython] Rh_element001  label="Rh_element : 1"  # scripted group (container) (typed FeaturePython)
  n = 1
  ref = Rh_element
FEATURE [App::DocumentObjectGroupPython] G4_Rh  # scripted group (container) (typed FeaturePython)
  Dunit = g/cm3
  Dvalue = 12.41
  Group = -> [Rh_element001]
  conduct = 2
  density = 1
  expand = 3
  formula = Rh
  name = G4_Rh
  specific = 4
FEATURE [App::DocumentObjectGroupPython] Pd_element001  label="Pd_element : 1"  # scripted group (container) (typed FeaturePython)
  n = 1
  ref = Pd_element
FEATURE [App::DocumentObjectGroupPython] G4_Pd  # scripted group (container) (typed FeaturePython)
  Dunit = g/cm3
  Dvalue = 12.02
  Group = -> [Pd_element001]
  conduct = 2
  density = 1
  expand = 3
  formula = Pd
  name = G4_Pd
  specific = 4
FEATURE [App::DocumentObjectGroupPython] Ag_element006  label="Ag_element : 004"  # scripted group (container) (typed FeaturePython)
  n = 1
  ref = Ag_element
FEATURE [App::DocumentObjectGroupPython] G4_Ag  # scripted group (container) (typed FeaturePython)
  Dunit = g/cm3
  Dvalue = 10.5
  Group = -> [Ag_element006]
  conduct = 2
  density = 1
  expand = 3
  formula = Ag
  name = G4_Ag
  specific = 4
FEATURE [App::DocumentObjectGroupPython] Cd_element003  label="Cd_element : 003"  # scripted group (container) (typed FeaturePython)
  n = 1
  ref = Cd_element
FEATURE [App::DocumentObjectGroupPython] G4_Cd  # scripted group (container) (typed FeaturePython)
  Dunit = g/cm3
  Dvalue = 8.65
  Group = -> [Cd_element003]
  conduct = 2
  density = 1
  expand = 3
  formula = Cd
  name = G4_Cd
  specific = 4
FEATURE [App::DocumentObjectGroupPython] In_element001  label="In_element : 1"  # scripted group (container) (typed FeaturePython)
  n = 1
  ref = In_element
FEATURE [App::DocumentObjectGroupPython] G4_In  # scripted group (container) (typed FeaturePython)
  Dunit = g/cm3
  Dvalue = 7.31
  Group = -> [In_element001]
  conduct = 2
  density = 1
  expand = 3
  formula = In
  name = G4_In
  specific = 4
FEATURE [App::DocumentObjectGroupPython] Sn_element001  label="Sn_element : 1"  # scripted group (container) (typed FeaturePython)
  n = 1
  ref = Sn_element
FEATURE [App::DocumentObjectGroupPython] G4_Sn  # scripted group (container) (typed FeaturePython)
  Dunit = g/cm3
  Dvalue = 7.31
  Group = -> [Sn_element001]
  conduct = 2
  density = 1
  expand = 3
  formula = Sn
  name = G4_Sn
  specific = 4
FEATURE [App::DocumentObjectGroupPython] Sb_element001  label="Sb_element : 1"  # scripted group (container) (typed FeaturePython)
  n = 1
  ref = Sb_element
FEATURE [App::DocumentObjectGroupPython] G4_Sb  # scripted group (container) (typed FeaturePython)
  Dunit = g/cm3
  Dvalue = 6.691
  Group = -> [Sb_element001]
  conduct = 2
  density = 1
  expand = 3
  formula = Sb
  name = G4_Sb
  specific = 4
FEATURE [App::DocumentObjectGroupPython] Te_element002  label="Te_element : 002"  # scripted group (container) (typed FeaturePython)
  n = 1
  ref = Te_element
FEATURE [App::DocumentObjectGroupPython] G4_Te  # scripted group (container) (typed FeaturePython)
  Dunit = g/cm3
  Dvalue = 6.24
  Group = -> [Te_element002]
  conduct = 2
  density = 1
  expand = 3
  formula = Te
  name = G4_Te
  specific = 4
FEATURE [App::DocumentObjectGroupPython] I_element010  label="I_element : 006"  # scripted group (container) (typed FeaturePython)
  n = 1
  ref = I_element
FEATURE [App::DocumentObjectGroupPython] G4_I  # scripted group (container) (typed FeaturePython)
  Dunit = g/cm3
  Dvalue = 4.93
  Group = -> [I_element010]
  conduct = 2
  density = 1
  expand = 3
  formula = I
  name = G4_I
  specific = 4
FEATURE [App::DocumentObjectGroupPython] Xe_element001  label="Xe_element : 1"  # scripted group (container) (typed FeaturePython)
  n = 1
  ref = Xe_element
FEATURE [App::DocumentObjectGroupPython] G4_Xe  # scripted group (container) (typed FeaturePython)
  Dunit = g/cm3
  Dvalue = 0.00548536
  Group = -> [Xe_element001]
  conduct = 2
  density = 1
  expand = 3
  formula = Xe
  name = G4_Xe
  specific = 4
FEATURE [App::DocumentObjectGroupPython] Cs_element003  label="Cs_element : 003"  # scripted group (container) (typed FeaturePython)
  n = 1
  ref = Cs_element
FEATURE [App::DocumentObjectGroupPython] G4_Cs  # scripted group (container) (typed FeaturePython)
  Dunit = g/cm3
  Dvalue = 1.873
  Group = -> [Cs_element003]
  conduct = 2
  density = 1
  expand = 3
  formula = Cs
  name = G4_Cs
  specific = 4
FEATURE [App::DocumentObjectGroupPython] Ba_element003  label="Ba_element : 003"  # scripted group (container) (typed FeaturePython)
  n = 1
  ref = Ba_element
FEATURE [App::DocumentObjectGroupPython] G4_Ba  # scripted group (container) (typed FeaturePython)
  Dunit = g/cm3
  Dvalue = 3.5
  Group = -> [Ba_element003]
  conduct = 2
  density = 1
  expand = 3
  formula = Ba
  name = G4_Ba
  specific = 4
FEATURE [App::DocumentObjectGroupPython] La_element003  label="La_element : 003"  # scripted group (container) (typed FeaturePython)
  n = 1
  ref = La_element
FEATURE [App::DocumentObjectGroupPython] G4_La  # scripted group (container) (typed FeaturePython)
  Dunit = g/cm3
  Dvalue = 6.154
  Group = -> [La_element003]
  conduct = 2
  density = 1
  expand = 3
  formula = La
  name = G4_La
  specific = 4
FEATURE [App::DocumentObjectGroupPython] Ce_element002  label="Ce_element : 1"  # scripted group (container) (typed FeaturePython)
  n = 1
  ref = Ce_element
FEATURE [App::DocumentObjectGroupPython] G4_Ce  # scripted group (container) (typed FeaturePython)
  Dunit = g/cm3
  Dvalue = 6.657
  Group = -> [Ce_element002]
  conduct = 2
  density = 1
  expand = 3
  formula = Ce
  name = G4_Ce
  specific = 4
FEATURE [App::DocumentObjectGroupPython] Pr_element001  label="Pr_element : 1"  # scripted group (container) (typed FeaturePython)
  n = 1
  ref = Pr_element
FEATURE [App::DocumentObjectGroupPython] G4_Pr  # scripted group (container) (typed FeaturePython)
  Dunit = g/cm3
  Dvalue = 6.71
  Group = -> [Pr_element001]
  conduct = 2
  density = 1
  expand = 3
  formula = Pr
  name = G4_Pr
  specific = 4
FEATURE [App::DocumentObjectGroupPython] Nd_element001  label="Nd_element : 1"  # scripted group (container) (typed FeaturePython)
  n = 1
  ref = Nd_element
FEATURE [App::DocumentObjectGroupPython] G4_Nd  # scripted group (container) (typed FeaturePython)
  Dunit = g/cm3
  Dvalue = 6.9
  Group = -> [Nd_element001]
  conduct = 2
  density = 1
  expand = 3
  formula = Nd
  name = G4_Nd
  specific = 4
FEATURE [App::DocumentObjectGroupPython] Pm_element001  label="Pm_element : 1"  # scripted group (container) (typed FeaturePython)
  n = 1
  ref = Pm_element
FEATURE [App::DocumentObjectGroupPython] G4_Pm  # scripted group (container) (typed FeaturePython)
  Dunit = g/cm3
  Dvalue = 7.22
  Group = -> [Pm_element001]
  conduct = 2
  density = 1
  expand = 3
  formula = Pm
  name = G4_Pm
  specific = 4
FEATURE [App::DocumentObjectGroupPython] Sm_element001  label="Sm_element : 1"  # scripted group (container) (typed FeaturePython)
  n = 1
  ref = Sm_element
FEATURE [App::DocumentObjectGroupPython] G4_Sm  # scripted group (container) (typed FeaturePython)
  Dunit = g/cm3
  Dvalue = 7.46
  Group = -> [Sm_element001]
  conduct = 2
  density = 1
  expand = 3
  formula = Sm
  name = G4_Sm
  specific = 4
FEATURE [App::DocumentObjectGroupPython] Eu_element001  label="Eu_element : 1"  # scripted group (container) (typed FeaturePython)
  n = 1
  ref = Eu_element
FEATURE [App::DocumentObjectGroupPython] G4_Eu  # scripted group (container) (typed FeaturePython)
  Dunit = g/cm3
  Dvalue = 5.243
  Group = -> [Eu_element001]
  conduct = 2
  density = 1
  expand = 3
  formula = Eu
  name = G4_Eu
  specific = 4
FEATURE [App::DocumentObjectGroupPython] Gd_element002  label="Gd_element : 1"  # scripted group (container) (typed FeaturePython)
  n = 1
  ref = Gd_element
FEATURE [App::DocumentObjectGroupPython] G4_Gd  # scripted group (container) (typed FeaturePython)
  Dunit = g/cm3
  Dvalue = 7.9004
  Group = -> [Gd_element002]
  conduct = 2
  density = 1
  expand = 3
  formula = Gd
  name = G4_Gd
  specific = 4
FEATURE [App::DocumentObjectGroupPython] Tb_element001  label="Tb_element : 1"  # scripted group (container) (typed FeaturePython)
  n = 1
  ref = Tb_element
FEATURE [App::DocumentObjectGroupPython] G4_Tb  # scripted group (container) (typed FeaturePython)
  Dunit = g/cm3
  Dvalue = 8.229
  Group = -> [Tb_element001]
  conduct = 2
  density = 1
  expand = 3
  formula = Tb
  name = G4_Tb
  specific = 4
FEATURE [App::DocumentObjectGroupPython] Dy_element001  label="Dy_element : 1"  # scripted group (container) (typed FeaturePython)
  n = 1
  ref = Dy_element
FEATURE [App::DocumentObjectGroupPython] G4_Dy  # scripted group (container) (typed FeaturePython)
  Dunit = g/cm3
  Dvalue = 8.55
  Group = -> [Dy_element001]
  conduct = 2
  density = 1
  expand = 3
  formula = Dy
  name = G4_Dy
  specific = 4
FEATURE [App::DocumentObjectGroupPython] Ho_element001  label="Ho_element : 1"  # scripted group (container) (typed FeaturePython)
  n = 1
  ref = Ho_element
FEATURE [App::DocumentObjectGroupPython] G4_Ho  # scripted group (container) (typed FeaturePython)
  Dunit = g/cm3
  Dvalue = 8.795
  Group = -> [Ho_element001]
  conduct = 2
  density = 1
  expand = 3
  formula = Ho
  name = G4_Ho
  specific = 4
FEATURE [App::DocumentObjectGroupPython] Er_element001  label="Er_element : 1"  # scripted group (container) (typed FeaturePython)
  n = 1
  ref = Er_element
FEATURE [App::DocumentObjectGroupPython] G4_Er  # scripted group (container) (typed FeaturePython)
  Dunit = g/cm3
  Dvalue = 9.066
  Group = -> [Er_element001]
  conduct = 2
  density = 1
  expand = 3
  formula = Er
  name = G4_Er
  specific = 4
FEATURE [App::DocumentObjectGroupPython] Tm_element001  label="Tm_element : 1"  # scripted group (container) (typed FeaturePython)
  n = 1
  ref = Tm_element
FEATURE [App::DocumentObjectGroupPython] G4_Tm  # scripted group (container) (typed FeaturePython)
  Dunit = g/cm3
  Dvalue = 9.321
  Group = -> [Tm_element001]
  conduct = 2
  density = 1
  expand = 3
  formula = Tm
  name = G4_Tm
  specific = 4
FEATURE [App::DocumentObjectGroupPython] Yb_element001  label="Yb_element : 1"  # scripted group (container) (typed FeaturePython)
  n = 1
  ref = Yb_element
FEATURE [App::DocumentObjectGroupPython] G4_Yb  # scripted group (container) (typed FeaturePython)
  Dunit = g/cm3
  Dvalue = 6.73
  Group = -> [Yb_element001]
  conduct = 2
  density = 1
  expand = 3
  formula = Yb
  name = G4_Yb
  specific = 4
FEATURE [App::DocumentObjectGroupPython] Lu_element001  label="Lu_element : 1"  # scripted group (container) (typed FeaturePython)
  n = 1
  ref = Lu_element
FEATURE [App::DocumentObjectGroupPython] G4_Lu  # scripted group (container) (typed FeaturePython)
  Dunit = g/cm3
  Dvalue = 9.84
  Group = -> [Lu_element001]
  conduct = 2
  density = 1
  expand = 3
  formula = Lu
  name = G4_Lu
  specific = 4
FEATURE [App::DocumentObjectGroupPython] Hf_element001  label="Hf_element : 1"  # scripted group (container) (typed FeaturePython)
  n = 1
  ref = Hf_element
FEATURE [App::DocumentObjectGroupPython] G4_Hf  # scripted group (container) (typed FeaturePython)
  Dunit = g/cm3
  Dvalue = 13.31
  Group = -> [Hf_element001]
  conduct = 2
  density = 1
  expand = 3
  formula = Hf
  name = G4_Hf
  specific = 4
FEATURE [App::DocumentObjectGroupPython] Ta_element001  label="Ta_element : 1"  # scripted group (container) (typed FeaturePython)
  n = 1
  ref = Ta_element
FEATURE [App::DocumentObjectGroupPython] G4_Ta  # scripted group (container) (typed FeaturePython)
  Dunit = g/cm3
  Dvalue = 16.654
  Group = -> [Ta_element001]
  conduct = 2
  density = 1
  expand = 3
  formula = Ta
  name = G4_Ta
  specific = 4
FEATURE [App::DocumentObjectGroupPython] W_element004  label="W_element : 004"  # scripted group (container) (typed FeaturePython)
  n = 1
  ref = W_element
FEATURE [App::DocumentObjectGroupPython] G4_W  # scripted group (container) (typed FeaturePython)
  Dunit = g/cm3
  Dvalue = 19.3
  Group = -> [W_element004]
  conduct = 2
  density = 1
  expand = 3
  formula = W
  name = G4_W
  specific = 4
FEATURE [App::DocumentObjectGroupPython] Re_element001  label="Re_element : 1"  # scripted group (container) (typed FeaturePython)
  n = 1
  ref = Re_element
FEATURE [App::DocumentObjectGroupPython] G4_Re  # scripted group (container) (typed FeaturePython)
  Dunit = g/cm3
  Dvalue = 21.02
  Group = -> [Re_element001]
  conduct = 2
  density = 1
  expand = 3
  formula = Re
  name = G4_Re
  specific = 4
FEATURE [App::DocumentObjectGroupPython] Os_element001  label="Os_element : 1"  # scripted group (container) (typed FeaturePython)
  n = 1
  ref = Os_element
FEATURE [App::DocumentObjectGroupPython] G4_Os  # scripted group (container) (typed FeaturePython)
  Dunit = g/cm3
  Dvalue = 22.57
  Group = -> [Os_element001]
  conduct = 2
  density = 1
  expand = 3
  formula = Os
  name = G4_Os
  specific = 4
FEATURE [App::DocumentObjectGroupPython] Ir_element001  label="Ir_element : 1"  # scripted group (container) (typed FeaturePython)
  n = 1
  ref = Ir_element
FEATURE [App::DocumentObjectGroupPython] G4_Ir  # scripted group (container) (typed FeaturePython)
  Dunit = g/cm3
  Dvalue = 22.42
  Group = -> [Ir_element001]
  conduct = 2
  density = 1
  expand = 3
  formula = Ir
  name = G4_Ir
  specific = 4
FEATURE [App::DocumentObjectGroupPython] Pt_element001  label="Pt_element : 1"  # scripted group (container) (typed FeaturePython)
  n = 1
  ref = Pt_element
FEATURE [App::DocumentObjectGroupPython] G4_Pt  # scripted group (container) (typed FeaturePython)
  Dunit = g/cm3
  Dvalue = 21.45
  Group = -> [Pt_element001]
  conduct = 2
  density = 1
  expand = 3
  formula = Pt
  name = G4_Pt
  specific = 4
FEATURE [App::DocumentObjectGroupPython] Au_element001  label="Au_element : 1"  # scripted group (container) (typed FeaturePython)
  n = 1
  ref = Au_element
FEATURE [App::DocumentObjectGroupPython] G4_Au  # scripted group (container) (typed FeaturePython)
  Dunit = g/cm3
  Dvalue = 19.32
  Group = -> [Au_element001]
  conduct = 2
  density = 1
  expand = 3
  formula = Au
  name = G4_Au
  specific = 4
FEATURE [App::DocumentObjectGroupPython] Hg_element002  label="Hg_element : 002"  # scripted group (container) (typed FeaturePython)
  n = 1
  ref = Hg_element
FEATURE [App::DocumentObjectGroupPython] G4_Hg  # scripted group (container) (typed FeaturePython)
  Dunit = g/cm3
  Dvalue = 13.546
  Group = -> [Hg_element002]
  conduct = 2
  density = 1
  expand = 3
  formula = Hg
  name = G4_Hg
  specific = 4
FEATURE [App::DocumentObjectGroupPython] Tl_element002  label="Tl_element : 002"  # scripted group (container) (typed FeaturePython)
  n = 1
  ref = Tl_element
FEATURE [App::DocumentObjectGroupPython] G4_Tl  # scripted group (container) (typed FeaturePython)
  Dunit = g/cm3
  Dvalue = 11.72
  Group = -> [Tl_element002]
  conduct = 2
  density = 1
  expand = 3
  formula = Tl
  name = G4_Tl
  specific = 4
FEATURE [App::DocumentObjectGroupPython] Pb_element003  label="Pb_element : 1"  # scripted group (container) (typed FeaturePython)
  n = 1
  ref = Pb_element
FEATURE [App::DocumentObjectGroupPython] G4_Pb  # scripted group (container) (typed FeaturePython)
  Dunit = g/cm3
  Dvalue = 11.35
  Group = -> [Pb_element003]
  conduct = 2
  density = 1
  expand = 3
  formula = Pb
  name = G4_Pb
  specific = 4
FEATURE [App::DocumentObjectGroupPython] Bi_element002  label="Bi_element : 1"  # scripted group (container) (typed FeaturePython)
  n = 1
  ref = Bi_element
FEATURE [App::DocumentObjectGroupPython] G4_Bi  # scripted group (container) (typed FeaturePython)
  Dunit = g/cm3
  Dvalue = 9.747
  Group = -> [Bi_element002]
  conduct = 2
  density = 1
  expand = 3
  formula = Bi
  name = G4_Bi
  specific = 4
FEATURE [App::DocumentObjectGroupPython] Po_element001  label="Po_element : 1"  # scripted group (container) (typed FeaturePython)
  n = 1
  ref = Po_element
FEATURE [App::DocumentObjectGroupPython] G4_Po  # scripted group (container) (typed FeaturePython)
  Dunit = g/cm3
  Dvalue = 9.32
  Group = -> [Po_element001]
  conduct = 2
  density = 1
  expand = 3
  formula = Po
  name = G4_Po
  specific = 4
FEATURE [App::DocumentObjectGroupPython] At_element001  label="At_element : 1"  # scripted group (container) (typed FeaturePython)
  n = 1
  ref = At_element
FEATURE [App::DocumentObjectGroupPython] G4_At  # scripted group (container) (typed FeaturePython)
  Dunit = g/cm3
  Dvalue = 9.32
  Group = -> [At_element001]
  conduct = 2
  density = 1
  expand = 3
  formula = At
  name = G4_At
  specific = 4
FEATURE [App::DocumentObjectGroupPython] Rn_element001  label="Rn_element : 1"  # scripted group (container) (typed FeaturePython)
  n = 1
  ref = Rn_element
FEATURE [App::DocumentObjectGroupPython] G4_Rn  # scripted group (container) (typed FeaturePython)
  Dunit = g/cm3
  Dvalue = 0.00900662
  Group = -> [Rn_element001]
  conduct = 2
  density = 1
  expand = 3
  formula = Rn
  name = G4_Rn
  specific = 4
FEATURE [App::DocumentObjectGroupPython] Fr_element001  label="Fr_element : 1"  # scripted group (container) (typed FeaturePython)
  n = 1
  ref = Fr_element
FEATURE [App::DocumentObjectGroupPython] G4_Fr  # scripted group (container) (typed FeaturePython)
  Dunit = g/cm3
  Dvalue = 1
  Group = -> [Fr_element001]
  conduct = 2
  density = 1
  expand = 3
  formula = Fr
  name = G4_Fr
  specific = 4
FEATURE [App::DocumentObjectGroupPython] Ra_element001  label="Ra_element : 1"  # scripted group (container) (typed FeaturePython)
  n = 1
  ref = Ra_element
FEATURE [App::DocumentObjectGroupPython] G4_Ra  # scripted group (container) (typed FeaturePython)
  Dunit = g/cm3
  Dvalue = 5
  Group = -> [Ra_element001]
  conduct = 2
  density = 1
  expand = 3
  formula = Ra
  name = G4_Ra
  specific = 4
FEATURE [App::DocumentObjectGroupPython] Ac_element001  label="Ac_element : 1"  # scripted group (container) (typed FeaturePython)
  n = 1
  ref = Ac_element
FEATURE [App::DocumentObjectGroupPython] G4_Ac  # scripted group (container) (typed FeaturePython)
  Dunit = g/cm3
  Dvalue = 10.07
  Group = -> [Ac_element001]
  conduct = 2
  density = 1
  expand = 3
  formula = Ac
  name = G4_Ac
  specific = 4
FEATURE [App::DocumentObjectGroupPython] Th_element001  label="Th_element : 1"  # scripted group (container) (typed FeaturePython)
  n = 1
  ref = Th_element
FEATURE [App::DocumentObjectGroupPython] G4_Th  # scripted group (container) (typed FeaturePython)
  Dunit = g/cm3
  Dvalue = 11.72
  Group = -> [Th_element001]
  conduct = 2
  density = 1
  expand = 3
  formula = Th
  name = G4_Th
  specific = 4
FEATURE [App::DocumentObjectGroupPython] Pa_element001  label="Pa_element : 1"  # scripted group (container) (typed FeaturePython)
  n = 1
  ref = Pa_element
FEATURE [App::DocumentObjectGroupPython] G4_Pa  # scripted group (container) (typed FeaturePython)
  Dunit = g/cm3
  Dvalue = 15.37
  Group = -> [Pa_element001]
  conduct = 2
  density = 1
  expand = 3
  formula = Pa
  name = G4_Pa
  specific = 4
FEATURE [App::DocumentObjectGroupPython] U_element004  label="U_element : 004"  # scripted group (container) (typed FeaturePython)
  n = 1
  ref = U_element
FEATURE [App::DocumentObjectGroupPython] G4_U  # scripted group (container) (typed FeaturePython)
  Dunit = g/cm3
  Dvalue = 18.95
  Group = -> [U_element004]
  conduct = 2
  density = 1
  expand = 3
  formula = U
  name = G4_U
  specific = 4
FEATURE [App::DocumentObjectGroupPython] Np_element001  label="Np_element : 1"  # scripted group (container) (typed FeaturePython)
  n = 1
  ref = Np_element
FEATURE [App::DocumentObjectGroupPython] G4_Np  # scripted group (container) (typed FeaturePython)
  Dunit = g/cm3
  Dvalue = 20.25
  Group = -> [Np_element001]
  conduct = 2
  density = 1
  expand = 3
  formula = Np
  name = G4_Np
  specific = 4
FEATURE [App::DocumentObjectGroupPython] Pu_element002  label="Pu_element : 002"  # scripted group (container) (typed FeaturePython)
  n = 1
  ref = Pu_element
FEATURE [App::DocumentObjectGroupPython] G4_Pu  # scripted group (container) (typed FeaturePython)
  Dunit = g/cm3
  Dvalue = 19.84
  Group = -> [Pu_element002]
  conduct = 2
  density = 1
  expand = 3
  formula = Pu
  name = G4_Pu
  specific = 4
FEATURE [App::DocumentObjectGroupPython] Am_element001  label="Am_element : 1"  # scripted group (container) (typed FeaturePython)
  n = 1
  ref = Am_element
FEATURE [App::DocumentObjectGroupPython] G4_Am  # scripted group (container) (typed FeaturePython)
  Dunit = g/cm3
  Dvalue = 13.67
  Group = -> [Am_element001]
  conduct = 2
  density = 1
  expand = 3
  formula = Am
  name = G4_Am
  specific = 4
FEATURE [App::DocumentObjectGroupPython] Cm_element001  label="Cm_element : 1"  # scripted group (container) (typed FeaturePython)
  n = 1
  ref = Cm_element
FEATURE [App::DocumentObjectGroupPython] G4_Cm  # scripted group (container) (typed FeaturePython)
  Dunit = g/cm3
  Dvalue = 13.51
  Group = -> [Cm_element001]
  conduct = 2
  density = 1
  expand = 3
  formula = Cm
  name = G4_Cm
  specific = 4
FEATURE [App::DocumentObjectGroupPython] Bk_element001  label="Bk_element : 1"  # scripted group (container) (typed FeaturePython)
  n = 1
  ref = Bk_element
FEATURE [App::DocumentObjectGroupPython] G4_Bk  # scripted group (container) (typed FeaturePython)
  Dunit = g/cm3
  Dvalue = 14
  Group = -> [Bk_element001]
  conduct = 2
  density = 1
  expand = 3
  formula = Bk
  name = G4_Bk
  specific = 4
FEATURE [App::DocumentObjectGroupPython] Cf_element001  label="Cf_element : 1"  # scripted group (container) (typed FeaturePython)
  n = 1
  ref = Cf_element
FEATURE [App::DocumentObjectGroupPython] G4_Cf  # scripted group (container) (typed FeaturePython)
  Dunit = g/cm3
  Dvalue = 10
  Group = -> [Cf_element001]
  conduct = 2
  density = 1
  expand = 3
  formula = Cf
  name = G4_Cf
  specific = 4
FEATURE [App::DocumentObjectGroupPython] Element  # scripted group (container) (typed FeaturePython)
  Group = -> [G4_H,G4_He,G4_Li,G4_Be,G4_B,G4_C,G4_N,G4_O,G4_F,G4_Ne,G4_Na,G4_Mg,G4_Al,G4_Si,G4_P,G4_S,G4_Cl,G4_Ar,G4_K,G4_Ca,G4_Sc,G4_Ti,G4_V,G4_Cr,G4_Mn,G4_Fe,G4_Co,G4_Ni,G4_Cu,G4_Zn,G4_Ga,G4_Ge,G4_As,G4_Se,G4_Br,G4_Kr,G4_Rb,G4_Sr,G4_Y,G4_Zr,G4_Nb,G4_Mo,G4_Tc,G4_Ru,G4_Rh,G4_Pd,G4_Ag,G4_Cd,G4_In,G4_Sn,G4_Sb,G4_Te,G4_I,G4_Xe,G4_Cs,G4_Ba,G4_La,G4_Ce,G4_Pr,G4_Nd,G4_Pm,G4_Sm,G4_Eu,G4_Gd,G4_Tb,G4_Dy,G4_Ho,G4_Er,+30 more]
FEATURE [App::DocumentObjectGroupPython] H_element114  label="H_element : 063"  # scripted group (container) (typed FeaturePython)
  n = 2
  ref = H_element
FEATURE [App::DocumentObjectGroupPython] G4_lH2  # scripted group (container) (typed FeaturePython)
  Dunit = g/cm3
  Dvalue = 0.0708
  Group = -> [H_element114]
  conduct = 2
  density = 1
  expand = 3
  formula = G4_lH2
  name = G4_lH2
  specific = 4
FEATURE [App::DocumentObjectGroupPython] N_element049  label="N_element : 022"  # scripted group (container) (typed FeaturePython)
  n = 2
  ref = N_element
FEATURE [App::DocumentObjectGroupPython] G4_lN2  # scripted group (container) (typed FeaturePython)
  Dunit = g/cm3
  Dvalue = 0.807
  Group = -> [N_element049]
  conduct = 2
  density = 1
  expand = 3
  formula = G4_lN2
  name = G4_lN2
  specific = 4
FEATURE [App::DocumentObjectGroupPython] O_element106  label="O_element : 060"  # scripted group (container) (typed FeaturePython)
  n = 2
  ref = O_element
FEATURE [App::DocumentObjectGroupPython] G4_lO2  # scripted group (container) (typed FeaturePython)
  Dunit = g/cm3
  Dvalue = 1.141
  Group = -> [O_element106]
  conduct = 2
  density = 1
  expand = 3
  formula = G4_lO2
  name = G4_lO2
  specific = 4
FEATURE [App::DocumentObjectGroupPython] Ar_element003  label="Ar_element : 002"  # scripted group (container) (typed FeaturePython)
  n = 1
  ref = Ar_element
FEATURE [App::DocumentObjectGroupPython] G4_lAr  # scripted group (container) (typed FeaturePython)
  Dunit = g/cm3
  Dvalue = 1.396
  Group = -> [Ar_element003]
  conduct = 2
  density = 1
  expand = 3
  formula = G4_lAr
  name = G4_lAr
  specific = 4
FEATURE [App::DocumentObjectGroupPython] Br_element008  label="Br_element : 005"  # scripted group (container) (typed FeaturePython)
  n = 1
  ref = Br_element
FEATURE [App::DocumentObjectGroupPython] G4_lBr  # scripted group (container) (typed FeaturePython)
  Dunit = g/cm3
  Dvalue = 3.1028
  Group = -> [Br_element008]
  conduct = 2
  density = 1
  expand = 3
  formula = G4_lBr
  name = G4_lBr
  specific = 4
FEATURE [App::DocumentObjectGroupPython] Kr_element002  label="Kr_element : 002"  # scripted group (container) (typed FeaturePython)
  n = 1
  ref = Kr_element
FEATURE [App::DocumentObjectGroupPython] G4_lKr  # scripted group (container) (typed FeaturePython)
  Dunit = g/cm3
  Dvalue = 2.418
  Group = -> [Kr_element002]
  conduct = 2
  density = 1
  expand = 3
  formula = G4_lKr
  name = G4_lKr
  specific = 4
FEATURE [App::DocumentObjectGroupPython] Xe_element002  label="Xe_element : 002"  # scripted group (container) (typed FeaturePython)
  n = 1
  ref = Xe_element
FEATURE [App::DocumentObjectGroupPython] G4_lXe  # scripted group (container) (typed FeaturePython)
  Dunit = g/cm3
  Dvalue = 2.953
  Group = -> [Xe_element002]
  conduct = 2
  density = 1
  expand = 3
  formula = G4_lXe
  name = G4_lXe
  specific = 4
FEATURE [App::DocumentObjectGroupPython] O_element107  label="O_element : 061"  # scripted group (container) (typed FeaturePython)
  n = 4
  ref = O_element
FEATURE [App::DocumentObjectGroupPython] Pb_element004  label="Pb_element : 002"  # scripted group (container) (typed FeaturePython)
  n = 1
  ref = Pb_element
FEATURE [App::DocumentObjectGroupPython] W_element005  label="W_element : 005"  # scripted group (container) (typed FeaturePython)
  n = 1
  ref = W_element
FEATURE [App::DocumentObjectGroupPython] G4_PbWO4  # scripted group (container) (typed FeaturePython)
  Dunit = g/cm3
  Dvalue = 8.28
  Group = -> [O_element107,Pb_element004,W_element005]
  conduct = 2
  density = 1
  expand = 3
  formula = G4_PbWO4
  name = G4_PbWO4
  specific = 4
FEATURE [App::DocumentObjectGroupPython] H_element115  label="H_element : 064"  # scripted group (container) (typed FeaturePython)
  n = 1
  ref = H_element
FEATURE [App::DocumentObjectGroupPython] G4_Galactic  # scripted group (container) (typed FeaturePython)
  Dunit = g/cm3
  Dvalue = 0
  Group = -> [H_element115]
  conduct = 2
  density = 1
  expand = 3
  formula = G4_Galactic
  name = G4_Galactic
  specific = 4
FEATURE [App::DocumentObjectGroupPython] C_element125  label="C_element : 071"  # scripted group (container) (typed FeaturePython)
  n = 1
  ref = C_element
FEATURE [App::DocumentObjectGroupPython] G4_GRAPHITE_POROUS  # scripted group (container) (typed FeaturePython)
  Dunit = g/cm3
  Dvalue = 1.7
  Group = -> [C_element125]
  conduct = 2
  density = 1
  expand = 3
  formula = G4_GRAPHITE_POROUS
  name = G4_GRAPHITE_POROUS
  specific = 4
FEATURE [App::DocumentObjectGroupPython] H_element116  label="H_element : 0.150"  # scripted group (container) (typed FeaturePython)
  n = 0.080538
FEATURE [App::DocumentObjectGroupPython] C_element126  label="C_element : 0.600"  # scripted group (container) (typed FeaturePython)
  n = 0.599848
FEATURE [App::DocumentObjectGroupPython] O_element108  label="O_element : 0.320"  # scripted group (container) (typed FeaturePython)
  n = 0.319614
FEATURE [App::DocumentObjectGroupPython] G4_LUCITE  # scripted group (container) (typed FeaturePython)
  Dunit = g/cm3
  Dvalue = 1.19
  Group = -> [H_element116,C_element126,O_element108]
  conduct = 2
  density = 1
  expand = 3
  formula = G4_LUCITE
  name = G4_LUCITE
  specific = 4
FEATURE [App::DocumentObjectGroupPython] Cu_element002  label="Cu_element : 62"  # scripted group (container) (typed FeaturePython)
  n = 62
  ref = Cu_element
FEATURE [App::DocumentObjectGroupPython] Zn_element002  label="Zn_element : 35"  # scripted group (container) (typed FeaturePython)
  n = 35
  ref = Zn_element
FEATURE [App::DocumentObjectGroupPython] Pb_element005  label="Pb_element : 3"  # scripted group (container) (typed FeaturePython)
  n = 3
  ref = Pb_element
FEATURE [App::DocumentObjectGroupPython] G4_BRASS  # scripted group (container) (typed FeaturePython)
  Dunit = g/cm3
  Dvalue = 8.52
  Group = -> [Cu_element002,Zn_element002,Pb_element005]
  conduct = 2
  density = 1
  expand = 3
  formula = G4_BRASS
  name = G4_BRASS
  specific = 4
FEATURE [App::DocumentObjectGroupPython] Cu_element003  label="Cu_element : 89"  # scripted group (container) (typed FeaturePython)
  n = 89
  ref = Cu_element
FEATURE [App::DocumentObjectGroupPython] Zn_element003  label="Zn_element : 9"  # scripted group (container) (typed FeaturePython)
  n = 9
  ref = Zn_element
FEATURE [App::DocumentObjectGroupPython] Pb_element006  label="Pb_element : 2"  # scripted group (container) (typed FeaturePython)
  n = 2
  ref = Pb_element
FEATURE [App::DocumentObjectGroupPython] G4_BRONZE  # scripted group (container) (typed FeaturePython)
  Dunit = g/cm3
  Dvalue = 8.82
  Group = -> [Cu_element003,Zn_element003,Pb_element006]
  conduct = 2
  density = 1
  expand = 3
  formula = G4_BRONZE
  name = G4_BRONZE
  specific = 4
FEATURE [App::DocumentObjectGroupPython] Fe_element008  label="Fe_element : 74"  # scripted group (container) (typed FeaturePython)
  n = 74
  ref = Fe_element
FEATURE [App::DocumentObjectGroupPython] Cr_element002  label="Cr_element : 18"  # scripted group (container) (typed FeaturePython)
  n = 18
  ref = Cr_element
FEATURE [App::DocumentObjectGroupPython] Ni_element002  label="Ni_element : 8"  # scripted group (container) (typed FeaturePython)
  n = 8
  ref = Ni_element
FEATURE [App::DocumentObjectGroupPython] G4_STAINLESS_STEEL  label="G4_STAINLESS-STEEL"  # scripted group (container) (typed FeaturePython)
  Dunit = g/cm3
  Dvalue = 8
  Group = -> [Fe_element008,Cr_element002,Ni_element002]
  conduct = 2
  density = 1
  expand = 3
  formula = G4_STAINLESS-STEEL
  name = G4_STAINLESS-STEEL
  specific = 4
FEATURE [App::DocumentObjectGroupPython] H_element117  label="H_element : 065"  # scripted group (container) (typed FeaturePython)
  n = 18
  ref = H_element
FEATURE [App::DocumentObjectGroupPython] C_element127  label="C_element : 072"  # scripted group (container) (typed FeaturePython)
  n = 12
  ref = C_element
FEATURE [App::DocumentObjectGroupPython] O_element109  label="O_element : 062"  # scripted group (container) (typed FeaturePython)
  n = 7
  ref = O_element
FEATURE [App::DocumentObjectGroupPython] G4_CR39  # scripted group (container) (typed FeaturePython)
  Dunit = g/cm3
  Dvalue = 1.32
  Group = -> [H_element117,C_element127,O_element109]
  conduct = 2
  density = 1
  expand = 3
  formula = G4_CR39
  name = G4_CR39
  specific = 4
FEATURE [App::DocumentObjectGroupPython] H_element118  label="H_element : 38"  # scripted group (container) (typed FeaturePython)
  n = 38
  ref = H_element
FEATURE [App::DocumentObjectGroupPython] C_element128  label="C_element : 073"  # scripted group (container) (typed FeaturePython)
  n = 18
  ref = C_element
FEATURE [App::DocumentObjectGroupPython] O_element110  label="O_element : 063"  # scripted group (container) (typed FeaturePython)
  n = 1
  ref = O_element
FEATURE [App::DocumentObjectGroupPython] G4_OCTADECANOL  # scripted group (container) (typed FeaturePython)
  Dunit = g/cm3
  Dvalue = 0.812
  Group = -> [H_element118,C_element128,O_element110]
  conduct = 2
  density = 1
  expand = 3
  formula = G4_OCTADECANOL
  name = G4_OCTADECANOL
  specific = 4
FEATURE [App::DocumentObjectGroupPython] HEP  # scripted group (container) (typed FeaturePython)
  Group = -> [G4_lH2,G4_lN2,G4_lO2,G4_lAr,G4_lBr,G4_lKr,G4_lXe,G4_PbWO4,G4_Galactic,G4_GRAPHITE_POROUS,G4_LUCITE,G4_BRASS,G4_BRONZE,G4_STAINLESS_STEEL,G4_CR39,G4_OCTADECANOL]
FEATURE [App::DocumentObjectGroupPython] C_element129  label="C_element : 074"  # scripted group (container) (typed FeaturePython)
  n = 14
  ref = C_element
FEATURE [App::DocumentObjectGroupPython] H_element119  label="H_element : 066"  # scripted group (container) (typed FeaturePython)
  n = 10
  ref = H_element
FEATURE [App::DocumentObjectGroupPython] O_element111  label="O_element : 064"  # scripted group (container) (typed FeaturePython)
  n = 2
  ref = O_element
FEATURE [App::DocumentObjectGroupPython] N_element050  label="N_element : 023"  # scripted group (container) (typed FeaturePython)
  n = 2
  ref = N_element
FEATURE [App::DocumentObjectGroupPython] G4_KEVLAR  # scripted group (container) (typed FeaturePython)
  Dunit = g/cm3
  Dvalue = 1.44
  Group = -> [C_element129,H_element119,O_element111,N_element050]
  conduct = 2
  density = 1
  expand = 3
  formula = G4_KEVLAR
  name = G4_KEVLAR
  specific = 4
FEATURE [App::DocumentObjectGroupPython] C_element130  label="C_element : 075"  # scripted group (container) (typed FeaturePython)
  n = 10
  ref = C_element
FEATURE [App::DocumentObjectGroupPython] H_element120  label="H_element : 067"  # scripted group (container) (typed FeaturePython)
  n = 8
  ref = H_element
FEATURE [App::DocumentObjectGroupPython] O_element112  label="O_element : 065"  # scripted group (container) (typed FeaturePython)
  n = 4
  ref = O_element
FEATURE [App::DocumentObjectGroupPython] G4_DACRON  # scripted group (container) (typed FeaturePython)
  Dunit = g/cm3
  Dvalue = 1.4
  Group = -> [C_element130,H_element120,O_element112]
  conduct = 2
  density = 1
  expand = 3
  formula = G4_DACRON
  name = G4_DACRON
  specific = 4
FEATURE [App::DocumentObjectGroupPython] C_element131  label="C_element : 076"  # scripted group (container) (typed FeaturePython)
  n = 4
  ref = C_element
FEATURE [App::DocumentObjectGroupPython] H_element121  label="H_element : 068"  # scripted group (container) (typed FeaturePython)
  n = 5
  ref = H_element
FEATURE [App::DocumentObjectGroupPython] Cl_element030  label="Cl_element : 016"  # scripted group (container) (typed FeaturePython)
  n = 1
  ref = Cl_element
FEATURE [App::DocumentObjectGroupPython] G4_NEOPRENE  # scripted group (container) (typed FeaturePython)
  Dunit = g/cm3
  Dvalue = 1.23
  Group = -> [C_element131,H_element121,Cl_element030]
  conduct = 2
  density = 1
  expand = 3
  formula = G4_NEOPRENE
  name = G4_NEOPRENE
  specific = 4
FEATURE [App::DocumentObjectGroupPython] Space  # scripted group (container) (typed FeaturePython)
  Group = -> [G4_KEVLAR,G4_DACRON,G4_NEOPRENE]
FEATURE [App::DocumentObjectGroupPython] H_element122  label="H_element : 069"  # scripted group (container) (typed FeaturePython)
  n = 5
  ref = H_element
FEATURE [App::DocumentObjectGroupPython] C_element132  label="C_element : 077"  # scripted group (container) (typed FeaturePython)
  n = 4
  ref = C_element
FEATURE [App::DocumentObjectGroupPython] N_element051  label="N_element : 3"  # scripted group (container) (typed FeaturePython)
  n = 3
  ref = N_element
FEATURE [App::DocumentObjectGroupPython] O_element113  label="O_element : 066"  # scripted group (container) (typed FeaturePython)
  n = 1
  ref = O_element
FEATURE [App::DocumentObjectGroupPython] G4_CYTOSINE  # scripted group (container) (typed FeaturePython)
  Dunit = g/cm3
  Dvalue = 1.55
  Group = -> [H_element122,C_element132,N_element051,O_element113]
  conduct = 2
  density = 1
  expand = 3
  formula = G4_CYTOSINE
  name = G4_CYTOSINE
  specific = 4
FEATURE [App::DocumentObjectGroupPython] H_element123  label="H_element : 070"  # scripted group (container) (typed FeaturePython)
  n = 6
  ref = H_element
FEATURE [App::DocumentObjectGroupPython] C_element133  label="C_element : 078"  # scripted group (container) (typed FeaturePython)
  n = 5
  ref = C_element
FEATURE [App::DocumentObjectGroupPython] N_element052  label="N_element : 024"  # scripted group (container) (typed FeaturePython)
  n = 2
  ref = N_element
FEATURE [App::DocumentObjectGroupPython] O_element114  label="O_element : 067"  # scripted group (container) (typed FeaturePython)
  n = 2
  ref = O_element
FEATURE [App::DocumentObjectGroupPython] G4_THYMINE  # scripted group (container) (typed FeaturePython)
  Dunit = g/cm3
  Dvalue = 1.23
  Group = -> [H_element123,C_element133,N_element052,O_element114]
  conduct = 2
  density = 1
  expand = 3
  formula = G4_THYMINE
  name = G4_THYMINE
  specific = 4
FEATURE [App::DocumentObjectGroupPython] H_element124  label="H_element : 071"  # scripted group (container) (typed FeaturePython)
  n = 4
  ref = H_element
FEATURE [App::DocumentObjectGroupPython] C_element134  label="C_element : 079"  # scripted group (container) (typed FeaturePython)
  n = 4
  ref = C_element
FEATURE [App::DocumentObjectGroupPython] N_element053  label="N_element : 025"  # scripted group (container) (typed FeaturePython)
  n = 2
  ref = N_element
FEATURE [App::DocumentObjectGroupPython] O_element115  label="O_element : 068"  # scripted group (container) (typed FeaturePython)
  n = 2
  ref = O_element
FEATURE [App::DocumentObjectGroupPython] G4_URACIL  # scripted group (container) (typed FeaturePython)
  Dunit = g/cm3
  Dvalue = 1.32
  Group = -> [H_element124,C_element134,N_element053,O_element115]
  conduct = 2
  density = 1
  expand = 3
  formula = G4_URACIL
  name = G4_URACIL
  specific = 4
FEATURE [App::DocumentObjectGroupPython] H_element125  label="H_element : 072"  # scripted group (container) (typed FeaturePython)
  n = 4
  ref = H_element
FEATURE [App::DocumentObjectGroupPython] C_element135  label="C_element : 080"  # scripted group (container) (typed FeaturePython)
  n = 5
  ref = C_element
FEATURE [App::DocumentObjectGroupPython] N_element054  label="N_element : 026"  # scripted group (container) (typed FeaturePython)
  n = 5
  ref = N_element
FEATURE [App::DocumentObjectGroupPython] G4_DNA_ADENINE  # scripted group (container) (typed FeaturePython)
  Dunit = g/cm3
  Dvalue = 1
  Group = -> [H_element125,C_element135,N_element054]
  conduct = 2
  density = 1
  expand = 3
  formula = G4_DNA_ADENINE
  name = G4_DNA_ADENINE
  specific = 4
FEATURE [App::DocumentObjectGroupPython] H_element126  label="H_element : 073"  # scripted group (container) (typed FeaturePython)
  n = 4
  ref = H_element
FEATURE [App::DocumentObjectGroupPython] C_element136  label="C_element : 081"  # scripted group (container) (typed FeaturePython)
  n = 5
  ref = C_element
FEATURE [App::DocumentObjectGroupPython] N_element055  label="N_element : 027"  # scripted group (container) (typed FeaturePython)
  n = 5
  ref = N_element
FEATURE [App::DocumentObjectGroupPython] O_element116  label="O_element : 069"  # scripted group (container) (typed FeaturePython)
  n = 1
  ref = O_element
FEATURE [App::DocumentObjectGroupPython] G4_DNA_GUANINE  # scripted group (container) (typed FeaturePython)
  Dunit = g/cm3
  Dvalue = 1
  Group = -> [H_element126,C_element136,N_element055,O_element116]
  conduct = 2
  density = 1
  expand = 3
  formula = G4_DNA_GUANINE
  name = G4_DNA_GUANINE
  specific = 4
FEATURE [App::DocumentObjectGroupPython] H_element127  label="H_element : 074"  # scripted group (container) (typed FeaturePython)
  n = 4
  ref = H_element
FEATURE [App::DocumentObjectGroupPython] C_element137  label="C_element : 082"  # scripted group (container) (typed FeaturePython)
  n = 4
  ref = C_element
FEATURE [App::DocumentObjectGroupPython] N_element056  label="N_element : 028"  # scripted group (container) (typed FeaturePython)
  n = 3
  ref = N_element
FEATURE [App::DocumentObjectGroupPython] O_element117  label="O_element : 070"  # scripted group (container) (typed FeaturePython)
  n = 1
  ref = O_element
FEATURE [App::DocumentObjectGroupPython] G4_DNA_CYTOSINE  # scripted group (container) (typed FeaturePython)
  Dunit = g/cm3
  Dvalue = 1
  Group = -> [H_element127,C_element137,N_element056,O_element117]
  conduct = 2
  density = 1
  expand = 3
  formula = G4_DNA_CYTOSINE
  name = G4_DNA_CYTOSINE
  specific = 4
FEATURE [App::DocumentObjectGroupPython] H_element128  label="H_element : 075"  # scripted group (container) (typed FeaturePython)
  n = 5
  ref = H_element
FEATURE [App::DocumentObjectGroupPython] C_element138  label="C_element : 083"  # scripted group (container) (typed FeaturePython)
  n = 5
  ref = C_element
FEATURE [App::DocumentObjectGroupPython] N_element057  label="N_element : 029"  # scripted group (container) (typed FeaturePython)
  n = 2
  ref = N_element
FEATURE [App::DocumentObjectGroupPython] O_element118  label="O_element : 071"  # scripted group (container) (typed FeaturePython)
  n = 2
  ref = O_element
FEATURE [App::DocumentObjectGroupPython] G4_DNA_THYMINE  # scripted group (container) (typed FeaturePython)
  Dunit = g/cm3
  Dvalue = 1
  Group = -> [H_element128,C_element138,N_element057,O_element118]
  conduct = 2
  density = 1
  expand = 3
  formula = G4_DNA_THYMINE
  name = G4_DNA_THYMINE
  specific = 4
FEATURE [App::DocumentObjectGroupPython] H_element129  label="H_element : 076"  # scripted group (container) (typed FeaturePython)
  n = 3
  ref = H_element
FEATURE [App::DocumentObjectGroupPython] C_element139  label="C_element : 084"  # scripted group (container) (typed FeaturePython)
  n = 4
  ref = C_element
FEATURE [App::DocumentObjectGroupPython] N_element058  label="N_element : 030"  # scripted group (container) (typed FeaturePython)
  n = 2
  ref = N_element
FEATURE [App::DocumentObjectGroupPython] O_element119  label="O_element : 072"  # scripted group (container) (typed FeaturePython)
  n = 2
  ref = O_element
FEATURE [App::DocumentObjectGroupPython] G4_DNA_URACIL  # scripted group (container) (typed FeaturePython)
  Dunit = g/cm3
  Dvalue = 1
  Group = -> [H_element129,C_element139,N_element058,O_element119]
  conduct = 2
  density = 1
  expand = 3
  formula = G4_DNA_URACIL
  name = G4_DNA_URACIL
  specific = 4
FEATURE [App::DocumentObjectGroupPython] H_element130  label="H_element : 077"  # scripted group (container) (typed FeaturePython)
  n = 10
  ref = H_element
FEATURE [App::DocumentObjectGroupPython] C_element140  label="C_element : 085"  # scripted group (container) (typed FeaturePython)
  n = 10
  ref = C_element
FEATURE [App::DocumentObjectGroupPython] N_element059  label="N_element : 031"  # scripted group (container) (typed FeaturePython)
  n = 5
  ref = N_element
FEATURE [App::DocumentObjectGroupPython] O_element120  label="O_element : 073"  # scripted group (container) (typed FeaturePython)
  n = 4
  ref = O_element
FEATURE [App::DocumentObjectGroupPython] G4_DNA_ADENOSINE  # scripted group (container) (typed FeaturePython)
  Dunit = g/cm3
  Dvalue = 1
  Group = -> [H_element130,C_element140,N_element059,O_element120]
  conduct = 2
  density = 1
  expand = 3
  formula = G4_DNA_ADENOSINE
  name = G4_DNA_ADENOSINE
  specific = 4
FEATURE [App::DocumentObjectGroupPython] H_element131  label="H_element : 078"  # scripted group (container) (typed FeaturePython)
  n = 10
  ref = H_element
FEATURE [App::DocumentObjectGroupPython] C_element141  label="C_element : 086"  # scripted group (container) (typed FeaturePython)
  n = 10
  ref = C_element
FEATURE [App::DocumentObjectGroupPython] N_element060  label="N_element : 032"  # scripted group (container) (typed FeaturePython)
  n = 5
  ref = N_element
FEATURE [App::DocumentObjectGroupPython] O_element121  label="O_element : 074"  # scripted group (container) (typed FeaturePython)
  n = 5
  ref = O_element
FEATURE [App::DocumentObjectGroupPython] G4_DNA_GUANOSINE  # scripted group (container) (typed FeaturePython)
  Dunit = g/cm3
  Dvalue = 1
  Group = -> [H_element131,C_element141,N_element060,O_element121]
  conduct = 2
  density = 1
  expand = 3
  formula = G4_DNA_GUANOSINE
  name = G4_DNA_GUANOSINE
  specific = 4
FEATURE [App::DocumentObjectGroupPython] H_element132  label="H_element : 079"  # scripted group (container) (typed FeaturePython)
  n = 10
  ref = H_element
FEATURE [App::DocumentObjectGroupPython] C_element142  label="C_element : 087"  # scripted group (container) (typed FeaturePython)
  n = 9
  ref = C_element
FEATURE [App::DocumentObjectGroupPython] N_element061  label="N_element : 033"  # scripted group (container) (typed FeaturePython)
  n = 3
  ref = N_element
FEATURE [App::DocumentObjectGroupPython] O_element122  label="O_element : 075"  # scripted group (container) (typed FeaturePython)
  n = 5
  ref = O_element
FEATURE [App::DocumentObjectGroupPython] G4_DNA_CYTIDINE  # scripted group (container) (typed FeaturePython)
  Dunit = g/cm3
  Dvalue = 1
  Group = -> [H_element132,C_element142,N_element061,O_element122]
  conduct = 2
  density = 1
  expand = 3
  formula = G4_DNA_CYTIDINE
  name = G4_DNA_CYTIDINE
  specific = 4
FEATURE [App::DocumentObjectGroupPython] H_element133  label="H_element : 080"  # scripted group (container) (typed FeaturePython)
  n = 9
  ref = H_element
FEATURE [App::DocumentObjectGroupPython] C_element143  label="C_element : 088"  # scripted group (container) (typed FeaturePython)
  n = 9
  ref = C_element
FEATURE [App::DocumentObjectGroupPython] N_element062  label="N_element : 034"  # scripted group (container) (typed FeaturePython)
  n = 2
  ref = N_element
FEATURE [App::DocumentObjectGroupPython] O_element123  label="O_element : 076"  # scripted group (container) (typed FeaturePython)
  n = 6
  ref = O_element
FEATURE [App::DocumentObjectGroupPython] G4_DNA_URIDINE  # scripted group (container) (typed FeaturePython)
  Dunit = g/cm3
  Dvalue = 1
  Group = -> [H_element133,C_element143,N_element062,O_element123]
  conduct = 2
  density = 1
  expand = 3
  formula = G4_DNA_URIDINE
  name = G4_DNA_URIDINE
  specific = 4
FEATURE [App::DocumentObjectGroupPython] H_element134  label="H_element : 081"  # scripted group (container) (typed FeaturePython)
  n = 11
  ref = H_element
FEATURE [App::DocumentObjectGroupPython] C_element144  label="C_element : 089"  # scripted group (container) (typed FeaturePython)
  n = 10
  ref = C_element
FEATURE [App::DocumentObjectGroupPython] N_element063  label="N_element : 035"  # scripted group (container) (typed FeaturePython)
  n = 2
  ref = N_element
FEATURE [App::DocumentObjectGroupPython] O_element124  label="O_element : 077"  # scripted group (container) (typed FeaturePython)
  n = 6
  ref = O_element
FEATURE [App::DocumentObjectGroupPython] G4_DNA_METHYLURIDINE  # scripted group (container) (typed FeaturePython)
  Dunit = g/cm3
  Dvalue = 1
  Group = -> [H_element134,C_element144,N_element063,O_element124]
  conduct = 2
  density = 1
  expand = 3
  formula = G4_DNA_METHYLURIDINE
  name = G4_DNA_METHYLURIDINE
  specific = 4
FEATURE [App::DocumentObjectGroupPython] P_element014  label="P_element : 003"  # scripted group (container) (typed FeaturePython)
  n = 1
  ref = P_element
FEATURE [App::DocumentObjectGroupPython] O_element125  label="O_element : 078"  # scripted group (container) (typed FeaturePython)
  n = 3
  ref = O_element
FEATURE [App::DocumentObjectGroupPython] G4_DNA_MONOPHOSPHATE  # scripted group (container) (typed FeaturePython)
  Dunit = g/cm3
  Dvalue = 1
  Group = -> [P_element014,O_element125]
  conduct = 2
  density = 1
  expand = 3
  formula = G4_DNA_MONOPHOSPHATE
  name = G4_DNA_MONOPHOSPHATE
  specific = 4
FEATURE [App::DocumentObjectGroupPython] H_element135  label="H_element : 082"  # scripted group (container) (typed FeaturePython)
  n = 10
  ref = H_element
FEATURE [App::DocumentObjectGroupPython] C_element145  label="C_element : 090"  # scripted group (container) (typed FeaturePython)
  n = 10
  ref = C_element
FEATURE [App::DocumentObjectGroupPython] N_element064  label="N_element : 036"  # scripted group (container) (typed FeaturePython)
  n = 5
  ref = N_element
FEATURE [App::DocumentObjectGroupPython] O_element126  label="O_element : 079"  # scripted group (container) (typed FeaturePython)
  n = 7
  ref = O_element
FEATURE [App::DocumentObjectGroupPython] P_element015  label="P_element : 004"  # scripted group (container) (typed FeaturePython)
  n = 1
  ref = P_element
FEATURE [App::DocumentObjectGroupPython] G4_DNA_A  # scripted group (container) (typed FeaturePython)
  Dunit = g/cm3
  Dvalue = 1
  Group = -> [H_element135,C_element145,N_element064,O_element126,P_element015]
  conduct = 2
  density = 1
  expand = 3
  formula = G4_DNA_A
  name = G4_DNA_A
  specific = 4
FEATURE [App::DocumentObjectGroupPython] H_element136  label="H_element : 083"  # scripted group (container) (typed FeaturePython)
  n = 10
  ref = H_element
FEATURE [App::DocumentObjectGroupPython] C_element146  label="C_element : 091"  # scripted group (container) (typed FeaturePython)
  n = 10
  ref = C_element
FEATURE [App::DocumentObjectGroupPython] N_element065  label="N_element : 037"  # scripted group (container) (typed FeaturePython)
  n = 5
  ref = N_element
FEATURE [App::DocumentObjectGroupPython] O_element127  label="O_element : 8"  # scripted group (container) (typed FeaturePython)
  n = 8
  ref = O_element
FEATURE [App::DocumentObjectGroupPython] P_element016  label="P_element : 005"  # scripted group (container) (typed FeaturePython)
  n = 1
  ref = P_element
FEATURE [App::DocumentObjectGroupPython] G4_DNA_G  # scripted group (container) (typed FeaturePython)
  Dunit = g/cm3
  Dvalue = 1
  Group = -> [H_element136,C_element146,N_element065,O_element127,P_element016]
  conduct = 2
  density = 1
  expand = 3
  formula = G4_DNA_G
  name = G4_DNA_G
  specific = 4
FEATURE [App::DocumentObjectGroupPython] H_element137  label="H_element : 084"  # scripted group (container) (typed FeaturePython)
  n = 10
  ref = H_element
FEATURE [App::DocumentObjectGroupPython] C_element147  label="C_element : 092"  # scripted group (container) (typed FeaturePython)
  n = 9
  ref = C_element
FEATURE [App::DocumentObjectGroupPython] N_element066  label="N_element : 038"  # scripted group (container) (typed FeaturePython)
  n = 3
  ref = N_element
FEATURE [App::DocumentObjectGroupPython] O_element128  label="O_element : 080"  # scripted group (container) (typed FeaturePython)
  n = 8
  ref = O_element
FEATURE [App::DocumentObjectGroupPython] P_element017  label="P_element : 006"  # scripted group (container) (typed FeaturePython)
  n = 1
  ref = P_element
FEATURE [App::DocumentObjectGroupPython] G4_DNA_C  # scripted group (container) (typed FeaturePython)
  Dunit = g/cm3
  Dvalue = 1
  Group = -> [H_element137,C_element147,N_element066,O_element128,P_element017]
  conduct = 2
  density = 1
  expand = 3
  formula = G4_DNA_C
  name = G4_DNA_C
  specific = 4
FEATURE [App::DocumentObjectGroupPython] H_element138  label="H_element : 085"  # scripted group (container) (typed FeaturePython)
  n = 9
  ref = H_element
FEATURE [App::DocumentObjectGroupPython] C_element148  label="C_element : 093"  # scripted group (container) (typed FeaturePython)
  n = 9
  ref = C_element
FEATURE [App::DocumentObjectGroupPython] N_element067  label="N_element : 039"  # scripted group (container) (typed FeaturePython)
  n = 2
  ref = N_element
FEATURE [App::DocumentObjectGroupPython] O_element129  label="O_element : 9"  # scripted group (container) (typed FeaturePython)
  n = 9
  ref = O_element
FEATURE [App::DocumentObjectGroupPython] P_element018  label="P_element : 007"  # scripted group (container) (typed FeaturePython)
  n = 1
  ref = P_element
FEATURE [App::DocumentObjectGroupPython] G4_DNA_U  # scripted group (container) (typed FeaturePython)
  Dunit = g/cm3
  Dvalue = 1
  Group = -> [H_element138,C_element148,N_element067,O_element129,P_element018]
  conduct = 2
  density = 1
  expand = 3
  formula = G4_DNA_U
  name = G4_DNA_U
  specific = 4
FEATURE [App::DocumentObjectGroupPython] H_element139  label="H_element : 086"  # scripted group (container) (typed FeaturePython)
  n = 11
  ref = H_element
FEATURE [App::DocumentObjectGroupPython] C_element149  label="C_element : 094"  # scripted group (container) (typed FeaturePython)
  n = 10
  ref = C_element
FEATURE [App::DocumentObjectGroupPython] N_element068  label="N_element : 040"  # scripted group (container) (typed FeaturePython)
  n = 2
  ref = N_element
FEATURE [App::DocumentObjectGroupPython] O_element130  label="O_element : 081"  # scripted group (container) (typed FeaturePython)
  n = 9
  ref = O_element
FEATURE [App::DocumentObjectGroupPython] P_element019  label="P_element : 008"  # scripted group (container) (typed FeaturePython)
  n = 1
  ref = P_element
FEATURE [App::DocumentObjectGroupPython] G4_DNA_MU  # scripted group (container) (typed FeaturePython)
  Dunit = g/cm3
  Dvalue = 1
  Group = -> [H_element139,C_element149,N_element068,O_element130,P_element019]
  conduct = 2
  density = 1
  expand = 3
  formula = G4_DNA_MU
  name = G4_DNA_MU
  specific = 4
FEATURE [App::DocumentObjectGroupPython] BioChemical  # scripted group (container) (typed FeaturePython)
  Group = -> [G4_CYTOSINE,G4_THYMINE,G4_URACIL,G4_DNA_ADENINE,G4_DNA_GUANINE,G4_DNA_CYTOSINE,G4_DNA_THYMINE,G4_DNA_URACIL,G4_DNA_ADENOSINE,G4_DNA_GUANOSINE,G4_DNA_CYTIDINE,G4_DNA_URIDINE,G4_DNA_METHYLURIDINE,G4_DNA_MONOPHOSPHATE,G4_DNA_A,G4_DNA_G,G4_DNA_C,G4_DNA_U,G4_DNA_MU]
FEATURE [App::DocumentObjectGroupPython] G4Materials  # scripted group (container) (typed FeaturePython)
  Group = -> [NIST,Element,HEP,Space,BioChemical]
  version = 1
FEATURE [App::DocumentObjectGroupPython] Geant4  # scripted group (container) (typed FeaturePython)
  Group = -> [G4Isotopes,G4Elements,G4Materials]
FEATURE [App::DocumentObjectGroupPython] Materials  # scripted group (container) (typed FeaturePython)
  Group = -> [Geant4]
FEATURE [Part::FeaturePython] GDMLBox_WorldBox  # WARN: FeaturePython — macro-defined, semantics opaque (R4)
  lunit = 2
  material = 5
  x = 145.922
  y = 145.922
  z = 130
FEATURE [Part::FeaturePython] GDMLBox_Box  # WARN: FeaturePython — macro-defined, semantics opaque (R4)
  Placement = pos=(30,0,0) rot=(0,0,1;0.261799rad)
  lunit = 2
  material = 0
  x = 20
  y = 10
  z = 10
FEATURE [Part::FeaturePython] Array  # Draft array (typed FeaturePython)
  AlwaysSyncPlacement = false
  Angle = 180
  ArrayType = 1
  Axis = (0,0,1)
  Base = -> GDMLBox_Box
  Center = (0,0,0)
  Count = 4
  ExpandArray = false
  Fuse = false
  IntervalAxis = (0,0,0)
  IntervalX = (50,0,0)
  IntervalY = (0,50,0)
  IntervalZ = (0,0,50)
  NumberCircles = 3
  NumberPolar = 4
  NumberX = 2
  NumberY = 2
  NumberZ = 1
  PlacementList = 4 placements: [(30,0,0),(15,25.9808,0),(-15,25.9808,0),(-30,3.67394e-15,0)]
  RadialDistance = 50
  ScaleList = (4) [(1,1,1),(1,1,1),(1,1,1),(1,1,1)]
  Symmetry = 1
  TangentialDistance = 25
FEATURE [App::Part] Part
  Group = -> [Array]
  Origin = -> Origin002
FEATURE [App::Part] worldVOL
  Group = -> [GDMLBox_WorldBox,Part]
  Origin = -> Origin
